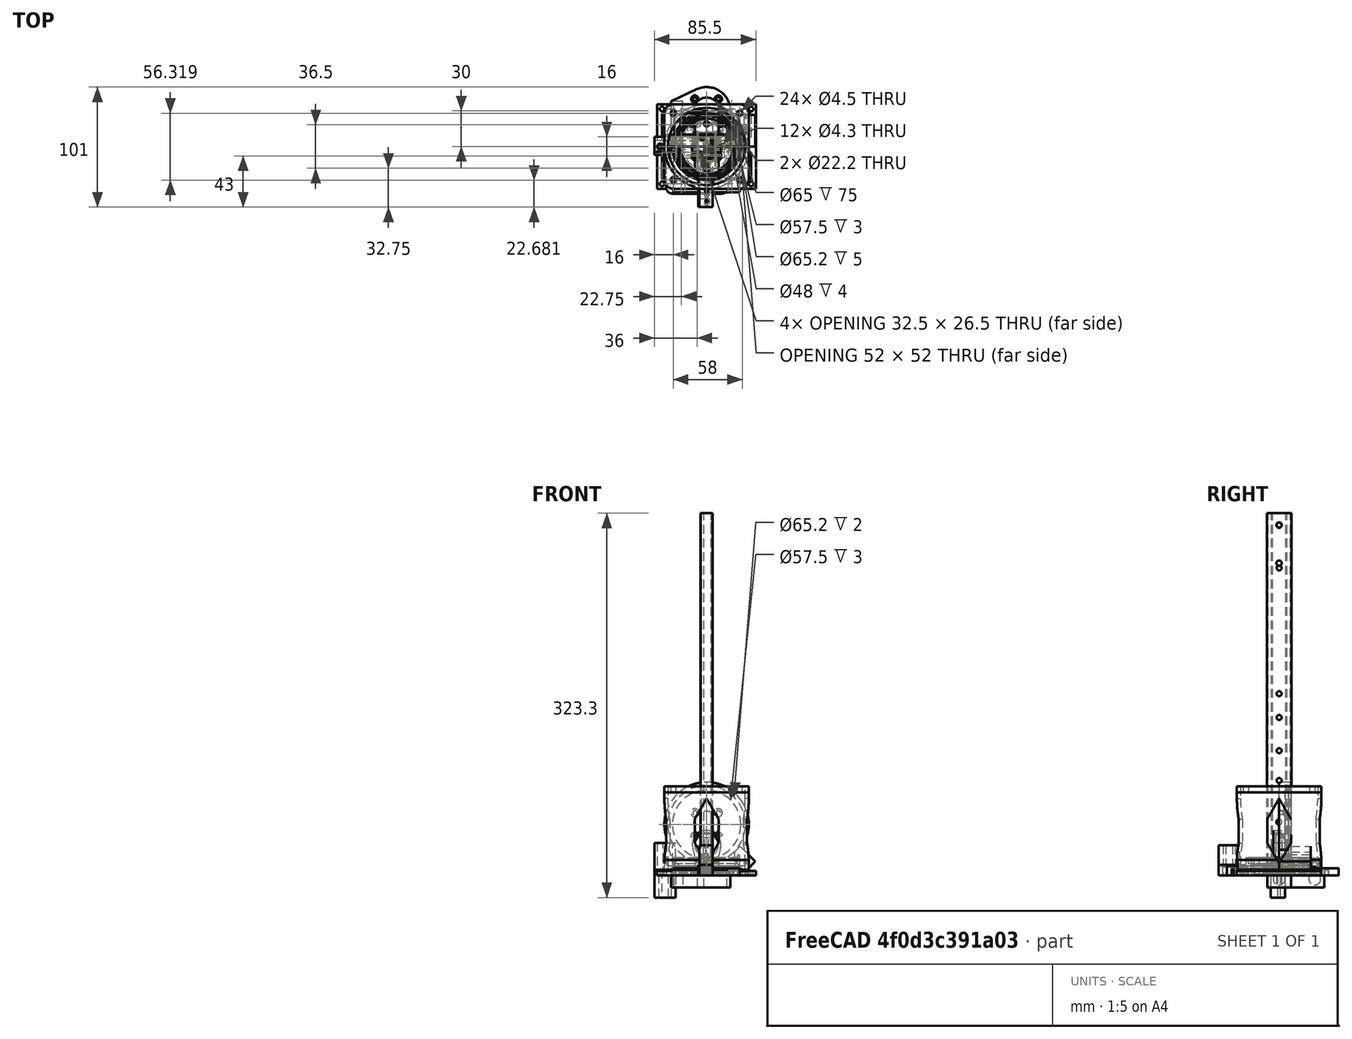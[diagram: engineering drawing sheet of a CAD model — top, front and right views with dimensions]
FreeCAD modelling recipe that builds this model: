
FCSTD DOCUMENT  (FreeCAD 0.19R24276 (Git))
Label: A4
License: All rights reserved
LicenseURL: http://en.wikipedia.org/wiki/All_rights_reserved
objects: Sketcher::SketchObject×66, PartDesign::CoordinateSystem×49, PartDesign::Pad×43, App::Link×43, TechDraw::DrawViewDimension×20, PartDesign::Body×19, App::Part×19, PartDesign::Pocket×11, PartDesign::Hole×10, TechDraw::DrawSVGTemplate×3, TechDraw::DrawProjGroupItem×3, TechDraw::DrawProjGroup×3, TechDraw::DrawPage×3, App::DocumentObjectGroup×2, App::FeaturePython×1, PartDesign::PolarPattern×1, PartDesign::Groove×1, PartDesign::Revolution×1
note: 267 computed .brp shape members not serialized (recipe doc carries the construction recipe); baked Part::Feature solids carry a one-line shape summary decoded from their .brp
EXTERNAL_REF file=HUB-545616.FCStd obj=face2
EXTERNAL_REF file=HUB-545616.FCStd obj=_45616_assembly
EXTERNAL_REF file=BALL-6810.FCStd obj=LCS_0
EXTERNAL_REF file=PULLEY-615432.FCStd obj=LCS_1
EXTERNAL_REF file=PULLEY-615432.FCStd obj=_15432_assembly
EXTERNAL_REF file=BALL-6-19-6.FCStd obj=LCS_0
EXTERNAL_REF file=BALL-6-19-6.FCStd obj=Part
EXTERNAL_REF file=WASHER-M6.FCStd obj=LCS_1
EXTERNAL_REF file=WASHER-M6.FCStd obj=WASHER_M6
EXTERNAL_REF file=HUB-545616.FCStd obj=flatFace
EXTERNAL_REF file=BALL-6808.FCStd obj=LCS_0
EXTERNAL_REF file=SCREW-M4X40.FCStd obj=LCS_0
EXTERNAL_REF file=SCREW-M4X40.FCStd obj=SCREW_M4X40
EXTERNAL_REF file=MOTOR-11HS12-0674S-PG27-E22-300.FCStd obj=mount
EXTERNAL_REF file=MOTOR-11HS12-0674S-PG27-E22-300.FCStd obj=Body
EXTERNAL_REF file=BELT-XL-180-375.FCStd obj=LCS_1
EXTERNAL_REF file=BELT-XL-180-375.FCStd obj=Body
EXTERNAL_REF file=MOTOR-17HS13-0404S-PG27.FCStd obj=LCS_0
EXTERNAL_REF file=MOTOR-17HS13-0404S-PG27.FCStd obj=Part
EXTERNAL_REF file=BALL-6810.FCStd obj=Part
EXTERNAL_REF file=BALL-6808.FCStd obj=Part
EXTERNAL_REF file=HUB_1309_0016_0006.FCStd obj=flat
EXTERNAL_REF file=A4-GRIPPER.FCStd obj=A4001
EXTERNAL_REF file=A4-GRIPPER.FCStd obj=Model
EXTERNAL_REF file=SCREW_8X375.FCStd obj=LCS_0
EXTERNAL_REF file=SCREW_8X375.FCStd obj=Part
EXTERNAL_REF file=SCREW_8X250.FCStd obj=LCS_1
EXTERNAL_REF file=SCREW_8X250.FCStd obj=Part
EXTERNAL_REF file=HUB_1309_0016_0006.FCStd obj=_309_0016_0006_assembly
EXTERNAL_REF file=Paint Roller Copy/A4_PAINT_ROLLER_1V0.FCStd obj=robot001
EXTERNAL_REF file=Paint Roller Copy/A4_PAINT_ROLLER_1V0.FCStd obj=Model

FEATURE [PartDesign::CoordinateSystem] LCS_Origin
  AttacherType = Attacher::AttachEngine3D
  MapMode = 2
  Support = -> [X_Axis]
FEATURE [App::DocumentObjectGroup] Constraints
FEATURE [App::FeaturePython] Variables  label="var"  # WARN: FeaturePython — macro-defined, semantics opaque (R4)
  J2BaseEncoderH = 27.5
  J3BaseEncoderH = 23.5
  LimitSwitchThroughHoleLoc1 = 3.5
  LimitSwitchThroughHoleLoc2 = 4.5
  angleG = 0
  angleJ0 = -90
  angleJ1 = -90
  angleJ2 = 180
  angleJ3 = -45
  baseJ0ID = 92
  baseJ0LimitOffset = 8
  baseJ1EncoderH = 26.5
  baseJ1FlatFace = 30.5941
  baseJ1HoleP1 = 20
  baseJ1HoleP2 = 24
  baseJ1HoleP3 = 50
  baseJ1HoleP4 = 14
  baseJ1MotorH = 43
  baseJ1OD = 66
  baseJ2OD = 52
  encoderJ0H = 25.5
  gripperMobileOD = 27
  hubHoleD = 3.81
  hubHolePD = 19.558
  hubScrewCBOR = 2.35
  humerusW = 20.6375
  limitSwitchHoleD = 3.1
  limitSwitchHoleLoc = 3
  limitSwitchHoleP = 7
  limitSwitchL = 13
  limitSwitchThroughHoleL = 3
  limitSwitchThroughHoleW = 2
  limitSwitchW = 14
  m4HeatSetD = 6.2
  motorJ0HoleD = 3.3
  motorJ0HolePD = 28
  motorJ0LocD = 22.2
  plateJ1HumerusHoleP = 40
  riserHoleD = 4.5
  riserHoleP = 81
  riserID = 65
  riserOD = 71
  screw6BHD = 6.6548
  tensionJ2 = 12
  tensionerJ2ScrewH = 9
  thrustBearingJ0T = 5
  expr: hubHolePD = 0.77 * 25.4
  expr: baseJ1FlatFace = cos(asin(33 / 45)) * 45
  expr: humerusW = 13 / 16 * 25.4
  expr: screw6BHD = 25.4 * 0.262
FEATURE [PartDesign::CoordinateSystem] LCS_0
  AttacherType = Attacher::AttachEngine3D
  MapMode = 2
  Support = -> [X_Axis001]
FEATURE [Sketcher::SketchObject] Sketch002
  AttachmentOffset = pos=(0,0,70) rot=(0,0,1;0rad)
  FullyConstrained = true
  MapMode = 5
  Placement = pos=(0,0,70) rot=(0,0,1;0rad)
  Support = -> [XY_Plane002]
  expr: Constraints[22] = <<var>>.riserHoleD
  expr: Constraints[27] = <<var>>.riserOD - 1
  expr: Constraints[12] = <<var>>.riserOD - 15
  expr: Constraints[13] = <<var>>.riserOD
  sketch-geometry (13):
    g0: LineSegment StartX=-28 StartY=35.5 StartZ=0 EndX=28 EndY=35.5 EndZ=0
    g1: LineSegment StartX=35.5 StartY=28 StartZ=0 EndX=35.5 EndY=-28 EndZ=0
    g2: LineSegment StartX=28 StartY=-35.5 StartZ=0 EndX=-28 EndY=-35.5 EndZ=0
    g3: LineSegment StartX=-35.5 StartY=-28 StartZ=0 EndX=-35.5 EndY=28 EndZ=0
    g4: ArcOfCircle CenterX=-28 CenterY=28 CenterZ=0 NormalX=0 NormalY=0 NormalZ=1 AngleXU=0 Radius=7.5 StartAngle=1.5708 EndAngle=3.14159
    g5: ArcOfCircle CenterX=28 CenterY=28 CenterZ=0 NormalX=0 NormalY=0 NormalZ=1 AngleXU=0 Radius=7.5 StartAngle=0 EndAngle=1.5708
    g6: ArcOfCircle CenterX=28 CenterY=-28 CenterZ=0 NormalX=0 NormalY=0 NormalZ=1 AngleXU=0 Radius=7.5 StartAngle=4.71239 EndAngle=6.28319
    g7: ArcOfCircle CenterX=-28 CenterY=-28 CenterZ=0 NormalX=0 NormalY=0 NormalZ=1 AngleXU=0 Radius=7.5 StartAngle=3.14159 EndAngle=4.71239
    g8: Circle CenterX=-28 CenterY=28 CenterZ=0 NormalX=0 NormalY=0 NormalZ=1 AngleXU=0 Radius=2.25
    g9: Circle CenterX=28 CenterY=28 CenterZ=0 NormalX=0 NormalY=0 NormalZ=1 AngleXU=0 Radius=2.25
    g10: Circle CenterX=28 CenterY=-28 CenterZ=0 NormalX=0 NormalY=0 NormalZ=1 AngleXU=0 Radius=2.25
    g11: Circle CenterX=-28 CenterY=-28 CenterZ=0 NormalX=0 NormalY=0 NormalZ=1 AngleXU=0 Radius=2.25
    g12: Circle CenterX=0 CenterY=0 CenterZ=0 NormalX=0 NormalY=0 NormalZ=1 AngleXU=0 Radius=35
  constraints (28):
    c: Horizontal(g0)
    c: Horizontal(g2)
    c: Vertical(g1)
    c: Vertical(g3)
    c: Tangent(g0,g4) = 1.5708
    c: Tangent(g3,g4) = 1.5708
    c: Tangent(g0,g5) = 1.5708
    c: Tangent(g1,g5) = 1.5708
    c: Tangent(g1,g6) = 1.5708
    c: Tangent(g2,g6) = 1.5708
    c: Tangent(g3,g7) = 1.5708
    c: Tangent(g2,g7) = 1.5708
    c: DistanceX(g4,g5) = 56
    c: DistanceX(g3,g1) = 71
    c: Equal(g7,g6)
    c: Symmetric(g4,g5,g-2)
    c: Symmetric(g4,g7,g-1)
    c: Equal(g3,g0)
    c: Coincident(g8,g4)
    c: Coincident(g9,g5)
    c: Coincident(g10,g6)
    c: Coincident(g11,g7)
    c: Diameter(g11) = 4.5
    c: Equal(g11,g8)
    c: Equal(g11,g9)
    c: Equal(g11,g10)
    c: Coincident(g12,g-1)
    c: Diameter(g12) = 70
FEATURE [Sketcher::SketchObject] Sketch003
  FullyConstrained = true
  MapMode = 5
  Placement = pos=(0,0,0) rot=(1,0,0;1.5708rad)
  Support = -> [XZ_Plane002]
  sketch-geometry (8):
    g0: LineSegment StartX=0 StartY=64.8205 StartZ=0 EndX=-10 EndY=47.5 EndZ=0
    g1: LineSegment StartX=-10 StartY=47.5 StartZ=0 EndX=-10 EndY=27.5 EndZ=0
    g2: LineSegment StartX=-10 StartY=27.5 StartZ=0 EndX=0 EndY=10.1795 EndZ=0
    g3: LineSegment StartX=0 StartY=10.1795 StartZ=0 EndX=10 EndY=27.5 EndZ=0
    g4: LineSegment StartX=10 StartY=27.5 StartZ=0 EndX=10 EndY=47.5 EndZ=0
    g5: LineSegment StartX=10 StartY=47.5 StartZ=0 EndX=0 EndY=64.8205 EndZ=0
    g6: GeomPoint X=0 Y=37.5 Z=0
    g7: LineSegment StartX=-10 StartY=47.5 StartZ=0 EndX=10 EndY=27.5 EndZ=0
  constraints (21):
    c: PointOnObject(g0,g-2)
    c: Coincident(g0,g1)
    c: Vertical(g1)
    c: Coincident(g1,g2)
    c: PointOnObject(g2,g-2)
    c: Coincident(g2,g3)
    c: Coincident(g3,g4)
    c: Vertical(g4)
    c: Coincident(g4,g5)
    c: Coincident(g5,g0)
    c: Symmetric(g0,g4,g-2)
    c: Equal(g1,g4)
    c: Angle(g0,g5) = 1.0472
    c: DistanceX(g0,g4) = 20
    c: PointOnObject(g6,g-2)
    c: Coincident(g7,g0)
    c: Coincident(g7,g3)
    c: PointOnObject(g6,g7)
    c: DistanceY(g-1,g6) = 37.5
    c: Equal(g2,g0)
    c: DistanceY(g1,g1) = 20
FEATURE [Sketcher::SketchObject] Sketch001
  FullyConstrained = true
  MapMode = 5
  Support = -> [XY_Plane002]
  expr: Constraints[22] = <<var>>.riserHoleD
  expr: Constraints[27] = Variables.riserOD - 1
  expr: Constraints[12] = Variables.riserOD - 15
  expr: Constraints[13] = Variables.riserOD
  sketch-geometry (13):
    g0: LineSegment StartX=-28 StartY=35.5 StartZ=0 EndX=28 EndY=35.5 EndZ=0
    g1: LineSegment StartX=35.5 StartY=28 StartZ=0 EndX=35.5 EndY=-28 EndZ=0
    g2: LineSegment StartX=28 StartY=-35.5 StartZ=0 EndX=-28 EndY=-35.5 EndZ=0
    g3: LineSegment StartX=-35.5 StartY=-28 StartZ=0 EndX=-35.5 EndY=28 EndZ=0
    g4: ArcOfCircle CenterX=-28 CenterY=28 CenterZ=0 NormalX=0 NormalY=0 NormalZ=1 AngleXU=0 Radius=7.5 StartAngle=1.5708 EndAngle=3.14159
    g5: ArcOfCircle CenterX=28 CenterY=28 CenterZ=0 NormalX=0 NormalY=0 NormalZ=1 AngleXU=0 Radius=7.5 StartAngle=1e-16 EndAngle=1.5708
    g6: ArcOfCircle CenterX=28 CenterY=-28 CenterZ=0 NormalX=0 NormalY=0 NormalZ=1 AngleXU=0 Radius=7.5 StartAngle=4.71239 EndAngle=6.28319
    g7: ArcOfCircle CenterX=-28 CenterY=-28 CenterZ=0 NormalX=0 NormalY=0 NormalZ=1 AngleXU=0 Radius=7.5 StartAngle=3.14159 EndAngle=4.71239
    g8: Circle CenterX=-28 CenterY=28 CenterZ=0 NormalX=0 NormalY=0 NormalZ=1 AngleXU=0 Radius=2.25
    g9: Circle CenterX=28 CenterY=28 CenterZ=0 NormalX=0 NormalY=0 NormalZ=1 AngleXU=0 Radius=2.25
    g10: Circle CenterX=28 CenterY=-28 CenterZ=0 NormalX=0 NormalY=0 NormalZ=1 AngleXU=0 Radius=2.25
    g11: Circle CenterX=-28 CenterY=-28 CenterZ=0 NormalX=0 NormalY=0 NormalZ=1 AngleXU=0 Radius=2.25
    g12: Circle CenterX=0 CenterY=0 CenterZ=0 NormalX=0 NormalY=0 NormalZ=1 AngleXU=0 Radius=35
  constraints (28):
    c: Horizontal(g0)
    c: Horizontal(g2)
    c: Vertical(g1)
    c: Vertical(g3)
    c: Tangent(g0,g4) = 1.5708
    c: Tangent(g3,g4) = 1.5708
    c: Tangent(g0,g5) = 1.5708
    c: Tangent(g1,g5) = 1.5708
    c: Tangent(g1,g6) = 1.5708
    c: Tangent(g2,g6) = 1.5708
    c: Tangent(g3,g7) = 1.5708
    c: Tangent(g2,g7) = 1.5708
    c: DistanceX(g4,g5) = 56
    c: DistanceX(g3,g1) = 71
    c: Equal(g7,g6)
    c: Symmetric(g4,g5,g-2)
    c: Symmetric(g4,g7,g-1)
    c: Equal(g3,g0)
    c: Coincident(g8,g4)
    c: Coincident(g9,g5)
    c: Coincident(g10,g6)
    c: Coincident(g11,g7)
    c: Diameter(g11) = 4.5
    c: Equal(g11,g8)
    c: Equal(g11,g9)
    c: Equal(g11,g10)
    c: Coincident(g12,g-1)
    c: Diameter(g12) = 70
FEATURE [Sketcher::SketchObject] Sketch
  FullyConstrained = true
  MapMode = 5
  Support = -> [XY_Plane002]
  sketch-geometry (7):
    g0: Circle CenterX=0 CenterY=0 CenterZ=0 NormalX=0 NormalY=0 NormalZ=1 AngleXU=0 Radius=32.5
    g1: Circle CenterX=0 CenterY=0 CenterZ=0 NormalX=0 NormalY=0 NormalZ=1 AngleXU=0 Radius=35.5
    g2: LineSegment StartX=-21.15 StartY=21.15 StartZ=0 EndX=21.15 EndY=21.15 EndZ=0
    g3: LineSegment StartX=21.15 StartY=21.15 StartZ=0 EndX=21.15 EndY=-21.15 EndZ=0
    g4: LineSegment StartX=21.15 StartY=-21.15 StartZ=0 EndX=-21.15 EndY=-21.15 EndZ=0
    g5: LineSegment StartX=-21.15 StartY=-21.15 StartZ=0 EndX=-21.15 EndY=21.15 EndZ=0
    g6: Circle CenterX=0 CenterY=0 CenterZ=0 NormalX=0 NormalY=0 NormalZ=1 AngleXU=0 Radius=29.9106
  constraints (17):
    c: Coincident(g0,g-1)
    c: Coincident(g1,g0)
    c: Diameter(g1) = 71
    c: Diameter(g0) = 65
    c: Coincident(g2,g3)
    c: Coincident(g3,g4)
    c: Coincident(g4,g5)
    c: Coincident(g5,g2)
    c: Horizontal(g4)
    c: Vertical(g3)
    c: Symmetric(g2,g2,g-2)
    c: Equal(g2,g5)
    c: Symmetric(g2,g4,g-1)
    c: DistanceX(g2,g2) = 42.3
    c: Coincident(g6,g0)
    c: Diameter(g6) = 59.8212
    c: PointOnObject(g3,g6)
FEATURE [PartDesign::Pad] Pad
  Direction = (1,1,1)
  Length = 75
  Length2 = 100
  Profile = -> Sketch
  Refine = true
  Type = 0
FEATURE [PartDesign::Pad] Pad001
  BaseFeature = -> Pad
  Direction = (1,1,1)
  Length = 5
  Length2 = 100
  Profile = -> Sketch001
  Refine = true
  Type = 0
FEATURE [PartDesign::Pad] Pad002
  BaseFeature = -> Pad001
  Direction = (1,1,1)
  Length = 5
  Length2 = 100
  Profile = -> Sketch002
  Refine = true
  Type = 0
FEATURE [PartDesign::Pocket] Pocket
  BaseFeature = -> Pad002
  Length = 5
  Length2 = 100
  Midplane = true
  Profile = -> Sketch003
  Refine = true
  Type = 1
FEATURE [PartDesign::PolarPattern] PolarPattern
  Angle = 90
  Axis = -> Sketch003 [V_Axis]
  BaseFeature = -> Pocket
  Occurrences = 2
  Originals = -> [Pocket]
  Refine = true
FEATURE [PartDesign::Body] Body
  Group = -> [Sketch,Pad,Sketch001,Sketch002,Pad001,Pad002,Sketch003,Pocket,PolarPattern]
  Origin = -> Origin002
  Tip = -> PolarPattern
FEATURE [PartDesign::CoordinateSystem] baseJ0
  AttacherType = Attacher::AttachEngine3D
  MapMode = 11
  Placement = pos=(0,0,75) rot=(0,0,1;1.5708rad)
  Support = -> [PolarPattern]
FEATURE [PartDesign::CoordinateSystem] LCS_0001
  AttacherType = Attacher::AttachEngine3D
  MapMode = 2
  Support = -> [X_Axis003]
FEATURE [Sketcher::SketchObject] Sketch004
  FullyConstrained = true
  MapMode = 5
  Support = -> [XY_Plane004]
  expr: Constraints[46] = <<var>>.motorJ0HoleD
  expr: Constraints[41] = <<var>>.motorJ0LocD
  expr: Constraints[40] = <<var>>.motorJ0HolePD
  expr: Constraints[24] = <<var>>.riserOD
  expr: Constraints[20] = <<var>>.riserOD - 15
  expr: Constraints[16] = <<var>>.riserHoleD
  sketch-geometry (22):
    g0: LineSegment StartX=-28 StartY=35.5 StartZ=0 EndX=28 EndY=35.5 EndZ=0
    g1: LineSegment StartX=35.5 StartY=28 StartZ=0 EndX=35.5 EndY=-28 EndZ=0
    g2: LineSegment StartX=28 StartY=-35.5 StartZ=0 EndX=-28 EndY=-35.5 EndZ=0
    g3: LineSegment StartX=-35.5 StartY=-28 StartZ=0 EndX=-35.5 EndY=28 EndZ=0
    g4: ArcOfCircle CenterX=-28 CenterY=28 CenterZ=0 NormalX=0 NormalY=0 NormalZ=1 AngleXU=0 Radius=7.5 StartAngle=1.5708 EndAngle=3.14159
    g5: ArcOfCircle CenterX=-28 CenterY=-28 CenterZ=0 NormalX=0 NormalY=0 NormalZ=1 AngleXU=0 Radius=7.5 StartAngle=3.14159 EndAngle=4.71239
    g6: ArcOfCircle CenterX=28 CenterY=-28 CenterZ=0 NormalX=0 NormalY=0 NormalZ=1 AngleXU=0 Radius=7.5 StartAngle=4.71239 EndAngle=6.28319
    g7: ArcOfCircle CenterX=28 CenterY=28 CenterZ=0 NormalX=0 NormalY=0 NormalZ=1 AngleXU=0 Radius=7.5 StartAngle=-9e-16 EndAngle=1.5708
    g8: Circle CenterX=-28 CenterY=28 CenterZ=0 NormalX=0 NormalY=0 NormalZ=1 AngleXU=0 Radius=2.25
    g9: Circle CenterX=28 CenterY=28 CenterZ=0 NormalX=0 NormalY=0 NormalZ=1 AngleXU=0 Radius=2.25
    g10: Circle CenterX=28 CenterY=-28 CenterZ=0 NormalX=0 NormalY=0 NormalZ=1 AngleXU=0 Radius=2.25
    g11: Circle CenterX=-28 CenterY=-28 CenterZ=0 NormalX=0 NormalY=0 NormalZ=1 AngleXU=0 Radius=2.25
    g12: Circle CenterX=0 CenterY=0 CenterZ=0 NormalX=0 NormalY=0 NormalZ=1 AngleXU=0 Radius=11.1
    g13: LineSegment StartX=-9.89949 StartY=9.89949 StartZ=0 EndX=9.89949 EndY=9.89949 EndZ=0
    g14: LineSegment StartX=9.89949 StartY=9.89949 StartZ=0 EndX=9.89949 EndY=-9.89949 EndZ=0
    g15: LineSegment StartX=9.89949 StartY=-9.89949 StartZ=0 EndX=-9.89949 EndY=-9.89949 EndZ=0
    g16: LineSegment StartX=-9.89949 StartY=-9.89949 StartZ=0 EndX=-9.89949 EndY=9.89949 EndZ=0
    g17: Circle CenterX=0 CenterY=0 CenterZ=0 NormalX=0 NormalY=0 NormalZ=1 AngleXU=0 Radius=14
    g18: Circle CenterX=-9.89949 CenterY=9.89949 CenterZ=0 NormalX=0 NormalY=0 NormalZ=1 AngleXU=0 Radius=1.65
    g19: Circle CenterX=9.89949 CenterY=9.89949 CenterZ=0 NormalX=0 NormalY=0 NormalZ=1 AngleXU=0 Radius=1.65
    g20: Circle CenterX=9.89949 CenterY=-9.89949 CenterZ=0 NormalX=0 NormalY=0 NormalZ=1 AngleXU=0 Radius=1.65
    g21: Circle CenterX=-9.89949 CenterY=-9.89949 CenterZ=0 NormalX=0 NormalY=0 NormalZ=1 AngleXU=0 Radius=1.65
  constraints (50):
    c: Horizontal(g0)
    c: Horizontal(g2)
    c: Vertical(g1)
    c: Vertical(g3)
    c: Tangent(g0,g4) = 1.5708
    c: Tangent(g3,g4) = 1.5708
    c: Tangent(g3,g5) = 1.5708
    c: Tangent(g2,g5) = 1.5708
    c: Tangent(g2,g6) = 1.5708
    c: Tangent(g1,g6) = 1.5708
    c: Tangent(g1,g7) = 1.5708
    c: Tangent(g0,g7) = 1.5708
    c: Coincident(g8,g4)
    c: Coincident(g9,g7)
    c: Coincident(g10,g6)
    c: Coincident(g11,g5)
    c: Diameter(g11) = 4.5
    c: Equal(g11,g8)
    c: Equal(g11,g9)
    c: Equal(g11,g10)
    c: DistanceX(g4,g7) = 56
    c: Symmetric(g4,g5,g-1)
    c: Symmetric(g4,g7,g-2)
    c: Equal(g0,g3)
    c: DistanceX(g3,g1) = 71
    c: Equal(g6,g7)
    c: Coincident(g12,g-1)
    c: Coincident(g13,g14)
    c: Coincident(g14,g15)
    c: Coincident(g15,g16)
    c: Coincident(g16,g13)
    c: Horizontal(g13)
    c: Horizontal(g15)
    c: Vertical(g14)
    c: Vertical(g16)
    c: Coincident(g17,g12)
    c: PointOnObject(g13,g17)
    c: PointOnObject(g13,g17)
    c: Equal(g14,g15)
    c: PointOnObject(g14,g17)
    c: Diameter(g17) = 28
    c: Diameter(g12) = 22.2
    c: Coincident(g18,g13)
    c: Coincident(g19,g13)
    c: Coincident(g20,g14)
    c: Coincident(g21,g15)
    c: Diameter(g21) = 3.3
    c: Equal(g21,g20)
    c: Equal(g21,g19)
    c: Equal(g21,g18)
FEATURE [PartDesign::Pad] Pad005
  Direction = (1,1,1)
  Length = 5
  Length2 = 100
  Profile = -> Sketch004
  Refine = true
  Type = 0
FEATURE [Sketcher::SketchObject] Sketch005
  AttachmentOffset = pos=(0,0,5) rot=(0,0,1;0rad)
  FullyConstrained = true
  MapMode = 5
  Placement = pos=(0,0,5) rot=(0,0,1;0rad)
  Support = -> [XY_Plane004]
  expr: .AttachmentOffset.Base.z = 5
  sketch-geometry (2):
    g0: Circle CenterX=0 CenterY=0 CenterZ=0 NormalX=0 NormalY=0 NormalZ=1 AngleXU=0 Radius=35.5
    g1: Circle CenterX=0 CenterY=0 CenterZ=0 NormalX=0 NormalY=0 NormalZ=1 AngleXU=0 Radius=32.6
  constraints (4):
    c: Coincident(g0,g-1)
    c: Coincident(g1,g0)
    c: Diameter(g1) = 65.2
    c: Diameter(g0) = 71
FEATURE [PartDesign::Pad] Pad006
  BaseFeature = -> Pad005
  Direction = (1,1,1)
  Length = 8
  Length2 = 100
  Profile = -> Sketch005
  Refine = true
  Type = 0
FEATURE [App::Link] RISER_1_0001  label="RISER"
  AssemblyType = Asm4EE
  AttachedBy = #LCS_0
  AttachedTo = Parent Assembly#LCS_Origin
  LinkedObject = -> RISER_1_0
  expr: Placement = LCS_Origin.Placement * AttachmentOffset * LCS_0.Placement ^ -1
FEATURE [App::Link] BASE_J0_1_0001
  AssemblyType = Asm4EE
  AttachedBy = #LCS_0001
  AttachedTo = RISER_1_0001#baseJ0
  LinkPlacement = pos=(0,0,75) rot=(0,0,1;1.5708rad)
  LinkedObject = -> BASE_J0_1_0
  Placement = pos=(0,0,75) rot=(0,0,1;1.5708rad)
  expr: Placement = RISER_1_0001.Placement * baseJ0.Placement * AttachmentOffset * LCS_0001.Placement ^ -1
FEATURE [App::Link] HUB_545616_1
  AssemblyType = Asm4EE
  AttachedBy = #face2
  AttachedTo = BASE_J0_1_0001#LCS_0001
  AttachmentOffset = pos=(0,0,7) rot=(0,0,-1;-1.5708rad)
  LinkPlacement = pos=(17.0898,-21.6153,88.521) rot=(0.57735,-0.57735,-0.57735;2.0944rad)
  LinkedObject = -> <external HUB-545616.FCStd>#_45616_assembly
  Placement = pos=(17.0898,-21.6153,88.521) rot=(0.57735,-0.57735,-0.57735;2.0944rad)
  expr: Placement = BASE_J0_1_0001.Placement * LCS_0001.Placement * AttachmentOffset * HUB_545616#face2.Placement ^ -1
  expr: .AttachmentOffset.Rotation.Angle = <<var>>.angleJ0
FEATURE [PartDesign::CoordinateSystem] LCS_0002
  AttacherType = Attacher::AttachEngine3D
  MapMode = 2
  Support = -> [X_Axis005]
FEATURE [Sketcher::SketchObject] Sketch008
  FullyConstrained = true
  MapMode = 5
  Support = -> [XY_Plane006]
  sketch-geometry (2):
    g0: Circle CenterX=0 CenterY=0 CenterZ=0 NormalX=0 NormalY=0 NormalZ=1 AngleXU=0 Radius=3.1
    g1: Circle CenterX=0 CenterY=0 CenterZ=0 NormalX=0 NormalY=0 NormalZ=1 AngleXU=0 Radius=27
  constraints (4):
    c: Diameter(g0) = 6.2
    c: Coincident(g0,g-1)
    c: Coincident(g1,g0)
    c: Diameter(g1) = 54
FEATURE [PartDesign::Pad] Pad007
  AllowMultiFace = false
  Direction = (1,1,1)
  Length = 8
  Length2 = 100
  Profile = -> Sketch008
  Type = 0
FEATURE [Sketcher::SketchObject] Sketch012
  AttachmentOffset = pos=(0,0,8) rot=(0,0,1;0rad)
  FullyConstrained = true
  MapMode = 5
  Placement = pos=(0,0,8) rot=(0,0,1;0rad)
  Support = -> [XY_Plane006]
  expr: Constraints[16] = <<var>>.hubHoleD
  expr: Constraints[15] = <<var>>.hubHolePD
  sketch-geometry (9):
    g0: LineSegment StartX=-6.9148 StartY=6.9148 StartZ=0 EndX=6.9148 EndY=6.9148 EndZ=0
    g1: LineSegment StartX=6.9148 StartY=6.9148 StartZ=0 EndX=6.9148 EndY=-6.9148 EndZ=0
    g2: LineSegment StartX=6.9148 StartY=-6.9148 StartZ=0 EndX=-6.9148 EndY=-6.9148 EndZ=0
    g3: LineSegment StartX=-6.9148 StartY=-6.9148 StartZ=0 EndX=-6.9148 EndY=6.9148 EndZ=0
    g4: Circle CenterX=-6.9148 CenterY=6.9148 CenterZ=0 NormalX=0 NormalY=0 NormalZ=1 AngleXU=0 Radius=1.905
    g5: Circle CenterX=6.9148 CenterY=6.9148 CenterZ=0 NormalX=0 NormalY=0 NormalZ=1 AngleXU=0 Radius=1.905
    g6: Circle CenterX=6.9148 CenterY=-6.9148 CenterZ=0 NormalX=0 NormalY=0 NormalZ=1 AngleXU=0 Radius=1.905
    g7: Circle CenterX=-6.9148 CenterY=-6.9148 CenterZ=0 NormalX=0 NormalY=0 NormalZ=1 AngleXU=0 Radius=1.905
    g8: LineSegment StartX=-6.9148 StartY=6.9148 StartZ=0 EndX=6.9148 EndY=-6.9148 EndZ=0
  constraints (20):
    c: Coincident(g0,g1)
    c: Coincident(g1,g2)
    c: Coincident(g2,g3)
    c: Coincident(g3,g0)
    c: Horizontal(g2)
    c: Vertical(g1)
    c: Symmetric(g0,g0,g-2)
    c: Symmetric(g0,g2,g-1)
    c: Equal(g3,g0)
    c: Coincident(g4,g0)
    c: Coincident(g5,g0)
    c: Coincident(g6,g1)
    c: Coincident(g7,g2)
    c: Coincident(g8,g4)
    c: Coincident(g8,g6)
    c: Distance(g8) = 19.558
    c: Diameter(g4) = 3.81
    c: Equal(g4,g7)
    c: Equal(g4,g6)
    c: Equal(g4,g5)
FEATURE [App::Link] PLATE_J0_1_0001  label="J0_PLATE"
  AssemblyType = Asm4EE
  AttachedBy = #LCS_0002
  AttachedTo = BALL_6810_0#LCS_0
  AttachmentOffset = pos=(0,0,7) rot=(0,0,1;-1.5708rad)
  LinkPlacement = pos=(0,0,90) rot=(0,0,1;0rad)
  LinkedObject = -> PLATE_J0_1_0
  Placement = pos=(0,0,90) rot=(0,0,1;0rad)
  expr: .AttachmentOffset.Rotation.Angle = <<var>>.angleJ0
  expr: Placement = BALL_6810_0.Placement * BALL_6810#LCS_0.Placement * AttachmentOffset * LCS_0002.Placement ^ -1
FEATURE [PartDesign::CoordinateSystem] LCS_0003
  AttacherType = Attacher::AttachEngine3D
  MapMode = 2
  Support = -> [X_Axis007]
FEATURE [Sketcher::SketchObject] Sketch016
  FullyConstrained = true
  MapMode = 5
  Support = -> [XY_Plane008]
  sketch-geometry (7):
    g0: LineSegment StartX=-20 StartY=15 StartZ=0 EndX=20 EndY=15 EndZ=0
    g1: Circle CenterX=-20 CenterY=15 CenterZ=0 NormalX=0 NormalY=0 NormalZ=1 AngleXU=0 Radius=2.35
    g2: Circle CenterX=20 CenterY=15 CenterZ=0 NormalX=0 NormalY=0 NormalZ=1 AngleXU=0 Radius=2.35
    g3: LineSegment StartX=-27 StartY=0 StartZ=0 EndX=27 EndY=0 EndZ=0
    g4: LineSegment StartX=27 StartY=0 StartZ=0 EndX=27 EndY=20 EndZ=0
    g5: LineSegment StartX=27 StartY=20 StartZ=0 EndX=-27 EndY=20 EndZ=0
    g6: LineSegment StartX=-27 StartY=20 StartZ=0 EndX=-27 EndY=0 EndZ=0
  constraints (18):
    c: Coincident(g1,g0)
    c: Coincident(g2,g0)
    c: DistanceX(g0,g0) = 40
    c: DistanceY(g-1,g2) = 15
    c: Symmetric(g1,g2,g-2)
    c: Coincident(g4,g5)
    c: Coincident(g5,g6)
    c: Coincident(g6,g3)
    c: Horizontal(g3)
    c: Vertical(g4)
    c: Vertical(g6)
    c: PointOnObject(g3,g-1)
    c: DistanceX(g5,g5) = 54
    c: Symmetric(g5,g4,g-2)
    c: DistanceY(g4,g4) = 20
    c: Coincident(g3,g4)
    c: Diameter(g2) = 4.7
    c: Equal(g2,g1)
FEATURE [PartDesign::Pad] Pad010
  AllowMultiFace = false
  Direction = (1,1,1)
  Length = 5
  Length2 = 100
  Profile = -> Sketch016
  Type = 0
FEATURE [Sketcher::SketchObject] Sketch017
  AttachmentOffset = pos=(0,0,-5) rot=(0,0,1;0rad)
  FullyConstrained = true
  MapMode = 5
  Placement = pos=(0,5,1.1e-15) rot=(1,0,0;1.5708rad)
  Support = -> [XZ_Plane008]
  expr: Constraints[1] = <<var>>.baseJ1MotorH
  sketch-geometry (1):
    g0: Circle CenterX=0 CenterY=43 CenterZ=0 NormalX=0 NormalY=0 NormalZ=1 AngleXU=0 Radius=32.6
  constraints (3):
    c: Diameter(g0) = 65.2
    c: DistanceY(g-1,g0) = 43
    c: PointOnObject(g0,g-2)
FEATURE [Sketcher::SketchObject] Sketch019
  FullyConstrained = true
  MapMode = 5
  Placement = pos=(0,0,0) rot=(1,0,0;1.5708rad)
  Support = -> [XZ_Plane008]
  expr: Constraints[3] = <<var>>.baseJ1MotorH
  expr: Constraints[32] = <<var>>.motorJ0HolePD
  expr: Constraints[23] = <<var>>.motorJ0LocD
  expr: Constraints[18] = <<var>>.motorJ0HoleD
  sketch-geometry (15):
    g0: LineSegment StartX=-27 StartY=5 StartZ=0 EndX=-34.4144 EndY=34.2878 EndZ=0
    g1: LineSegment StartX=34.4144 StartY=34.2878 StartZ=0 EndX=27 EndY=5 EndZ=0
    g2: LineSegment StartX=-27 StartY=5 StartZ=0 EndX=27 EndY=5 EndZ=0
    g3: ArcOfCircle CenterX=0 CenterY=43 CenterZ=0 NormalX=0 NormalY=0 NormalZ=1 AngleXU=0 Radius=35.5 StartAngle=6.03524 EndAngle=9.67272
    g4: Circle CenterX=0 CenterY=43 CenterZ=0 NormalX=0 NormalY=0 NormalZ=1 AngleXU=0 Radius=11.1
    g5: Circle CenterX=9.89949 CenterY=52.8995 CenterZ=0 NormalX=0 NormalY=0 NormalZ=1 AngleXU=0 Radius=1.65
    g6: Circle CenterX=-9.89949 CenterY=52.8995 CenterZ=0 NormalX=0 NormalY=0 NormalZ=1 AngleXU=0 Radius=1.65
    g7: Circle CenterX=9.89949 CenterY=33.1005 CenterZ=0 NormalX=0 NormalY=0 NormalZ=1 AngleXU=0 Radius=1.65
    g8: Circle CenterX=-9.89949 CenterY=33.1005 CenterZ=0 NormalX=0 NormalY=0 NormalZ=1 AngleXU=0 Radius=1.65
    g9: LineSegment StartX=-9.89949 StartY=52.8995 StartZ=0 EndX=9.89949 EndY=52.8995 EndZ=0
    g10: LineSegment StartX=9.89949 StartY=52.8995 StartZ=0 EndX=9.89949 EndY=33.1005 EndZ=0
    g11: LineSegment StartX=9.89949 StartY=33.1005 StartZ=0 EndX=-9.89949 EndY=33.1005 EndZ=0
    g12: LineSegment StartX=-9.89949 StartY=33.1005 StartZ=0 EndX=-9.89949 EndY=52.8995 EndZ=0
    g13: LineSegment StartX=-11.1 StartY=43 StartZ=0 EndX=11.1 EndY=43 EndZ=0
    g14: Circle CenterX=0 CenterY=43 CenterZ=0 NormalX=0 NormalY=0 NormalZ=1 AngleXU=0 Radius=14
  constraints (36):
    c: Coincident(g2,g0)
    c: Coincident(g2,g1)
    c: PointOnObject(g3,g-2)
    c: DistanceY(g-1,g3) = 43
    c: Tangent(g3,g0) = 1.5708
    c: Tangent(g3,g1) = 1.5708
    c: Coincident(g4,g3)
    c: Coincident(g9,g10)
    c: Coincident(g10,g11)
    c: Coincident(g11,g12)
    c: Coincident(g12,g9)
    c: Horizontal(g11)
    c: Vertical(g10)
    c: Vertical(g12)
    c: Coincident(g9,g6)
    c: Coincident(g10,g7)
    c: Coincident(g5,g9)
    c: Coincident(g11,g8)
    c: Diameter(g5) = 3.3
    c: Equal(g5,g7)
    c: Equal(g5,g6)
    c: Equal(g5,g8)
    c: Equal(g10,g9)
    c: Diameter(g4) = 22.2
    c: Symmetric(g6,g5,g-2)
    c: PointOnObject(g3,g13)
    c: Symmetric(g6,g8,g13)
    c: PointOnObject(g13,g4)
    c: PointOnObject(g13,g4)
    c: Symmetric(g0,g1,g-2)
    c: Coincident(g14,g3)
    c: PointOnObject(g5,g14)
    c: Diameter(g14) = 28
    c: Diameter(g3) = 71
    c: DistanceX(g2,g2) = 54
    c: DistanceY(g-1,g0) = 5
FEATURE [PartDesign::Pad] Pad009
  AllowMultiFace = false
  BaseFeature = -> Pad010
  Direction = (1,1,1)
  Length = 10
  Length2 = 8.5
  Profile = -> Sketch019
  Reversed = true
  Type = 0
FEATURE [PartDesign::Pocket] Pocket006
  AllowMultiFace = false
  BaseFeature = -> Pad009
  Length = 5
  Length2 = 100
  Profile = -> Sketch017
  Type = 1
FEATURE [App::Link] BASE_J1_1_0001  label="J1_BASE"
  AssemblyType = Asm4EE
  AttachedBy = #LCS_0003
  AttachedTo = PLATE_J0_1_0001#LCS_0002
  AttachmentOffset = pos=(0,10,8) rot=(0,0,1;0rad)
  LinkPlacement = pos=(4.4e-15,10,98) rot=(0,0,1;0rad)
  LinkedObject = -> BASE_J1_1_0
  Placement = pos=(4.4e-15,10,98) rot=(0,0,1;0rad)
  expr: Placement = PLATE_J0_1_0001.Placement * LCS_0002.Placement * AttachmentOffset * LCS_0003.Placement ^ -1
FEATURE [PartDesign::CoordinateSystem] LCS_0005
  AttacherType = Attacher::AttachEngine3D
  MapMode = 2
  Support = -> [X_Axis012]
FEATURE [PartDesign::CoordinateSystem] LCS_0006
  AttacherType = Attacher::AttachEngine3D
  MapMode = 2
  Support = -> [X_Axis014]
FEATURE [Sketcher::SketchObject] Sketch030
  FullyConstrained = true
  MapMode = 5
  Support = -> [XY_Plane015]
  expr: Constraints[31] = <<var>>.motorJ0HoleD
  expr: Constraints[26] = <<var>>.motorJ0LocD
  expr: Constraints[24] = <<var>>.motorJ0HolePD
  sketch-geometry (32):
    g0: LineSegment StartX=-30 StartY=-10 StartZ=0 EndX=-30 EndY=10 EndZ=0
    g1: LineSegment StartX=20 StartY=30 StartZ=0 EndX=20 EndY=-3.6e-15 EndZ=0
    g2: LineSegment StartX=10 StartY=-10 StartZ=0 EndX=-30 EndY=-10 EndZ=0
    g3: LineSegment StartX=-30 StartY=10 StartZ=0 EndX=70 EndY=10 EndZ=0
    g4: LineSegment StartX=70 StartY=10 StartZ=0 EndX=70 EndY=-10 EndZ=0
    g5: LineSegment StartX=70 StartY=-10 StartZ=0 EndX=-30 EndY=-10 EndZ=0
    g6: LineSegment StartX=-30 StartY=-10 StartZ=0 EndX=-30 EndY=10 EndZ=0
    g7: ArcOfCircle CenterX=0 CenterY=30 CenterZ=0 NormalX=0 NormalY=0 NormalZ=1 AngleXU=0 Radius=20 StartAngle=2e-16 EndAngle=2.01011
    g8: Circle CenterX=0 CenterY=30 CenterZ=0 NormalX=0 NormalY=0 NormalZ=1 AngleXU=0 Radius=14
    g9: LineSegment StartX=-9.89949 StartY=39.8995 StartZ=0 EndX=9.89949 EndY=39.8995 EndZ=0
    g10: LineSegment StartX=9.89949 StartY=39.8995 StartZ=0 EndX=9.89949 EndY=20.1005 EndZ=0
    g11: LineSegment StartX=9.89949 StartY=20.1005 StartZ=0 EndX=-9.89949 EndY=20.1005 EndZ=0
    g12: LineSegment StartX=-9.89949 StartY=20.1005 StartZ=0 EndX=-9.89949 EndY=39.8995 EndZ=0
    g13: Circle CenterX=0 CenterY=30 CenterZ=0 NormalX=0 NormalY=0 NormalZ=1 AngleXU=0 Radius=11.1
    g14: Circle CenterX=-9.89949 CenterY=39.8995 CenterZ=0 NormalX=0 NormalY=0 NormalZ=1 AngleXU=0 Radius=1.65
    g15: Circle CenterX=9.89949 CenterY=39.8995 CenterZ=0 NormalX=0 NormalY=0 NormalZ=1 AngleXU=0 Radius=1.65
    g16: Circle CenterX=9.89949 CenterY=20.1005 CenterZ=0 NormalX=0 NormalY=0 NormalZ=1 AngleXU=0 Radius=1.65
    g17: Circle CenterX=-9.89949 CenterY=20.1005 CenterZ=0 NormalX=0 NormalY=0 NormalZ=1 AngleXU=0 Radius=1.65
    g18: Circle CenterX=0 CenterY=30 CenterZ=0 NormalX=0 NormalY=0 NormalZ=1 AngleXU=0 Radius=18
    g19: GeomPoint X=0 Y=12 Z=0
    g20: ArcOfCircle CenterX=-25 CenterY=0 CenterZ=0 NormalX=0 NormalY=0 NormalZ=1 AngleXU=0 Radius=2.25 StartAngle=1.5708 EndAngle=4.71239
    g21: ArcOfCircle CenterX=-10 CenterY=0 CenterZ=0 NormalX=0 NormalY=0 NormalZ=1 AngleXU=0 Radius=2.25 StartAngle=4.71239 EndAngle=7.85398
    g22: LineSegment StartX=-25 StartY=-2.25 StartZ=0 EndX=-10 EndY=-2.25 EndZ=0
    g23: LineSegment StartX=-25 StartY=2.25 StartZ=0 EndX=-10 EndY=2.25 EndZ=0
    g24: ArcOfCircle CenterX=1.2e-15 CenterY=0 CenterZ=0 NormalX=0 NormalY=0 NormalZ=1 AngleXU=0 Radius=2.25 StartAngle=1.5708 EndAngle=4.71239
    g25: ArcOfCircle CenterX=15 CenterY=-1e-16 CenterZ=0 NormalX=0 NormalY=0 NormalZ=1 AngleXU=0 Radius=2.25 StartAngle=4.71239 EndAngle=7.85398
    g26: LineSegment StartX=8e-16 StartY=-2.25 StartZ=0 EndX=15 EndY=-2.25 EndZ=0
    g27: LineSegment StartX=9e-16 StartY=2.25 StartZ=0 EndX=15 EndY=2.25 EndZ=0
    g28: LineSegment StartX=-30 StartY=10 StartZ=0 EndX=-30 EndY=38 EndZ=0
    g29: LineSegment StartX=-30 StartY=38 StartZ=0 EndX=-8.50644 EndY=48.1008 EndZ=0
    g30: ArcOfCircle CenterX=10 CenterY=2e-16 CenterZ=0 NormalX=0 NormalY=0 NormalZ=1 AngleXU=0 Radius=10 StartAngle=4.71239 EndAngle=6.28319
    g31: GeomPoint X=20 Y=-10 Z=0
  constraints (78):
    c: Vertical(g1)
    c: Horizontal(g2)
    c: Coincident(g3,g4)
    c: Coincident(g4,g5)
    c: Coincident(g5,g6)
    c: Coincident(g6,g3)
    c: Horizontal(g3)
    c: Horizontal(g5)
    c: Vertical(g4)
    c: Symmetric(g3,g5,g-1)
    c: PointOnObject(g7,g-2)
    c: Coincident(g8,g7)
    c: Coincident(g9,g10)
    c: Coincident(g10,g11)
    c: Coincident(g11,g12)
    c: Coincident(g12,g9)
    c: Horizontal(g9)
    c: Horizontal(g11)
    c: Vertical(g10)
    c: Vertical(g12)
    c: PointOnObject(g9,g8)
    c: PointOnObject(g10,g8)
    c: Equal(g9,g10)
    c: PointOnObject(g9,g8)
    c: Diameter(g8) = 28
    c: Coincident(g13,g7)
    c: Diameter(g13) = 22.2
    c: Coincident(g14,g9)
    c: Coincident(g15,g9)
    c: Coincident(g16,g10)
    c: Coincident(g17,g11)
    c: Diameter(g17) = 3.3
    c: Equal(g17,g16)
    c: Equal(g17,g15)
    c: Equal(g17,g14)
    c: Coincident(g18,g7)
    c: Diameter(g18) = 36
    c: PointOnObject(g19,g18)
    c: PointOnObject(g19,g-2)
    c: Diameter(g7) = 40
    c: Tangent(g20,g23)
    c: Tangent(g20,g22)
    c: Tangent(g22,g21)
    c: Tangent(g23,g21)
    c: Horizontal(g22)
    c: Equal(g20,g21)
    c: PointOnObject(g20,g-1)
    c: Tangent(g24,g27)
    c: Tangent(g24,g26)
    c: Tangent(g26,g25)
    c: Tangent(g27,g25)
    c: Horizontal(g26)
    c: Equal(g24,g25)
    c: DistanceX(g23,g23) = 15
    c: Diameter(g21) = 4.5
    c: Equal(g24,g21)
    c: Equal(g27,g23)
    c: DistanceX(g21,g24) = 10
    c: DistanceX(g0,g20) = 5
    c: DistanceY(g4,g4) = 20
    c: DistanceX(g5,g5) = 100
    c: Coincident(g3,g0)
    c: Tangent(g7,g1) = 1.5708
    c: DistanceX(g25,g31) = 5
    c: PointOnObject(g24,g-1)
    c: Coincident(g2,g5)
    c: Coincident(g0,g2)
    c: Coincident(g28,g0)
    c: Vertical(g28)
    c: Coincident(g29,g28)
    c: Tangent(g7,g29) = 1.5708
    c: DistanceY(g-1,g28) = 38
    c: DistanceY(g-1,g7) = 30
    c: PointOnObject(g31,g2)
    c: PointOnObject(g31,g1)
    c: Tangent(g2,g30) = 1.5708
    c: Tangent(g1,g30) = 1.5708
    c: Diameter(g30) = 20
FEATURE [Sketcher::SketchObject] Sketch031
  AttachmentOffset = pos=(0,0,6) rot=(0,0,1;0rad)
  FullyConstrained = true
  MapMode = 5
  Placement = pos=(0,0,6) rot=(0,0,1;0rad)
  Support = -> [XY_Plane015]
  expr: Constraints[28] = <<var>>.humerusW
  expr: Constraints[34] = <<var>>.motorJ0HolePD
  sketch-geometry (15):
    g0: Circle CenterX=9.89949 CenterY=39.8995 CenterZ=0 NormalX=0 NormalY=0 NormalZ=1 AngleXU=0 Radius=3.5
    g1: Circle CenterX=-9.89949 CenterY=39.8995 CenterZ=0 NormalX=0 NormalY=0 NormalZ=1 AngleXU=0 Radius=3.5
    g2: Circle CenterX=0 CenterY=30 CenterZ=0 NormalX=0 NormalY=0 NormalZ=1 AngleXU=0 Radius=14
    g3: LineSegment StartX=-9.89949 StartY=20.1005 StartZ=0 EndX=9.89949 EndY=20.1005 EndZ=0
    g4: LineSegment StartX=9.89949 StartY=20.1005 StartZ=0 EndX=9.89949 EndY=39.8995 EndZ=0
    g5: LineSegment StartX=9.89949 StartY=39.8995 StartZ=0 EndX=-9.89949 EndY=39.8995 EndZ=0
    g6: LineSegment StartX=-9.89949 StartY=39.8995 StartZ=0 EndX=-9.89949 EndY=20.1005 EndZ=0
    g7: Circle CenterX=-9.89949 CenterY=20.1005 CenterZ=0 NormalX=0 NormalY=0 NormalZ=1 AngleXU=0 Radius=3.5
    g8: Circle CenterX=9.89949 CenterY=20.1005 CenterZ=0 NormalX=0 NormalY=0 NormalZ=1 AngleXU=0 Radius=3.5
    g9: LineSegment StartX=-50 StartY=10.3187 StartZ=0 EndX=50 EndY=10.3187 EndZ=0
    g10: LineSegment StartX=50 StartY=10.3187 StartZ=0 EndX=50 EndY=-10.3187 EndZ=0
    g11: LineSegment StartX=50 StartY=-10.3187 StartZ=0 EndX=-50 EndY=-10.3187 EndZ=0
    g12: LineSegment StartX=-50 StartY=-10.3187 StartZ=0 EndX=-50 EndY=10.3187 EndZ=0
    g13: Circle CenterX=0 CenterY=30 CenterZ=0 NormalX=0 NormalY=0 NormalZ=1 AngleXU=0 Radius=18
    g14: GeomPoint X=0 Y=12 Z=0
  constraints (37):
    c: PointOnObject(g2,g-2)
    c: PointOnObject(g0,g2)
    c: Coincident(g3,g4)
    c: Coincident(g4,g5)
    c: Coincident(g5,g6)
    c: Coincident(g6,g3)
    c: Horizontal(g3)
    c: Horizontal(g5)
    c: Vertical(g4)
    c: Vertical(g6)
    c: PointOnObject(g3,g2)
    c: Coincident(g4,g0)
    c: Equal(g5,g6)
    c: Coincident(g5,g1)
    c: PointOnObject(g1,g2)
    c: Coincident(g7,g3)
    c: Coincident(g8,g3)
    c: Diameter(g8) = 7
    c: Equal(g8,g7)
    c: Equal(g8,g0)
    c: Equal(g8,g1)
    c: Coincident(g9,g10)
    c: Coincident(g10,g11)
    c: Coincident(g11,g12)
    c: Coincident(g12,g9)
    c: Horizontal(g11)
    c: Vertical(g12)
    c: Symmetric(g9,g10,g-1)
    c: DistanceY(g10,g10) = 20.6375
    c: DistanceX(g11,g11) = 100
    c: Coincident(g13,g2)
    c: Diameter(g13) = 36
    c: PointOnObject(g14,g13)
    c: PointOnObject(g14,g-2)
    c: Diameter(g2) = 28
    c: Symmetric(g9,g9,g-2)
    c: DistanceY(g-1,g2) = 30
FEATURE [Sketcher::SketchObject] Sketch032
  AttachmentOffset = pos=(0,0,-30) rot=(0,0,1;0rad)
  FullyConstrained = true
  MapMode = 5
  Placement = pos=(-30,6.7e-15,-6.7e-15) rot=(0.57735,0.57735,0.57735;2.0944rad)
  Support = -> [YZ_Plane015]
  expr: Constraints[2] = 6 - <<var>>.tensionerJ2ScrewH
  sketch-geometry (3):
    g0: Circle CenterX=0 CenterY=-3 CenterZ=0 NormalX=0 NormalY=0 NormalZ=1 AngleXU=0 Radius=5
    g1: Circle CenterX=0 CenterY=-3 CenterZ=0 NormalX=0 NormalY=0 NormalZ=1 AngleXU=0 Radius=3.5
    g2: Circle CenterX=30 CenterY=-3 CenterZ=0 NormalX=0 NormalY=0 NormalZ=1 AngleXU=0 Radius=5
  constraints (8):
    c: PointOnObject(g0,g-2)
    c: Diameter(g0) = 10
    c: DistanceY(g-1,g0) = -3
    c: Coincident(g1,g0)
    c: Diameter(g1) = 7
    c: Equal(g2,g0)
    c: Horizontal(g2,g0)
    c: DistanceX(g-1,g2) = 30
FEATURE [PartDesign::Pad] Pad018
  Direction = (1,1,1)
  Length = 6
  Length2 = 100
  Profile = -> Sketch030
  Refine = true
  Type = 0
FEATURE [PartDesign::CoordinateSystem] LCS_0007
  AttacherType = Attacher::AttachEngine3D
  MapMode = 2
  Support = -> [X_Axis016]
FEATURE [PartDesign::CoordinateSystem] LCS_0008
  AttacherType = Attacher::AttachEngine3D
  MapMode = 2
  Support = -> [X_Axis017]
FEATURE [Sketcher::SketchObject] Sketch033
  FullyConstrained = true
  MapMode = 5
  Support = -> [XY_Plane017]
  sketch-geometry (7):
    g0: LineSegment StartX=35 StartY=10 StartZ=0 EndX=35 EndY=-10 EndZ=0
    g1: LineSegment StartX=35 StartY=-10 StartZ=0 EndX=0 EndY=-10 EndZ=0
    g2: LineSegment StartX=0 StartY=-10 StartZ=0 EndX=0 EndY=35 EndZ=0
    g3: LineSegment StartX=0 StartY=35 StartZ=0 EndX=10 EndY=35 EndZ=0
    g4: LineSegment StartX=10 StartY=35 StartZ=0 EndX=35 EndY=10 EndZ=0
    g5: Circle CenterX=15 CenterY=0 CenterZ=0 NormalX=0 NormalY=0 NormalZ=1 AngleXU=0 Radius=2.25
    g6: Circle CenterX=30 CenterY=0 CenterZ=0 NormalX=0 NormalY=0 NormalZ=1 AngleXU=0 Radius=2.25
  constraints (21):
    c: Coincident(g0,g1)
    c: Horizontal(g1)
    c: Coincident(g1,g2)
    c: PointOnObject(g2,g-2)
    c: Vertical(g2)
    c: Coincident(g2,g3)
    c: Horizontal(g3)
    c: Coincident(g3,g4)
    c: Coincident(g4,g0)
    c: DistanceX(g3,g3) = 10
    c: PointOnObject(g5,g-1)
    c: PointOnObject(g6,g-1)
    c: Diameter(g5) = 4.5
    c: Equal(g5,g6)
    c: DistanceX(g-1,g5) = 15
    c: DistanceY(g-1,g2) = 35
    c: DistanceX(g5,g6) = 15
    c: DistanceX(g6,g0) = 5
    c: Symmetric(g0,g0,g-1)
    c: DistanceY(g0,g0) = 20
    c: Angle(g3,g4) = 2.35619
FEATURE [PartDesign::Pad] Pad019
  Direction = (1,1,1)
  Length = 5
  Length2 = 100
  Profile = -> Sketch033
  Type = 0
FEATURE [Sketcher::SketchObject] Sketch035
  FullyConstrained = true
  MapMode = 5
  Placement = pos=(0,0,0) rot=(0.57735,0.57735,0.57735;2.0944rad)
  Support = -> [YZ_Plane016]
  expr: Constraints[12] = <<var>>.tensionerJ2ScrewH
  sketch-geometry (7):
    g0: LineSegment StartX=-10 StartY=0 StartZ=0 EndX=35 EndY=0 EndZ=0
    g1: LineSegment StartX=35 StartY=0 StartZ=0 EndX=35 EndY=14.5 EndZ=0
    g2: LineSegment StartX=35 StartY=14.5 StartZ=0 EndX=-10 EndY=14.5 EndZ=0
    g3: LineSegment StartX=-10 StartY=14.5 StartZ=0 EndX=-10 EndY=0 EndZ=0
    g4: Circle CenterX=0 CenterY=9 CenterZ=0 NormalX=0 NormalY=0 NormalZ=1 AngleXU=0 Radius=2.15
    g5: Circle CenterX=0 CenterY=9 CenterZ=0 NormalX=0 NormalY=0 NormalZ=1 AngleXU=0 Radius=3.5
    g6: Circle CenterX=30 CenterY=9 CenterZ=0 NormalX=0 NormalY=0 NormalZ=1 AngleXU=0 Radius=2.15
  constraints (20):
    c: Coincident(g0,g1)
    c: Coincident(g1,g2)
    c: Coincident(g2,g3)
    c: Coincident(g3,g0)
    c: Horizontal(g0)
    c: Vertical(g1)
    c: Vertical(g3)
    c: PointOnObject(g0,g-1)
    c: PointOnObject(g4,g-2)
    c: Diameter(g4) = 4.3
    c: Coincident(g5,g4)
    c: Diameter(g5) = 7
    c: DistanceY(g-1,g4) = 9
    c: DistanceY(g4,g2) = 5.5
    c: DistanceX(g2,g-1) = 10
    c: DistanceX(g-1,g1) = 35
    c: Equal(g6,g4)
    c: Horizontal(g4,g6)
    c: DistanceX(g-1,g6) = 30
    c: Horizontal(g2)
FEATURE [PartDesign::Pad] Pad020
  BaseFeature = -> Pad019
  Direction = (1,1,1)
  Length = 10
  Length2 = 100
  Profile = -> Sketch035
  Type = 0
FEATURE [Sketcher::SketchObject] Sketch036
  FullyConstrained = true
  MapMode = 5
  Support = -> [XY_Plane015]
  sketch-geometry (17):
    g0: LineSegment StartX=20 StartY=10 StartZ=0 EndX=20 EndY=-3.42695e-11 EndZ=0
    g1: LineSegment StartX=-30 StartY=-10 StartZ=0 EndX=-30 EndY=10 EndZ=0
    g2: ArcOfCircle CenterX=-25 CenterY=0 CenterZ=0 NormalX=0 NormalY=0 NormalZ=1 AngleXU=0 Radius=2.25 StartAngle=1.5708 EndAngle=4.71239
    g3: ArcOfCircle CenterX=-10 CenterY=2e-16 CenterZ=0 NormalX=0 NormalY=0 NormalZ=1 AngleXU=0 Radius=2.25 StartAngle=4.71239 EndAngle=7.85398
    g4: LineSegment StartX=-25 StartY=-2.25 StartZ=0 EndX=-10 EndY=-2.25 EndZ=0
    g5: LineSegment StartX=-25 StartY=2.25 StartZ=0 EndX=-10 EndY=2.25 EndZ=0
    g6: ArcOfCircle CenterX=2.6e-15 CenterY=0 CenterZ=0 NormalX=0 NormalY=0 NormalZ=1 AngleXU=0 Radius=2.25 StartAngle=1.5708 EndAngle=4.71239
    g7: ArcOfCircle CenterX=15 CenterY=2e-16 CenterZ=0 NormalX=0 NormalY=0 NormalZ=1 AngleXU=0 Radius=2.25 StartAngle=4.71239 EndAngle=7.85398
    g8: LineSegment StartX=2.6e-15 StartY=-2.25 StartZ=0 EndX=15 EndY=-2.25 EndZ=0
    g9: LineSegment StartX=2.4e-15 StartY=2.25 StartZ=0 EndX=15 EndY=2.25 EndZ=0
    g10: LineSegment StartX=-20 StartY=10 StartZ=0 EndX=20 EndY=10 EndZ=0
    g11: LineSegment StartX=10 StartY=-10 StartZ=0 EndX=-30 EndY=-10 EndZ=0
    g12: LineSegment StartX=-20 StartY=10 StartZ=0 EndX=-20 EndY=38 EndZ=0
    g13: LineSegment StartX=-20 StartY=38 StartZ=0 EndX=-30 EndY=38 EndZ=0
    g14: LineSegment StartX=-30 StartY=38 StartZ=0 EndX=-30 EndY=10 EndZ=0
    g15: ArcOfCircle CenterX=10 CenterY=3.28e-13 CenterZ=0 NormalX=0 NormalY=0 NormalZ=1 AngleXU=0 Radius=10 StartAngle=4.71239 EndAngle=6.28319
    g16: GeomPoint X=20 Y=-10 Z=0
  constraints (44):
    c: Vertical(g0)
    c: DistanceX(g1,g16) = 50
    c: DistanceX(g-1,g16) = 20
    c: Tangent(g2,g5)
    c: Tangent(g2,g4)
    c: Tangent(g4,g3)
    c: Tangent(g5,g3)
    c: Horizontal(g4)
    c: Equal(g2,g3)
    c: PointOnObject(g2,g-1)
    c: Tangent(g6,g9)
    c: Tangent(g6,g8)
    c: Tangent(g8,g7)
    c: Tangent(g9,g7)
    c: Horizontal(g8)
    c: Equal(g6,g7)
    c: PointOnObject(g6,g-1)
    c: Equal(g6,g3)
    c: Equal(g5,g9)
    c: DistanceX(g9,g9) = 15
    c: DistanceX(g3,g6) = 10
    c: DistanceX(g7,g0) = 5
    c: Diameter(g2) = 4.5
    c: Coincident(g10,g0)
    c: Coincident(g11,g1)
    c: DistanceY(g16,g0) = 20
    c: Horizontal(g11)
    c: Horizontal(g10)
    c: Symmetric(g1,g1,g-1)
    c: Coincident(g12,g13)
    c: Coincident(g13,g14)
    c: Vertical(g14)
    c: Coincident(g14,g1)
    c: Vertical(g12)
    c: DistanceX(g13,g12) = 10
    c: Horizontal(g13)
    c: DistanceY(g-1,g13) = 38
    c: Coincident(g10,g12)
    c: Horizontal(g10,g1)
    c: PointOnObject(g16,g11)
    c: PointOnObject(g16,g0)
    c: Tangent(g11,g15) = 1.5708
    c: Tangent(g0,g15) = 1.5708
    c: Diameter(g15) = 20
FEATURE [PartDesign::Pad] Pad021
  BaseFeature = -> Pad018
  Direction = (1,1,1)
  Length = 10
  Length2 = 100
  Profile = -> Sketch036
  Reversed = true
  Type = 0
FEATURE [PartDesign::Pocket] Pocket013
  BaseFeature = -> Pad021
  Length = 2
  Length2 = 100
  Profile = -> Sketch032
  Reversed = true
  Type = 0
FEATURE [App::Link] BRACKET_MOTOR_J2_1_0001  label="J2_MTR_BRACKET"
  AssemblyType = Asm4EE
  AttachedBy = #LCS_0006
  AttachedTo = HUMERUS#plateJ1
  AttachmentOffset = pos=(-70,0,-6) rot=(0,0,1;0rad)
  LinkPlacement = pos=(53,28,159) rot=(0,0.707107,0.707107;3.14159rad)
  LinkedObject = -> BRACKET_MOTOR_J2_1_0
  Placement = pos=(53,28,159) rot=(0,0.707107,0.707107;3.14159rad)
  expr: Placement = HUMERUS.Placement * plateJ1.Placement * AttachmentOffset * LCS_0006.Placement ^ -1
FEATURE [App::Link] TENSIONER_J2001  label="J2-TENSIONER"
  AssemblyType = Asm4EE
  AttachedBy = #humerus002
  AttachedTo = HUMERUS#plateJ1
  AttachmentOffset = pos=(-143,0,0) rot=(0.707107,0.707107,0;3.14159rad)
  LinkPlacement = pos=(111,34,159) rot=(-1,0,0;4.71239rad)
  LinkedObject = -> TENSIONER_J2
  Placement = pos=(111,34,159) rot=(-1,0,0;4.71239rad)
  expr: Placement = HUMERUS.Placement * plateJ1.Placement * AttachmentOffset * humerus002.Placement ^ -1
FEATURE [PartDesign::CoordinateSystem] humerus002
  AttacherType = Attacher::AttachEngine3D
  MapMode = 11
  Placement = pos=(15,0,0) rot=(0,0,1;1.5708rad)
  Support = -> [Pad020]
FEATURE [App::Link] PULLEY_615432
  AssemblyType = Asm4EE
  AttachedBy = #LCS_1
  AttachedTo = BRACKET_MOTOR_J2_1_0001#motor001
  AttachmentOffset = pos=(0,0,7) rot=(0.707107,-0.707107,0;3.14159rad)
  LinkPlacement = pos=(39.5411,38.7738,194.959) rot=(-1,0,0;4.71239rad)
  LinkedObject = -> <external PULLEY-615432.FCStd>#_15432_assembly
  Placement = pos=(39.5411,38.7738,194.959) rot=(-1,0,0;4.71239rad)
  expr: Placement = BRACKET_MOTOR_J2_1_0001.Placement * motor001.Placement * AttachmentOffset * PULLEY_615432#LCS_1.Placement ^ -1
FEATURE [Sketcher::SketchObject] Sketch038
  FullyConstrained = true
  MapMode = 5
  Support = -> [XY_Plane018]
  sketch-geometry (2):
    g0: Circle CenterX=0 CenterY=0 CenterZ=0 NormalX=0 NormalY=0 NormalZ=1 AngleXU=0 Radius=26
    g1: Circle CenterX=0 CenterY=0 CenterZ=0 NormalX=0 NormalY=0 NormalZ=1 AngleXU=0 Radius=28
  constraints (4):
    c: Coincident(g0,g-1)
    c: Coincident(g1,g0)
    c: Diameter(g0) = 52
    c: Diameter(g1) = 56
FEATURE [Sketcher::SketchObject] Sketch039
  FullyConstrained = true
  MapMode = 5
  Support = -> [XY_Plane018]
  expr: Constraints[17] = <<var>>.humerusW
  expr: Constraints[16] = <<var>>.humerusW / 2
  sketch-geometry (9):
    g0: ArcOfCircle CenterX=0 CenterY=0 CenterZ=0 NormalX=0 NormalY=0 NormalZ=1 AngleXU=0 Radius=28 StartAngle=3.14159 EndAngle=6.28319
    g1: LineSegment StartX=-28 StartY=3.4e-15 StartZ=0 EndX=-28 EndY=-38.6375 EndZ=0
    g2: LineSegment StartX=-28 StartY=-38.6375 StartZ=0 EndX=28 EndY=-38.6375 EndZ=0
    g3: LineSegment StartX=28 StartY=-38.6375 StartZ=0 EndX=28 EndY=-7.1e-15 EndZ=0
    g4: Circle CenterX=-18 CenterY=-28.3187 CenterZ=0 NormalX=0 NormalY=0 NormalZ=1 AngleXU=0 Radius=2.25
    g5: Circle CenterX=18 CenterY=-28.3187 CenterZ=0 NormalX=0 NormalY=0 NormalZ=1 AngleXU=0 Radius=2.25
    g6: LineSegment StartX=-28 StartY=-18 StartZ=0 EndX=28 EndY=-18 EndZ=0
    g7: Circle CenterX=-18 CenterY=-28.3187 CenterZ=0 NormalX=0 NormalY=0 NormalZ=1 AngleXU=0 Radius=3.5
    g8: Circle CenterX=18 CenterY=-28.3187 CenterZ=0 NormalX=0 NormalY=0 NormalZ=1 AngleXU=0 Radius=3.5
  constraints (25):
    c: Coincident(g0,g-1)
    c: PointOnObject(g0,g-1)
    c: PointOnObject(g0,g-1)
    c: Coincident(g0,g1)
    c: Coincident(g1,g2)
    c: Horizontal(g2)
    c: Coincident(g2,g3)
    c: Coincident(g3,g0)
    c: Vertical(g3)
    c: Diameter(g0) = 56
    c: Vertical(g1)
    c: PointOnObject(g6,g1)
    c: PointOnObject(g6,g3)
    c: Horizontal(g6)
    c: Symmetric(g4,g5,g-2)
    c: DistanceX(g4,g5) = 36
    c: DistanceY(g4,g6) = 10.3187
    c: DistanceY(g1,g6) = 20.6375
    c: Diameter(g4) = 4.5
    c: Equal(g4,g5)
    c: DistanceY(g6,g0) = 18
    c: Coincident(g7,g4)
    c: Coincident(g8,g5)
    c: Diameter(g8) = 7
    c: Equal(g8,g7)
FEATURE [Sketcher::SketchObject] Sketch040
  FullyConstrained = true
  MapMode = 5
  Support = -> [XY_Plane018]
  sketch-geometry (2):
    g0: Circle CenterX=0 CenterY=0 CenterZ=0 NormalX=0 NormalY=0 NormalZ=1 AngleXU=0 Radius=9.55
    g1: Circle CenterX=0 CenterY=0 CenterZ=0 NormalX=0 NormalY=0 NormalZ=1 AngleXU=0 Radius=28
  constraints (4):
    c: Coincident(g0,g-1)
    c: Diameter(g0) = 19.1
    c: Coincident(g1,g0)
    c: Diameter(g1) = 56
FEATURE [PartDesign::Pad] Pad025
  AllowMultiFace = false
  Direction = (1,1,1)
  Length = 6
  Length2 = 100
  Profile = -> Sketch040
  Type = 0
FEATURE [PartDesign::Pad] Pad023
  AllowMultiFace = false
  BaseFeature = -> Pad025
  Direction = (1,1,1)
  Length = 15
  Length2 = 5
  Profile = -> Sketch038
  Type = 0
FEATURE [PartDesign::Pad] Pad024
  AllowMultiFace = false
  BaseFeature = -> Pad023
  Direction = (1,1,1)
  Length = 6
  Length2 = 5
  Profile = -> Sketch039
  Type = 0
FEATURE [Sketcher::SketchObject] Sketch041
  FullyConstrained = true
  MapMode = 5
  Placement = pos=(0,0,0) rot=(0.57735,0.57735,0.57735;2.0944rad)
  Support = -> [YZ_Plane018]
  sketch-geometry (3):
    g0: LineSegment StartX=9.55 StartY=0.866025 StartZ=0 EndX=10.05 EndY=0 EndZ=0
    g1: LineSegment StartX=9.55 StartY=0 StartZ=0 EndX=9.55 EndY=0.866025 EndZ=0
    g2: LineSegment StartX=9.55 StartY=0 StartZ=0 EndX=10.05 EndY=0 EndZ=0
  constraints (9):
    c: PointOnObject(g0,g-1)
    c: PointOnObject(g1,g-1)
    c: Vertical(g1)
    c: Coincident(g0,g1)
    c: Angle(g1,g0) = 0.523599
    c: Coincident(g2,g1)
    c: Coincident(g2,g0)
    c: DistanceX(g2,g2) = 0.5
    c: DistanceX(g-1,g1) = 9.55
FEATURE [PartDesign::Groove] Groove
  Angle = 360
  Axis = (-2e-16,3e-16,1)
  Base = (0,0,0)
  BaseFeature = -> Pad024
  Profile = -> Sketch041
  ReferenceAxis = -> Sketch041 [V_Axis]
FEATURE [PartDesign::CoordinateSystem] LCS_0009
  AttacherType = Attacher::AttachEngine3D
  MapMode = 2
  Support = -> [X_Axis019]
FEATURE [App::Link] BASE_J2_1_0001  label="J2-BASE"
  AssemblyType = Asm4EE
  AttachedBy = #humerus003
  AttachedTo = HUMERUS#baseJ2
  AttachmentOffset = pos=(0,0,0) rot=(0.707107,0.707107,0;3.14159rad)
  LinkPlacement = pos=(249.8,34,187.319) rot=(-1,0,0;4.71239rad)
  LinkedObject = -> BASE_J2_1_0
  Placement = pos=(249.8,34,187.319) rot=(-1,0,0;4.71239rad)
  expr: Placement = HUMERUS.Placement * baseJ2.Placement * AttachmentOffset * humerus003.Placement ^ -1
FEATURE [App::Link] BALL_6_19_6
  AssemblyType = Asm4EE
  AttachedBy = #LCS_0
  AttachedTo = BASE_J2_1_0001#LCS_0009
  LinkPlacement = pos=(249.8,34,187.319) rot=(-1,0,0;4.71239rad)
  LinkedObject = -> <external BALL-6-19-6.FCStd>#Part
  Placement = pos=(249.8,34,187.319) rot=(-1,0,0;4.71239rad)
  expr: Placement = BASE_J2_1_0001.Placement * LCS_0009.Placement * AttachmentOffset * BALL_6_19_6#LCS_0.Placement ^ -1
FEATURE [App::Link] WASHER_M6
  AssemblyType = Asm4EE
  AttachedBy = #LCS_1
  AttachedTo = BASE_J2_1_0001#LCS_0009
  LinkPlacement = pos=(249.8,35.6,187.319) rot=(-0.57735,-0.57735,0.57735;4.18879rad)
  LinkedObject = -> <external WASHER-M6.FCStd>#WASHER_M6
  Placement = pos=(249.8,35.6,187.319) rot=(-0.57735,-0.57735,0.57735;4.18879rad)
  expr: Placement = BASE_J2_1_0001.Placement * LCS_0009.Placement * AttachmentOffset * WASHER_M6#LCS_1.Placement ^ -1
FEATURE [App::Link] PULLEY_615433_1  label="PULLEY_615432_1"
  AssemblyType = Asm4EE
  AttachedBy = #LCS_1
  AttachedTo = BASE_J2_1_0001#LCS_0009
  AttachmentOffset = pos=(0,0,-1) rot=(0,0,1;0rad)
  LinkPlacement = pos=(263.259,38.7738,181.36) rot=(0,-0.707107,0.707107;3.14159rad)
  LinkedObject = -> <external PULLEY-615432.FCStd>#_15432_assembly
  Placement = pos=(263.259,38.7738,181.36) rot=(0,-0.707107,0.707107;3.14159rad)
  expr: Placement = BASE_J2_1_0001.Placement * LCS_0009.Placement * AttachmentOffset * PULLEY_615432#LCS_1.Placement ^ -1
FEATURE [Sketcher::SketchObject] Sketch042
  FullyConstrained = false
  MapMode = 5
  Support = -> [XY_Plane020]
  sketch-geometry (3):
    g0: Circle CenterX=0 CenterY=0 CenterZ=0 NormalX=0 NormalY=0 NormalZ=1 AngleXU=0 Radius=3
    g1: LineSegment StartX=-1.65831 StartY=2.5 StartZ=0 EndX=1.65831 EndY=2.5 EndZ=0
    g2: ArcOfCircle CenterX=0 CenterY=0 CenterZ=0 NormalX=0 NormalY=0 NormalZ=1 AngleXU=0 Radius=3 StartAngle=2.15648 EndAngle=7.2683
  constraints (8):
    c: Coincident(g0,g-1)
    c: Diameter(g0) = 6
    c: PointOnObject(g1,g0)
    c: Horizontal(g1)
    c: Coincident(g2,g-1)
    c: Coincident(g2,g1)
    c: Coincident(g2,g1)
    c: DistanceY(g-1,g1) = 2.5
FEATURE [PartDesign::Pad] Pad026
  Direction = (1,1,1)
  Length = 35
  Length2 = 100
  Profile = -> Sketch042
  Refine = true
  Type = 0
FEATURE [PartDesign::CoordinateSystem] LCS_1
  AttacherType = Attacher::AttachEngine3D
  MapMode = 5
  Placement = pos=(0,0,0) rot=(1,0,0;3.14159rad)
  Support = -> [Pad026]
FEATURE [PartDesign::CoordinateSystem] LCS_2
  AttacherType = Attacher::AttachEngine3D
  MapMode = 5
  Placement = pos=(0,0,35) rot=(0,0,1;0rad)
  Support = -> [Pad026]
FEATURE [PartDesign::Body] Body008  label="SHAFT_J2_1V0"
  Group = -> [Sketch042,Pad026,LCS_1,LCS_2]
  Origin = -> Origin020
  Tip = -> Pad026
FEATURE [App::Link] SHAFT_J2_1_0  label="J2-SHAFT"
  AssemblyType = Asm4EE
  AttachedBy = #LCS_2
  AttachedTo = HUB_545616_3#flatFace
  LinkPlacement = pos=(249.8,53,187.319) rot=(0,0.707107,-0.707107;3.14159rad)
  LinkedObject = -> Body008
  Placement = pos=(249.8,53,187.319) rot=(0,0.707107,-0.707107;3.14159rad)
  expr: Placement = HUB_545616_3.Placement * HUB_545616#flatFace.Placement * AttachmentOffset * LCS_2.Placement ^ -1
FEATURE [App::Link] HUB_545616_3  label="HUB_545616-J2"
  AssemblyType = Asm4EE
  AttachedBy = #flatFace
  AttachedTo = BALL_6808#LCS_0
  AttachmentOffset = pos=(0,0,7) rot=(0,0,1;3.14159rad)
  LinkPlacement = pos=(266.89,18.464,165.703) rot=(0.707107,0,-0.707107;3.14159rad)
  LinkedObject = -> <external HUB-545616.FCStd>#_45616_assembly
  Placement = pos=(266.89,18.464,165.703) rot=(0.707107,0,-0.707107;3.14159rad)
  expr: Placement = BALL_6808.Placement * BALL_6808#LCS_0.Placement * AttachmentOffset * HUB_545616#flatFace.Placement ^ -1
  expr: .AttachmentOffset.Rotation.Angle = <<var>>.angleJ2
FEATURE [App::Link] SCREW_M4X40_SCREW_M4X40
  AssemblyType = Asm4EE
  AttachedBy = #LCS_0
  AttachedTo = BRACKET_MOTOR_J2_1_0001#screw1
  LinkPlacement = pos=(81,25,159) rot=(0.57735,0.57735,-0.57735;4.18879rad)
  LinkedObject = -> <external SCREW-M4X40.FCStd>#SCREW_M4X40
  Placement = pos=(81,25,159) rot=(0.57735,0.57735,-0.57735;4.18879rad)
  expr: Placement = BRACKET_MOTOR_J2_1_0001.Placement * screw1.Placement * AttachmentOffset * SCREW_M4X40#LCS_0.Placement ^ -1
FEATURE [Sketcher::SketchObject] Sketch050
  FullyConstrained = true
  MapMode = 5
  Support = -> [XY_Plane024]
  expr: Constraints[39] = <<var>>.humerusW
  sketch-geometry (16):
    g0: LineSegment StartX=5.15937 StartY=-10.3187 StartZ=0 EndX=5.15937 EndY=10.3187 EndZ=0
    g1: LineSegment StartX=5.15937 StartY=10.3187 StartZ=0 EndX=-5.15937 EndY=10.3187 EndZ=0
    g2: LineSegment StartX=-5.15937 StartY=10.3187 StartZ=0 EndX=-5.15937 EndY=5.55625 EndZ=0
    g3: LineSegment StartX=-5.15937 StartY=5.55625 StartZ=0 EndX=-2.15937 EndY=5.55625 EndZ=0
    g4: LineSegment StartX=-2.15937 StartY=5.55625 StartZ=0 EndX=-2.15937 EndY=6.55625 EndZ=0
    g5: LineSegment StartX=-2.15937 StartY=6.55625 StartZ=0 EndX=-4.15937 EndY=6.55625 EndZ=0
    g6: LineSegment StartX=-4.15937 StartY=6.55625 StartZ=0 EndX=-4.15937 EndY=9.31875 EndZ=0
    g7: LineSegment StartX=-4.15937 StartY=9.31875 StartZ=0 EndX=3.63537 EndY=9.31875 EndZ=0
    g8: LineSegment StartX=3.63537 StartY=9.31875 StartZ=0 EndX=3.63537 EndY=-9.31875 EndZ=0
    g9: LineSegment StartX=3.63537 StartY=-9.31875 StartZ=0 EndX=-4.15937 EndY=-9.31875 EndZ=0
    g10: LineSegment StartX=-4.15937 StartY=-9.31875 StartZ=0 EndX=-4.15937 EndY=-6.55625 EndZ=0
    g11: LineSegment StartX=-4.15937 StartY=-6.55625 StartZ=0 EndX=-2.15937 EndY=-6.55625 EndZ=0
    g12: LineSegment StartX=-2.15937 StartY=-6.55625 StartZ=0 EndX=-2.15937 EndY=-5.55625 EndZ=0
    g13: LineSegment StartX=-2.15937 StartY=-5.55625 StartZ=0 EndX=-5.15937 EndY=-5.55625 EndZ=0
    g14: LineSegment StartX=-5.15937 StartY=-5.55625 StartZ=0 EndX=-5.15937 EndY=-10.3187 EndZ=0
    g15: LineSegment StartX=-5.15937 StartY=-10.3187 StartZ=0 EndX=5.15937 EndY=-10.3187 EndZ=0
  constraints (45):
    c: Coincident(g0,g1)
    c: Coincident(g1,g2)
    c: Vertical(g2)
    c: Coincident(g2,g3)
    c: Coincident(g3,g4)
    c: Coincident(g4,g5)
    c: Horizontal(g5)
    c: Coincident(g5,g6)
    c: Coincident(g6,g7)
    c: Horizontal(g7)
    c: Coincident(g7,g8)
    c: Vertical(g8)
    c: Coincident(g8,g9)
    c: Horizontal(g9)
    c: Coincident(g9,g10)
    c: Vertical(g10)
    c: Coincident(g10,g11)
    c: Horizontal(g11)
    c: Coincident(g11,g12)
    c: Vertical(g12)
    c: Coincident(g12,g13)
    c: Horizontal(g13)
    c: Coincident(g13,g14)
    c: Vertical(g14)
    c: Coincident(g14,g15)
    c: Coincident(g15,g0)
    c: DistanceX(g7,g0) = 1.524
    c: DistanceY(g6,g1) = 1
    c: Vertical(g6)
    c: Horizontal(g3)
    c: Vertical(g4)
    c: DistanceY(g4,g4) = 1
    c: DistanceX(g2,g5) = 1
    c: Symmetric(g2,g13,g-1)
    c: Equal(g3,g13)
    c: Equal(g12,g4)
    c: Equal(g2,g14)
    c: Equal(g10,g6)
    c: Equal(g11,g5)
    c: DistanceY(g0,g0) = 20.6375
    c: DistanceX(g15,g15) = 10.3187
    c: DistanceY(g13,g2) = 11.1125
    c: Symmetric(g1,g0,g-2)
    c: Symmetric(g0,g0,g-1)
    c: DistanceX(g3,g3) = 3
FEATURE [PartDesign::Pad] Pad031
  AllowMultiFace = false
  Direction = (1,1,1)
  Length = 304.8
  Length2 = 100
  Profile = -> Sketch050
  Type = 0
FEATURE [Sketcher::SketchObject] Sketch049
  ExternalGeometry = -> [Pad031]
  FullyConstrained = true
  MapMode = 5
  Placement = pos=(5.15937,0,0) rot=(0.57735,0.57735,0.57735;2.0944rad)
  Support = -> [Pad031]
  sketch-geometry (4):
    g0: Circle CenterX=0 CenterY=10 CenterZ=0 NormalX=0 NormalY=0 NormalZ=1 AngleXU=0 Radius=2.25
    g1: Circle CenterX=0 CenterY=34 CenterZ=0 NormalX=0 NormalY=0 NormalZ=1 AngleXU=0 Radius=2.25
    g2: Circle CenterX=0 CenterY=294.8 CenterZ=0 NormalX=0 NormalY=0 NormalZ=1 AngleXU=0 Radius=2.25
    g3: Circle CenterX=0 CenterY=262.8 CenterZ=0 NormalX=0 NormalY=0 NormalZ=1 AngleXU=0 Radius=2.25
  constraints (12):
    c: PointOnObject(g0,g-2)
    c: PointOnObject(g1,g-2)
    c: Equal(g1,g0)
    c: DistanceY(g0,g1) = 24
    c: DistanceY(g-1,g0) = 10
    c: PointOnObject(g3,g-2)
    c: Diameter(g2) = 4.5
    c: Equal(g2,g3)
    c: PointOnObject(g2,g-2)
    c: DistanceY(g3,g2) = 32
    c: DistanceY(g2,g-3) = 10
    c: Equal(g1,g2)
FEATURE [PartDesign::Pocket] Pocket016
  AllowMultiFace = false
  BaseFeature = -> Pad031
  Length = 5
  Length2 = 100
  Profile = -> Sketch049
  Type = 0
FEATURE [PartDesign::Body] Body011  label="RADIUS_1_0"
  Group = -> [Sketch050,Pad031,Sketch049,Pocket016]
  Origin = -> Origin024
  Tip = -> Pocket016
FEATURE [Sketcher::SketchObject] Sketch051
  FullyConstrained = true
  MapMode = 5
  Support = -> [XY_Plane025]
  expr: Constraints[17] = <<var>>.humerusW / 2
  expr: Constraints[14] = <<var>>.humerusW
  sketch-geometry (36):
    g0: ArcOfCircle CenterX=0 CenterY=0 CenterZ=0 NormalX=0 NormalY=0 NormalZ=1 AngleXU=0 Radius=9.5 StartAngle=1.75606 EndAngle=2.95632
    g1: LineSegment StartX=-29 StartY=-39.6375 StartZ=0 EndX=13 EndY=-39.6375 EndZ=0
    g2: LineSegment StartX=18 StartY=-34.6375 StartZ=0 EndX=18 EndY=-19 EndZ=0
    g3: Circle CenterX=8 CenterY=-29.3188 CenterZ=0 NormalX=0 NormalY=0 NormalZ=1 AngleXU=0 Radius=1.7
    g4: LineSegment StartX=-34 StartY=-19 StartZ=0 EndX=66 EndY=-19 EndZ=0
    g5: LineSegment StartX=66 StartY=-19 StartZ=0 EndX=66 EndY=-39.6375 EndZ=0
    g6: LineSegment StartX=66 StartY=-39.6375 StartZ=0 EndX=-34 EndY=-39.6375 EndZ=0
    g7: LineSegment StartX=-34 StartY=-39.6375 StartZ=0 EndX=-34 EndY=-19 EndZ=0
    g8: LineSegment StartX=-34 StartY=-34.6375 StartZ=0 EndX=-34 EndY=5 EndZ=0
    g9: Circle CenterX=-24 CenterY=-29.3188 CenterZ=0 NormalX=0 NormalY=0 NormalZ=1 AngleXU=0 Radius=1.7
    g10: Circle CenterX=0 CenterY=0 CenterZ=0 NormalX=0 NormalY=0 NormalZ=1 AngleXU=0 Radius=11
    g11: LineSegment StartX=-11 StartY=1.8e-15 StartZ=0 EndX=0 EndY=11 EndZ=0
    g12: LineSegment StartX=0 StartY=11 StartZ=0 EndX=11 EndY=-1.8e-15 EndZ=0
    g13: LineSegment StartX=11 StartY=-1.1e-15 StartZ=0 EndX=0 EndY=-11 EndZ=0
    g14: LineSegment StartX=0 StartY=-11 StartZ=0 EndX=-11 EndY=1.8e-15 EndZ=0
    g15: ArcOfCircle CenterX=-11 CenterY=1.8e-15 CenterZ=0 NormalX=0 NormalY=0 NormalZ=1 AngleXU=0 Radius=1.75 StartAngle=1.5708 EndAngle=4.71239
    g16: ArcOfCircle CenterX=11 CenterY=-1.1e-15 CenterZ=0 NormalX=0 NormalY=0 NormalZ=1 AngleXU=0 Radius=1.75 StartAngle=4.71239 EndAngle=7.85398
    g17: LineSegment StartX=-11 StartY=-1.75 StartZ=0 EndX=-9.33742 EndY=-1.75 EndZ=0
    g18: LineSegment StartX=-11 StartY=1.75 StartZ=0 EndX=-9.33742 EndY=1.75 EndZ=0
    g19: ArcOfCircle CenterX=0 CenterY=-11 CenterZ=0 NormalX=0 NormalY=0 NormalZ=1 AngleXU=0 Radius=1.75 StartAngle=3.14159 EndAngle=6.28319
    g20: ArcOfCircle CenterX=0 CenterY=11 CenterZ=0 NormalX=0 NormalY=0 NormalZ=1 AngleXU=0 Radius=1.75 StartAngle=-9e-16 EndAngle=3.14159
    g21: LineSegment StartX=1.75 StartY=-11 StartZ=0 EndX=1.75 EndY=-9.33742 EndZ=0
    g22: LineSegment StartX=-1.75 StartY=-11 StartZ=0 EndX=-1.75 EndY=-9.33742 EndZ=0
    g23: LineSegment StartX=9.33742 StartY=1.75 StartZ=0 EndX=11 EndY=1.75 EndZ=0
    g24: LineSegment StartX=-1.75 StartY=9.33742 StartZ=0 EndX=-1.75 EndY=11 EndZ=0
    g25: LineSegment StartX=1.75 StartY=9.33742 StartZ=0 EndX=1.75 EndY=11 EndZ=0
    g26: LineSegment StartX=9.33742 StartY=-1.75 StartZ=0 EndX=11 EndY=-1.75 EndZ=0
    g27: ArcOfCircle CenterX=0 CenterY=0 CenterZ=0 NormalX=0 NormalY=0 NormalZ=1 AngleXU=0 Radius=9.5 StartAngle=3.32686 EndAngle=4.52712
    g28: ArcOfCircle CenterX=0 CenterY=0 CenterZ=0 NormalX=0 NormalY=0 NormalZ=1 AngleXU=0 Radius=9.5 StartAngle=4.89766 EndAngle=6.09792
    g29: ArcOfCircle CenterX=0 CenterY=0 CenterZ=0 NormalX=0 NormalY=0 NormalZ=1 AngleXU=0 Radius=9.5 StartAngle=0.185269 EndAngle=1.38553
    g30: ArcOfCircle CenterX=0 CenterY=0 CenterZ=0 NormalX=0 NormalY=0 NormalZ=1 AngleXU=0 Radius=18 StartAngle=0 EndAngle=1.97606
    g31: LineSegment StartX=-7.09677 StartY=16.5419 StartZ=0 EndX=-34 EndY=5 EndZ=0
    g32: LineSegment StartX=18 StartY=0 StartZ=0 EndX=18 EndY=-19 EndZ=0
    g33: ArcOfCircle CenterX=-29 CenterY=-34.6375 CenterZ=0 NormalX=0 NormalY=0 NormalZ=1 AngleXU=0 Radius=5 StartAngle=3.14159 EndAngle=4.71239
    g34: ArcOfCircle CenterX=13 CenterY=-34.6375 CenterZ=0 NormalX=0 NormalY=0 NormalZ=1 AngleXU=0 Radius=5 StartAngle=4.71239 EndAngle=6.28319
    g35: Circle CenterX=0 CenterY=0 CenterZ=0 NormalX=0 NormalY=0 NormalZ=1 AngleXU=0 Radius=17.272
  constraints (91):
    c: Coincident(g0,g-1)
    c: Diameter(g0) = 19
    c: Horizontal(g1)
    c: Vertical(g2)
    c: Diameter(g3) = 3.4
    c: Coincident(g4,g5)
    c: Coincident(g5,g6)
    c: Coincident(g6,g7)
    c: Coincident(g7,g4)
    c: Horizontal(g4)
    c: Horizontal(g6)
    c: Vertical(g5)
    c: Vertical(g7)
    c: DistanceY(g4,g-1) = 19
    c: DistanceY(g5,g5) = 20.6375
    c: PointOnObject(g2,g4)
    c: DistanceX(g6,g6) = 100
    c: DistanceY(g3,g2) = 10.3187
    c: Equal(g9,g3)
    c: DistanceX(g9,g3) = 32
    c: DistanceX(g6,g9) = 10
    c: Horizontal(g9,g3)
    c: Coincident(g10,g0)
    c: Coincident(g11,g12)
    c: Coincident(g12,g13)
    c: Coincident(g13,g14)
    c: Coincident(g14,g11)
    c: Diameter(g10) = 22
    c: Tangent(g15,g18)
    c: Tangent(g15,g17)
    c: Equal(g15,g16)
    c: Coincident(g15,g11)
    c: Coincident(g16,g12)
    c: PointOnObject(g16,g10)
    c: PointOnObject(g15,g10)
    c: PointOnObject(g11,g10)
    c: Equal(g12,g11)
    c: Diameter(g15) = 3.5
    c: Tangent(g19,g22)
    c: Tangent(g19,g21)
    c: Equal(g19,g20)
    c: Coincident(g19,g13)
    c: Coincident(g20,g11)
    c: Equal(g20,g15)
    c: Tangent(g18,g23)
    c: Tangent(g22,g24)
    c: Tangent(g21,g25)
    c: Tangent(g17,g26)
    c: Equal(g0,g27)
    c: Coincident(g0,g27)
    c: Equal(g27,g28)
    c: Coincident(g27,g28)
    c: Equal(g28,g29)
    c: Coincident(g28,g29)
    c: Tangent(g25,g20) = -1.5708
    c: Tangent(g24,g20) = 1.5708
    c: Tangent(g23,g16) = 1.5708
    c: Tangent(g26,g16) = -1.5708
    c: Coincident(g30,g0)
    c: PointOnObject(g30,g-1)
    c: Diameter(g30) = 36
    c: Tangent(g31,g30) = -1.5708
    c: Coincident(g32,g30)
    c: Coincident(g32,g2)
    c: Vertical(g32)
    c: Coincident(g22,g27)
    c: Coincident(g28,g21)
    c: Coincident(g26,g28)
    c: Coincident(g23,g29)
    c: Coincident(g25,g29)
    c: Coincident(g24,g0)
    c: Coincident(g18,g0)
    c: Coincident(g17,g27)
    c: Tangent(g8,g33) = 1.5708
    c: Tangent(g1,g33) = -1.5708
    c: Tangent(g2,g34) = -1.5708
    c: Tangent(g1,g34) = -1.5708
    c: Equal(g34,g33)
    c: Vertical(g8)
    c: PointOnObject(g1,g6)
    c: Diameter(g33) = 10
    c: DistanceX(g3,g2) = 10
    c: Coincident(g35,g0)
    c: Diameter(g35) = 34.544
    c: DistanceX(g8,g9) = 10
    c: Coincident(g8,g31)
    c: DistanceY(g-1,g8) = 5
    c: Perpendicular(g14,g11)
    c: Perpendicular(g12,g13)
    c: Perpendicular(g12,g11)
    c: PointOnObject(g20,g-2)
FEATURE [PartDesign::Pad] Pad032
  Direction = (1,1,1)
  Length = 5
  Length2 = 100
  Profile = -> Sketch051
  Type = 0
FEATURE [App::Link] MOTOR_11HS12_0674S_PG27_E22_300
  AssemblyType = Asm4EE
  AttachedBy = #mount
  AttachedTo = J3_BASE#motor004
  AttachmentOffset = pos=(0,0,0) rot=(0,0,-1;0.785398rad)
  LinkPlacement = pos=(514.6,82,176.3) rot=(-0.57735,-0.57735,0.57735;4.18879rad)
  LinkedObject = -> <external MOTOR-11HS12-0674S-PG27-E22-300.FCStd>#Body
  Placement = pos=(514.6,82,176.3) rot=(-0.57735,-0.57735,0.57735;4.18879rad)
  expr: Placement = J3_BASE.Placement * motor004.Placement * AttachmentOffset * MOTOR_11HS12_0674S_PG27_E22_300#mount.Placement ^ -1
FEATURE [TechDraw::DrawSVGTemplate] Template
  EditableTexts = AUTHOR_NAME=CARL WINGE; DRAWING_TITLE=A4 Riser; PN=RISER-1.0
  Height = 215.9
  Orientation = 1
  Width = 279.4
FEATURE [TechDraw::DrawProjGroupItem] ProjItem  label="Bottom"
  CoarseView = false
  Direction = (0,0,1)
  Focus = 100
  HardHidden = false
  IsoCount = 0
  IsoHidden = false
  IsoVisible = false
  LockPosition = true
  Perspective = false
  Rotation = 0
  RotationVector = (1,0,0)
  ScaleType = 2
  SeamHidden = false
  SeamVisible = true
  SmoothHidden = false
  SmoothVisible = true
  Source = -> [PolarPattern]
  Type = 0
  X = 0
  XDirection = (1,0,0)
  Y = 0
FEATURE [TechDraw::DrawProjGroup] ProjGroup
  Anchor = -> ProjItem
  AutoDistribute = true
  LockPosition = false
  ProjectionType = 1
  Rotation = 0
  ScaleType = 0
  Source = -> [PolarPattern]
  Views = -> [ProjItem]
  X = 139.7
  Y = 107.95
  spacingX = 15
  spacingY = 15
FEATURE [TechDraw::DrawViewDimension] Dimension002
  Arbitrary = false
  ArbitraryTolerances = false
  EqualTolerance = false
  FormatSpec = ⌀%.1f
  FormatSpecOverTolerance = %+.1f
  FormatSpecUnderTolerance = %+.1f
  Inverted = false
  LockPosition = false
  MeasureType = 1
  OverTolerance = 0
  References2D = -> [ProjItem]
  Rotation = 0
  ScaleType = 0
  TheoreticalExact = false
  Type = 5
  UnderTolerance = 0
  X = 9.47475
  Y = 19.8267
FEATURE [TechDraw::DrawSVGTemplate] Template001
  EditableTexts = AUTHOR_NAME=CARL WINGE; DRAWING_TITLE=HUMERUS; PN=HUMERUS-1.0
  Height = 215.9
  Orientation = 1
  Width = 279.4
FEATURE [App::Link] BELT_XL_180_375_BELT_XL_130_375  label="BELT_XL_18IN_3_8"
  AssemblyType = Asm4EE
  AttachedBy = #LCS_1
  AttachedTo = PULLEY_615433_1#LCS_1
  AttachmentOffset = pos=(0,0,-2) rot=(-1,0,0;3.14159rad)
  LinkPlacement = pos=(249.8,37,187.319) rot=(0,0.707107,0.707107;3.14159rad)
  LinkedObject = -> <external BELT-XL-180-375.FCStd>#Body
  Placement = pos=(249.8,37,187.319) rot=(0,0.707107,0.707107;3.14159rad)
  expr: Placement = PULLEY_615433_1.Placement * PULLEY_615432#LCS_1.Placement * AttachmentOffset * BELT_XL_180_375#LCS_1.Placement ^ -1
FEATURE [TechDraw::DrawSVGTemplate] Template002
  EditableTexts = AUTHOR_NAME=CARL WINGE; DRAWING_TITLE=Radius; PN=RADIUS-1.0
  Height = 215.9
  Orientation = 1
  Width = 279.4
FEATURE [PartDesign::CoordinateSystem] LCS_0010
  AttacherType = Attacher::AttachEngine3D
  MapMode = 2
  Support = -> [X_Axis030]
FEATURE [TechDraw::DrawProjGroupItem] ProjItem002  label="Front001"
  CoarseView = false
  Direction = (1,0,0)
  Focus = 100
  HardHidden = false
  IsoCount = 0
  IsoHidden = false
  IsoVisible = false
  LockPosition = true
  Perspective = false
  Rotation = 0
  RotationVector = (0,1,0)
  Scale = 0.666667
  ScaleType = 2
  SeamHidden = false
  SeamVisible = true
  SmoothHidden = false
  SmoothVisible = true
  Source = -> [Pocket016]
  Type = 0
  X = 0
  XDirection = (0,1e-16,1)
  Y = 0
FEATURE [TechDraw::DrawProjGroup] ProjGroup002
  Anchor = -> ProjItem002
  AutoDistribute = true
  LockPosition = false
  ProjectionType = 1
  Rotation = 0
  Scale = 0.666667
  ScaleType = 2
  Source = -> [Pocket016]
  Views = -> [ProjItem002]
  X = 144.063
  Y = 107.95
  spacingX = 15
  spacingY = 15
FEATURE [TechDraw::DrawViewDimension] Dimension015
  Arbitrary = false
  ArbitraryTolerances = false
  EqualTolerance = false
  FormatSpec = %.1f
  FormatSpecOverTolerance = %+.1f
  FormatSpecUnderTolerance = %+.1f
  Inverted = false
  LockPosition = false
  MeasureType = 1
  OverTolerance = 0
  References2D = -> [ProjItem002]
  Rotation = 0
  ScaleType = 0
  TheoreticalExact = false
  Type = 1
  UnderTolerance = 0
  X = -85.7643
  Y = 16.3097
FEATURE [TechDraw::DrawViewDimension] Dimension016
  Arbitrary = false
  ArbitraryTolerances = false
  EqualTolerance = false
  FormatSpec = %.1f
  FormatSpecOverTolerance = %+.1f
  FormatSpecUnderTolerance = %+.1f
  Inverted = false
  LockPosition = false
  MeasureType = 1
  OverTolerance = 0
  References2D = -> [ProjItem002]
  Rotation = 0
  ScaleType = 0
  TheoreticalExact = false
  Type = 2
  UnderTolerance = 0
  X = -111.505
  Y = -14.2108
FEATURE [TechDraw::DrawViewDimension] Dimension017
  Arbitrary = false
  ArbitraryTolerances = false
  EqualTolerance = false
  FormatSpec = %.1f
  FormatSpecOverTolerance = %+.1f
  FormatSpecUnderTolerance = %+.1f
  Inverted = false
  LockPosition = false
  MeasureType = 1
  OverTolerance = 0
  References2D = -> [ProjItem002]
  Rotation = 0
  ScaleType = 0
  TheoreticalExact = false
  Type = 2
  UnderTolerance = 0
  X = -122.56
  Y = 0
FEATURE [TechDraw::DrawViewDimension] Dimension018
  Arbitrary = false
  ArbitraryTolerances = false
  EqualTolerance = false
  FormatSpec = %.1f
  FormatSpecOverTolerance = %+.1f
  FormatSpecUnderTolerance = %+.1f
  Inverted = false
  LockPosition = false
  MeasureType = 1
  OverTolerance = 0
  References2D = -> [ProjItem002]
  Rotation = 0
  ScaleType = 0
  TheoreticalExact = false
  Type = 1
  UnderTolerance = 0
  X = -86.4969
  Y = 26.238
FEATURE [TechDraw::DrawViewDimension] Dimension019
  Arbitrary = false
  ArbitraryTolerances = false
  EqualTolerance = false
  FormatSpec = %.1f
  FormatSpecOverTolerance = %+.1f
  FormatSpecUnderTolerance = %+.1f
  Inverted = false
  LockPosition = false
  MeasureType = 1
  OverTolerance = 0
  References2D = -> [ProjItem002]
  Rotation = 0
  ScaleType = 0
  TheoreticalExact = false
  Type = 1
  UnderTolerance = 0
  X = 1.10315
  Y = 39.2383
FEATURE [TechDraw::DrawViewDimension] Dimension020
  Arbitrary = false
  ArbitraryTolerances = false
  EqualTolerance = false
  FormatSpec = %.1f
  FormatSpecOverTolerance = %+.1f
  FormatSpecUnderTolerance = %+.1f
  Inverted = false
  LockPosition = false
  MeasureType = 1
  OverTolerance = 0
  References2D = -> [ProjItem002]
  Rotation = 0
  ScaleType = 0
  TheoreticalExact = false
  Type = 1
  UnderTolerance = 0
  X = 84.2935
  Y = 16.3097
FEATURE [TechDraw::DrawViewDimension] Dimension021
  Arbitrary = false
  ArbitraryTolerances = false
  EqualTolerance = false
  FormatSpec = %.1f
  FormatSpecOverTolerance = %+.1f
  FormatSpecUnderTolerance = %+.1f
  Inverted = false
  LockPosition = false
  MeasureType = 1
  OverTolerance = 0
  References2D = -> [ProjItem002]
  Rotation = 0
  ScaleType = 0
  TheoreticalExact = false
  Type = 1
  UnderTolerance = 0
  X = 87.6
  Y = 26.6058
FEATURE [TechDraw::DrawViewDimension] Dimension022
  Arbitrary = false
  ArbitraryTolerances = false
  EqualTolerance = false
  FormatSpec = ⌀%.1f
  FormatSpecOverTolerance = %+.1f
  FormatSpecUnderTolerance = %+.1f
  Inverted = false
  LockPosition = false
  MeasureType = 1
  OverTolerance = 0
  References2D = -> [ProjItem002]
  Rotation = 0
  ScaleType = 0
  TheoreticalExact = false
  Type = 5
  UnderTolerance = 0
  X = -73.7281
  Y = -13.0878
FEATURE [TechDraw::DrawPage] Page002
  KeepUpdated = true
  NextBalloonIndex = 1
  ProjectionType = 1
  Template = -> Template002
  Views = -> [ProjGroup002,Dimension015,Dimension016,Dimension017,Dimension018,Dimension019,Dimension020,Dimension021,Dimension022]
FEATURE [Sketcher::SketchObject] Sketch065
  FullyConstrained = true
  MapMode = 5
  Placement = pos=(0,0,0) rot=(1,0,0;1.5708rad)
  Support = -> [XZ_Plane019]
  sketch-geometry (4):
    g0: LineSegment StartX=9.55 StartY=6 StartZ=0 EndX=7.55 EndY=8 EndZ=0
    g1: LineSegment StartX=7.55 StartY=8 StartZ=0 EndX=12.55 EndY=8 EndZ=0
    g2: LineSegment StartX=12.55 StartY=8 StartZ=0 EndX=12.55 EndY=6 EndZ=0
    g3: LineSegment StartX=12.55 StartY=6 StartZ=0 EndX=9.55 EndY=6 EndZ=0
  constraints (12):
    c: Coincident(g0,g1)
    c: Horizontal(g1)
    c: Coincident(g1,g2)
    c: Vertical(g2)
    c: Coincident(g2,g3)
    c: Coincident(g3,g0)
    c: Horizontal(g3)
    c: DistanceX(g-1,g0) = 9.55
    c: DistanceY(g2,g2) = 2
    c: DistanceY(g-1,g2) = 6
    c: Angle(g0,g1) = 0.785398
    c: DistanceX(g3,g3) = 3
FEATURE [PartDesign::Revolution] Revolution
  Angle = 360
  Axis = (0,-2e-16,1)
  Base = (0,0,0)
  BaseFeature = -> Groove
  Profile = -> Sketch065
  ReferenceAxis = -> Sketch065 [V_Axis]
  Reversed = true
FEATURE [PartDesign::CoordinateSystem] LCS_0011
  AttacherType = Attacher::AttachEngine3D
  MapMode = 2
  Support = -> [X_Axis031]
FEATURE [PartDesign::CoordinateSystem] LCS_0012
  AttacherType = Attacher::AttachEngine3D
  MapMode = 2
  Support = -> [X_Axis032]
FEATURE [Sketcher::SketchObject] Sketch067
  FullyConstrained = true
  MapMode = 5
  Support = -> [XY_Plane032]
  sketch-geometry (6):
    g0: Circle CenterX=0 CenterY=19 CenterZ=0 NormalX=0 NormalY=0 NormalZ=1 AngleXU=0 Radius=2.25
    g1: Circle CenterX=0 CenterY=-19 CenterZ=0 NormalX=0 NormalY=0 NormalZ=1 AngleXU=0 Radius=2.25
    g2: ArcOfCircle CenterX=0 CenterY=0 CenterZ=0 NormalX=0 NormalY=0 NormalZ=1 AngleXU=0 Radius=23.5 StartAngle=1.13125 EndAngle=2.01035
    g3: ArcOfCircle CenterX=0 CenterY=0 CenterZ=0 NormalX=0 NormalY=0 NormalZ=1 AngleXU=0 Radius=23.5 StartAngle=4.27284 EndAngle=5.15194
    g4: LineSegment StartX=-10 StartY=21.2662 StartZ=0 EndX=-10 EndY=-21.2662 EndZ=0
    g5: LineSegment StartX=10 StartY=-21.2662 StartZ=0 EndX=10 EndY=21.2662 EndZ=0
  constraints (16):
    c: PointOnObject(g0,g-2)
    c: Diameter(g1) = 4.5
    c: Equal(g1,g0)
    c: DistanceY(g1,g0) = 38
    c: Symmetric(g0,g1,g-1)
    c: Coincident(g2,g-1)
    c: Coincident(g3,g2)
    c: Coincident(g4,g3)
    c: Coincident(g5,g3)
    c: Coincident(g5,g2)
    c: Coincident(g2,g4)
    c: Vertical(g4)
    c: Symmetric(g2,g3,g-1)
    c: Horizontal(g2,g2)
    c: DistanceX(g2,g2) = 20
    c: Diameter(g2) = 47
FEATURE [PartDesign::Pad] Pad043
  Direction = (1,1,1)
  Length = 15
  Length2 = 100
  Profile = -> Sketch067
  Type = 0
FEATURE [Sketcher::SketchObject] Sketch068
  FullyConstrained = true
  MapMode = 5
  Placement = pos=(0,0,0) rot=(1,0,0;1.5708rad)
  Support = -> [XZ_Plane032]
  sketch-geometry (5):
    g0: Circle CenterX=0 CenterY=26 CenterZ=0 NormalX=0 NormalY=0 NormalZ=1 AngleXU=0 Radius=10
    g1: ArcOfCircle CenterX=0 CenterY=26 CenterZ=0 NormalX=0 NormalY=0 NormalZ=1 AngleXU=0 Radius=12 StartAngle=6.08159 EndAngle=9.62637
    g2: LineSegment StartX=-11.757 StartY=23.5973 StartZ=0 EndX=-10 EndY=15 EndZ=0
    g3: LineSegment StartX=11.757 StartY=23.5973 StartZ=0 EndX=10 EndY=15 EndZ=0
    g4: LineSegment StartX=10 StartY=15 StartZ=0 EndX=-10 EndY=15 EndZ=0
  constraints (12):
    c: PointOnObject(g0,g-2)
    c: Diameter(g0) = 20
    c: Coincident(g1,g0)
    c: Coincident(g4,g3)
    c: Coincident(g4,g2)
    c: Symmetric(g2,g3,g-2)
    c: DistanceX(g4,g4) = 20
    c: DistanceY(g-1,g3) = 15
    c: Diameter(g1) = 24
    c: DistanceY(g-1,g0) = 26
    c: Tangent(g2,g1) = -1.5708
    c: Tangent(g3,g1) = 1.5708
FEATURE [PartDesign::Pad] Pad044
  BaseFeature = -> Pad043
  Direction = (1,1,1)
  Length = 10
  Length2 = 100
  Midplane = true
  Profile = -> Sketch068
  Type = 0
FEATURE [Sketcher::SketchObject] Sketch069
  FullyConstrained = true
  MapMode = 5
  Placement = pos=(0,0,0) rot=(0.57735,0.57735,0.57735;2.0944rad)
  Support = -> [YZ_Plane032]
  expr: Constraints[9] = <<var>>.humerusW + 2
  sketch-geometry (4):
    g0: LineSegment StartX=-11.3187 StartY=0 StartZ=0 EndX=11.3187 EndY=0 EndZ=0
    g1: LineSegment StartX=11.3187 StartY=0 StartZ=0 EndX=11.3187 EndY=11 EndZ=0
    g2: LineSegment StartX=11.3187 StartY=11 StartZ=0 EndX=-11.3187 EndY=11 EndZ=0
    g3: LineSegment StartX=-11.3187 StartY=11 StartZ=0 EndX=-11.3187 EndY=0 EndZ=0
  constraints (11):
    c: Coincident(g0,g1)
    c: Coincident(g1,g2)
    c: Coincident(g2,g3)
    c: Coincident(g3,g0)
    c: Horizontal(g0)
    c: Vertical(g1)
    c: Vertical(g3)
    c: PointOnObject(g0,g-1)
    c: Symmetric(g2,g1,g-2)
    c: DistanceX(g2,g2) = 22.6375
    c: DistanceY(g1,g1) = 11
FEATURE [PartDesign::Pocket] Pocket022
  BaseFeature = -> Pad044
  Length = 5
  Length2 = 100
  Midplane = true
  Profile = -> Sketch069
  Type = 1
FEATURE [PartDesign::Body] J2_CABLE_GUIDE_1_0  label="Body008"
  Group = -> [LCS_0012,Sketch067,Pad043,Sketch068,Pad044,Sketch069,Pocket022]
  Origin = -> Origin032
  Tip = -> Pocket022
FEATURE [App::Part] A4_J2_CABLE_GUIDE  label="J2_CABLE_GUIDE_1V0"
  Group = -> [LCS_0011,J2_CABLE_GUIDE_1_0]
  Origin = -> Origin031
FEATURE [App::Link] MOTOR_17HS13_0404S_PG27_0
  AssemblyType = Asm4EE
  AttachedBy = #LCS_0
  AttachedTo = BASE_J0_1_0001#LCS_0001
  LinkPlacement = pos=(0,0,75) rot=(0,0,1;1.5708rad)
  LinkedObject = -> <external MOTOR-17HS13-0404S-PG27.FCStd>#Part
  Placement = pos=(0,0,75) rot=(0,0,1;1.5708rad)
  expr: Placement = BASE_J0_1_0001.Placement * LCS_0001.Placement * AttachmentOffset * MOTOR_17HS13_0404S_PG27#LCS_0.Placement ^ -1
FEATURE [App::Link] BALL_6810_0
  AssemblyType = Asm4EE
  AttachedBy = #LCS_0
  AttachedTo = BASE_J0_1_0001#LCS_0001
  AttachmentOffset = pos=(0,0,8) rot=(0,0,1;0rad)
  LinkPlacement = pos=(0,0,83) rot=(0,0,1;1.5708rad)
  LinkedObject = -> <external BALL-6810.FCStd>#Part
  Placement = pos=(0,0,83) rot=(0,0,1;1.5708rad)
  expr: Placement = BASE_J0_1_0001.Placement * LCS_0001.Placement * AttachmentOffset * BALL_6810#LCS_0.Placement ^ -1
FEATURE [Sketcher::SketchObject] Sketch070
  AttachmentOffset = pos=(0,0,5) rot=(0,0,1;0rad)
  FullyConstrained = true
  MapMode = 5
  Placement = pos=(0,0,5) rot=(0,0,1;0rad)
  Support = -> [XY_Plane004]
  expr: .AttachmentOffset.Base.z = 5
  sketch-geometry (2):
    g0: Circle CenterX=0 CenterY=0 CenterZ=0 NormalX=0 NormalY=0 NormalZ=1 AngleXU=0 Radius=28.75
    g1: Circle CenterX=0 CenterY=0 CenterZ=0 NormalX=0 NormalY=0 NormalZ=1 AngleXU=0 Radius=32.6
  constraints (4):
    c: Coincident(g0,g-1)
    c: Coincident(g1,g0)
    c: Diameter(g1) = 65.2
    c: Diameter(g0) = 57.5
FEATURE [PartDesign::Pad] Pad045
  BaseFeature = -> Pad006
  Direction = (1,1,1)
  Length = 3
  Length2 = 100
  Profile = -> Sketch070
  Refine = true
  Type = 0
FEATURE [PartDesign::Hole] Hole
  BaseFeature = -> Pad007
  Depth = 25
  DepthType = 1
  Diameter = 4.3
  DrillForDepth = false
  DrillPoint = 1
  DrillPointAngle = 118
  HoleCutCountersinkAngle = 82
  HoleCutCustomValues = false
  HoleCutDepth = 0
  HoleCutDiameter = 8.298
  HoleCutType = 2
  ModelActualThread = false
  Profile = -> Sketch012
  Refine = true
  Tapered = false
  TaperedAngle = 90
  ThreadAngle = 0
  ThreadClass = 0
  ThreadCutOffInner = 0
  ThreadCutOffOuter = 0
  ThreadDirection = 0
  ThreadFit = 0
  ThreadPitch = 0
  ThreadSize = 5
  ThreadType = 3
  Threaded = false
FEATURE [Sketcher::SketchObject] Sketch071
  FullyConstrained = true
  MapMode = 5
  Support = -> [XY_Plane004]
  sketch-geometry (7):
    g0: LineSegment StartX=-6 StartY=-33 StartZ=0 EndX=5 EndY=-33 EndZ=0
    g1: LineSegment StartX=5 StartY=-33 StartZ=0 EndX=5 EndY=-51 EndZ=0
    g2: LineSegment StartX=5 StartY=-51 StartZ=0 EndX=-6 EndY=-51 EndZ=0
    g3: LineSegment StartX=-6 StartY=-51 StartZ=0 EndX=-6 EndY=-33 EndZ=0
    g4: Circle CenterX=0 CenterY=0 CenterZ=0 NormalX=0 NormalY=0 NormalZ=1 AngleXU=0 Radius=33
    g5: Circle CenterX=0 CenterY=-38 CenterZ=0 NormalX=0 NormalY=0 NormalZ=1 AngleXU=0 Radius=1.0922
    g6: Circle CenterX=0 CenterY=-46 CenterZ=0 NormalX=0 NormalY=0 NormalZ=1 AngleXU=0 Radius=1.0922
  constraints (21):
    c: Coincident(g0,g1)
    c: Coincident(g1,g2)
    c: Coincident(g2,g3)
    c: Coincident(g3,g0)
    c: Horizontal(g0)
    c: Vertical(g1)
    c: Vertical(g3)
    c: DistanceY(g1,g1) = 18
    c: Coincident(g4,g-1)
    c: Diameter(g4) = 66
    c: Tangent(g0,g4)
    c: PointOnObject(g5,g-2)
    c: PointOnObject(g6,g-2)
    c: Diameter(g6) = 2.1844
    c: Equal(g6,g5)
    c: DistanceY(g6,g5) = 8
    c: DistanceY(g5,g0) = 5
    c: DistanceY(g1,g6) = 5
    c: DistanceX(g-1,g1) = 5
    c: DistanceX(g2,g-1) = 6
    c: Horizontal(g2)
FEATURE [PartDesign::Pad] Pad046
  BaseFeature = -> Pad045
  Direction = (1,1,1)
  Length = 25.5
  Length2 = 100
  Profile = -> Sketch071
  Type = 0
  expr: Length = Variables.encoderJ0H
FEATURE [Sketcher::SketchObject] Sketch072
  FullyConstrained = true
  MapMode = 5
  Support = -> [XY_Plane034]
  sketch-geometry (14):
    g0: LineSegment StartX=-7 StartY=-51 StartZ=0 EndX=5 EndY=-51 EndZ=0
    g1: LineSegment StartX=5 StartY=-51 StartZ=0 EndX=5 EndY=-21 EndZ=0
    g2: LineSegment StartX=5 StartY=-5 StartZ=0 EndX=-7 EndY=-5 EndZ=0
    g3: LineSegment StartX=-7 StartY=-5 StartZ=0 EndX=-7 EndY=-51 EndZ=0
    g4: LineSegment StartX=-3 StartY=4 StartZ=0 EndX=3 EndY=4 EndZ=0
    g5: LineSegment StartX=3 StartY=4 StartZ=0 EndX=3 EndY=-21 EndZ=0
    g6: LineSegment StartX=3 StartY=-21 StartZ=0 EndX=-3 EndY=-21 EndZ=0
    g7: LineSegment StartX=-3 StartY=-21 StartZ=0 EndX=-3 EndY=4 EndZ=0
    g8: Circle CenterX=0 CenterY=-10 CenterZ=0 NormalX=0 NormalY=0 NormalZ=1 AngleXU=0 Radius=1.32
    g9: LineSegment StartX=-3 StartY=-13.5 StartZ=0 EndX=5 EndY=-13.5 EndZ=0
    g10: LineSegment StartX=5 StartY=-21 StartZ=0 EndX=-3 EndY=-21 EndZ=0
    g11: LineSegment StartX=-3 StartY=-21 StartZ=0 EndX=-3 EndY=-13.5 EndZ=0
    g12: Circle CenterX=0 CenterY=0 CenterZ=0 NormalX=0 NormalY=0 NormalZ=1 AngleXU=0 Radius=33
    g13: LineSegment StartX=5 StartY=-13.5 StartZ=0 EndX=5 EndY=-5 EndZ=0
  constraints (39):
    c: Coincident(g0,g1)
    c: Coincident(g13,g2)
    c: Coincident(g2,g3)
    c: Coincident(g3,g0)
    c: Horizontal(g0)
    c: Vertical(g1)
    c: Vertical(g3)
    c: DistanceY(g0,g-1) = 51
    c: Coincident(g4,g5)
    c: Coincident(g5,g6)
    c: Coincident(g6,g7)
    c: Coincident(g7,g4)
    c: Horizontal(g6)
    c: Vertical(g5)
    c: Vertical(g7)
    c: DistanceY(g5,g5) = 25
    c: Symmetric(g4,g4,g-2)
    c: DistanceX(g4,g4) = 6
    c: PointOnObject(g8,g-2)
    c: Diameter(g8) = 2.64
    c: DistanceY(g8,g4) = 14
    c: Coincident(g10,g11)
    c: Coincident(g11,g9)
    c: Horizontal(g10)
    c: Vertical(g11)
    c: DistanceY(g10,g9) = 7.5
    c: Coincident(g12,g-1)
    c: Diameter(g12) = 66
    c: Horizontal(g2)
    c: DistanceX(g-1,g13) = 5
    c: DistanceY(g8,g13) = 5
    c: DistanceY(g-1,g4) = 4
    c: DistanceX(g2,g9) = 4
    c: DistanceX(g10,g-1) = 3
    c: Coincident(g1,g10)
    c: Coincident(g13,g9)
    c: Tangent(g1,g13)
    c: Horizontal(g9)
    c: Horizontal(g1,g5)
FEATURE [Sketcher::SketchObject] Sketch073
  FullyConstrained = true
  MapMode = 5
  Support = -> [XY_Plane034]
  sketch-geometry (6):
    g0: LineSegment StartX=-6 StartY=4 StartZ=0 EndX=6 EndY=4 EndZ=0
    g1: LineSegment StartX=6 StartY=4 StartZ=0 EndX=6 EndY=-21 EndZ=0
    g2: LineSegment StartX=6 StartY=-21 StartZ=0 EndX=-3 EndY=-21 EndZ=0
    g3: LineSegment StartX=-3 StartY=-21 StartZ=0 EndX=-3 EndY=-8 EndZ=0
    g4: ArcOfCircle CenterX=-6 CenterY=-8 CenterZ=0 NormalX=0 NormalY=0 NormalZ=1 AngleXU=0 Radius=3 StartAngle=0 EndAngle=1.5708
    g5: LineSegment StartX=-6 StartY=-5 StartZ=0 EndX=-6 EndY=4 EndZ=0
  constraints (19):
    c: Coincident(g0,g1)
    c: Coincident(g1,g2)
    c: Coincident(g2,g3)
    c: Horizontal(g0)
    c: Horizontal(g2)
    c: Vertical(g1)
    c: Vertical(g3)
    c: DistanceY(g-1,g0) = 4
    c: DistanceX(g-1,g0) = 6
    c: DistanceY(g3,g0) = 25
    c: Coincident(g3,g4)
    c: Vertical(g4,g4)
    c: Horizontal(g4,g3)
    c: Diameter(g4) = 6
    c: DistanceX(g3,g-1) = 3
    c: Coincident(g5,g4)
    c: Coincident(g5,g0)
    c: Vertical(g5)
    c: DistanceY(g5,g5) = 9
FEATURE [PartDesign::CoordinateSystem] LCS_0013
  AttacherType = Attacher::AttachEngine3D
  MapMode = 2
  Support = -> [X_Axis033]
FEATURE [PartDesign::CoordinateSystem] LCS_0014
  AttacherType = Attacher::AttachEngine3D
  MapMode = 2
  Support = -> [X_Axis034]
FEATURE [PartDesign::Pad] Pad047
  Direction = (1,1,1)
  Length = 9
  Length2 = 100
  Profile = -> Sketch072
  Type = 0
FEATURE [PartDesign::Pocket] Pocket023
  BaseFeature = -> Pad047
  Length = 1.6
  Length2 = 100
  Profile = -> Sketch073
  Reversed = true
  Type = 0
FEATURE [Sketcher::SketchObject] Sketch074
  AttachmentOffset = pos=(0,0,9) rot=(0,0,1;0rad)
  FullyConstrained = true
  MapMode = 5
  Placement = pos=(0,0,9) rot=(0,0,1;0rad)
  Support = -> [XY_Plane034]
  sketch-geometry (2):
    g0: Circle CenterX=0 CenterY=-38 CenterZ=0 NormalX=0 NormalY=0 NormalZ=1 AngleXU=0 Radius=1.5
    g1: Circle CenterX=0 CenterY=-46 CenterZ=0 NormalX=0 NormalY=0 NormalZ=1 AngleXU=0 Radius=1.5
  constraints (6):
    c: PointOnObject(g0,g-2)
    c: PointOnObject(g1,g-2)
    c: Diameter(g1) = 3
    c: Equal(g1,g0)
    c: DistanceY(g1,g0) = 8
    c: DistanceY(g0,g-1) = 38
FEATURE [PartDesign::Hole] Hole001
  BaseFeature = -> Pocket023
  Depth = 25
  DepthType = 1
  Diameter = 3.3
  DrillForDepth = false
  DrillPoint = 1
  DrillPointAngle = 118
  HoleCutCountersinkAngle = 82
  HoleCutCustomValues = false
  HoleCutDepth = 0
  HoleCutDiameter = 6
  HoleCutType = 2
  ModelActualThread = false
  Profile = -> Sketch074
  Tapered = false
  TaperedAngle = 90
  ThreadAngle = 0
  ThreadClass = 0
  ThreadCutOffInner = 0
  ThreadCutOffOuter = 0
  ThreadDirection = 0
  ThreadFit = 0
  ThreadPitch = 0
  ThreadSize = 3
  ThreadType = 3
  Threaded = false
FEATURE [PartDesign::Body] Body_3
  Group = -> [LCS_0014,Sketch072,Sketch073,Pad047,Pocket023,Sketch074,Hole001]
  Origin = -> Origin034
  Tip = -> Hole001
FEATURE [App::Part] ENCODER_BRACKET_1_0  label="ENCODER_BRACKET_1V0"
  Group = -> [LCS_0013,Body_3]
  Origin = -> Origin033
FEATURE [App::Link] ENCODER_BRACKET_0
  AssemblyType = Asm4EE
  AttachedBy = #LCS_0013
  AttachedTo = BASE_J0_1_0001#LCS_0001
  AttachmentOffset = pos=(0,0,25.5) rot=(0,0,1;0rad)
  LinkPlacement = pos=(0,0,100.5) rot=(0,0,1;1.5708rad)
  LinkedObject = -> ENCODER_BRACKET_1_0
  Placement = pos=(0,0,100.5) rot=(0,0,1;1.5708rad)
  expr: .AttachmentOffset.Base.z = Variables.encoderJ0H
  expr: Placement = BASE_J0_1_0001.Placement * LCS_0001.Placement * AttachmentOffset * LCS_0013.Placement ^ -1
FEATURE [Sketcher::SketchObject] Sketch075
  AttachmentOffset = pos=(0,0,4.5) rot=(0,0,1;0rad)
  FullyConstrained = true
  MapMode = 5
  Placement = pos=(0,0,4.5) rot=(0,0,1;0rad)
  Support = -> [XY_Plane006]
  sketch-geometry (1):
    g0: Circle CenterX=0 CenterY=0 CenterZ=0 NormalX=0 NormalY=0 NormalZ=1 AngleXU=0 Radius=4
  constraints (2):
    c: Coincident(g0,g-1)
    c: Diameter(g0) = 8
FEATURE [PartDesign::Pad] Pad048
  BaseFeature = -> Hole
  Direction = (1,1,1)
  Length = 1
  Length2 = 100
  Profile = -> Sketch075
  Type = 0
FEATURE [Sketcher::SketchObject] Sketch076
  AttachmentOffset = pos=(0,0,-4) rot=(0,0,1;0rad)
  FullyConstrained = true
  MapMode = 5
  Placement = pos=(0,4,9e-16) rot=(1,0,0;1.5708rad)
  Support = -> [XZ_Plane008]
  expr: Constraints[3] = Variables.baseJ1MotorH
  sketch-geometry (2):
    g0: Circle CenterX=0 CenterY=43 CenterZ=0 NormalX=0 NormalY=0 NormalZ=1 AngleXU=0 Radius=28.75
    g1: Circle CenterX=0 CenterY=43 CenterZ=0 NormalX=0 NormalY=0 NormalZ=1 AngleXU=0 Radius=32.6
  constraints (5):
    c: PointOnObject(g0,g-2)
    c: Coincident(g1,g0)
    c: Diameter(g1) = 65.2
    c: DistanceY(g-1,g0) = 43
    c: Diameter(g0) = 57.5
FEATURE [PartDesign::Pad] Pad049
  BaseFeature = -> Pocket006
  Direction = (1,1,1)
  Length = 4
  Length2 = 100
  Profile = -> Sketch076
  Reversed = true
  Type = 0
FEATURE [PartDesign::CoordinateSystem] motor
  AttacherType = Attacher::AttachEngine3D
  MapMode = 11
  Placement = pos=(0,-9.5e-15,43) rot=(0.57735,-0.57735,0.57735;2.0944rad)
  Support = -> [Pad049]
FEATURE [App::Link] MOTOR_17HS13_0404S_PG27_1
  AssemblyType = Asm4EE
  AttachedBy = #LCS_0
  AttachedTo = BASE_J1_1_0001#motor
  AttachmentOffset = pos=(0,0,0) rot=(1,0,0;3.14159rad)
  LinkPlacement = pos=(4.4e-15,10,141) rot=(-0.57735,-0.57735,-0.57735;2.0944rad)
  LinkedObject = -> <external MOTOR-17HS13-0404S-PG27.FCStd>#Part
  Placement = pos=(4.4e-15,10,141) rot=(-0.57735,-0.57735,-0.57735;2.0944rad)
  expr: Placement = BASE_J1_1_0001.Placement * motor.Placement * AttachmentOffset * MOTOR_17HS13_0404S_PG27#LCS_0.Placement ^ -1
FEATURE [App::Link] BALL_6810_1
  AssemblyType = Asm4EE
  AttachedBy = #LCS_0
  AttachedTo = BASE_J1_1_0001#motor
  AttachmentOffset = pos=(0,0,-16) rot=(0,0,1;-1.5708rad)
  LinkPlacement = pos=(1.33e-14,26,141) rot=(1,0,0;1.5708rad)
  LinkedObject = -> <external BALL-6810.FCStd>#Part
  Placement = pos=(1.33e-14,26,141) rot=(1,0,0;1.5708rad)
  expr: .AttachmentOffset.Rotation.Angle = <<var>>.angleJ1
  expr: Placement = BASE_J1_1_0001.Placement * motor.Placement * AttachmentOffset * BALL_6810#LCS_0.Placement ^ -1
FEATURE [Sketcher::SketchObject] Sketch079
  AttachmentOffset = pos=(0,0,5) rot=(0,0,1;0rad)
  FullyConstrained = true
  MapMode = 5
  Placement = pos=(0,0,5) rot=(0,0,1;0rad)
  Support = -> [XY_Plane004]
  sketch-geometry (9):
    g0: Circle CenterX=0 CenterY=0 CenterZ=0 NormalX=0 NormalY=0 NormalZ=1 AngleXU=0 Radius=14
    g1: LineSegment StartX=-9.89949 StartY=9.89949 StartZ=0 EndX=9.89949 EndY=9.89949 EndZ=0
    g2: LineSegment StartX=9.89949 StartY=9.89949 StartZ=0 EndX=9.89949 EndY=-9.89949 EndZ=0
    g3: LineSegment StartX=9.89949 StartY=-9.89949 StartZ=0 EndX=-9.89949 EndY=-9.89949 EndZ=0
    g4: LineSegment StartX=-9.89949 StartY=-9.89949 StartZ=0 EndX=-9.89949 EndY=9.89949 EndZ=0
    g5: Circle CenterX=-9.89949 CenterY=9.89949 CenterZ=0 NormalX=0 NormalY=0 NormalZ=1 AngleXU=0 Radius=1.5
    g6: Circle CenterX=9.89949 CenterY=9.89949 CenterZ=0 NormalX=0 NormalY=0 NormalZ=1 AngleXU=0 Radius=1.5
    g7: Circle CenterX=9.89949 CenterY=-9.89949 CenterZ=0 NormalX=0 NormalY=0 NormalZ=1 AngleXU=0 Radius=1.5
    g8: Circle CenterX=-9.89949 CenterY=-9.89949 CenterZ=0 NormalX=0 NormalY=0 NormalZ=1 AngleXU=0 Radius=1.5
  constraints (22):
    c: Coincident(g0,g-1)
    c: Coincident(g1,g2)
    c: Coincident(g2,g3)
    c: Coincident(g3,g4)
    c: Coincident(g4,g1)
    c: Horizontal(g1)
    c: Horizontal(g3)
    c: Vertical(g2)
    c: Vertical(g4)
    c: PointOnObject(g1,g0)
    c: PointOnObject(g2,g0)
    c: PointOnObject(g1,g0)
    c: Equal(g1,g4)
    c: Diameter(g0) = 28
    c: Coincident(g5,g1)
    c: Coincident(g6,g1)
    c: Coincident(g7,g2)
    c: Coincident(g8,g3)
    c: Diameter(g8) = 3
    c: Equal(g8,g7)
    c: Equal(g8,g6)
    c: Equal(g8,g5)
FEATURE [PartDesign::Hole] Hole002
  BaseFeature = -> Pad046
  Depth = 25
  DepthType = 1
  Diameter = 3.4
  DrillForDepth = false
  DrillPoint = 1
  DrillPointAngle = 118
  HoleCutCountersinkAngle = 90
  HoleCutCustomValues = false
  HoleCutDepth = 0
  HoleCutDiameter = 6.7
  HoleCutType = 7
  ModelActualThread = false
  Profile = -> Sketch079
  Tapered = false
  TaperedAngle = 90
  ThreadAngle = 0
  ThreadClass = 0
  ThreadCutOffInner = 0
  ThreadCutOffOuter = 0
  ThreadDirection = 0
  ThreadFit = 0
  ThreadPitch = 0
  ThreadSize = 9
  ThreadType = 1
  Threaded = false
FEATURE [PartDesign::Body] Body001
  Group = -> [Sketch004,Pad005,Sketch005,Pad006,Sketch070,Pad045,Sketch071,Pad046,Sketch079,Hole002]
  Origin = -> Origin004
  Tip = -> Hole002
FEATURE [App::Part] BASE_J0_1_0  label="J0_BASE_2V0"
  Group = -> [LCS_0001,Body001]
  Origin = -> Origin003
FEATURE [Sketcher::SketchObject] Sketch080
  AttachmentOffset = pos=(0,0,4.5) rot=(0,0,1;0rad)
  FullyConstrained = true
  MapMode = 5
  Placement = pos=(0,0,4.5) rot=(0,0,1;0rad)
  Support = -> [XY_Plane036]
  sketch-geometry (1):
    g0: Circle CenterX=0 CenterY=0 CenterZ=0 NormalX=0 NormalY=0 NormalZ=1 AngleXU=0 Radius=4
  constraints (2):
    c: Coincident(g0,g-1)
    c: Diameter(g0) = 8
FEATURE [Sketcher::SketchObject] Sketch081
  FullyConstrained = true
  MapMode = 5
  Support = -> [XY_Plane036]
  sketch-geometry (6):
    g0: Circle CenterX=-18 CenterY=18 CenterZ=0 NormalX=0 NormalY=0 NormalZ=1 AngleXU=0 Radius=1.7272
    g1: Circle CenterX=17 CenterY=18 CenterZ=0 NormalX=0 NormalY=0 NormalZ=1 AngleXU=0 Radius=1.7272
    g2: LineSegment StartX=-27 StartY=8 StartZ=0 EndX=27 EndY=8 EndZ=0
    g3: LineSegment StartX=-27 StartY=0 StartZ=0 EndX=-27 EndY=28 EndZ=0
    g4: LineSegment StartX=-27 StartY=28 StartZ=0 EndX=27 EndY=28 EndZ=0
    g5: LineSegment StartX=27 StartY=28 StartZ=0 EndX=27 EndY=0 EndZ=0
  constraints (19):
    c: DistanceX(g0,g1) = 35
    c: Horizontal(g2)
    c: DistanceY(g-1,g2) = 8
    c: Equal(g0,g1)
    c: Diameter(g0) = 3.4544
    c: PointOnObject(g3,g-1)
    c: Vertical(g3)
    c: Coincident(g3,g4)
    c: Coincident(g4,g5)
    c: PointOnObject(g5,g-1)
    c: Vertical(g5)
    c: Symmetric(g3,g4,g-2)
    c: PointOnObject(g2,g5)
    c: PointOnObject(g2,g3)
    c: DistanceX(g4,g4) = 54
    c: DistanceY(g5,g5) = 28
    c: DistanceY(g2,g1) = 10
    c: DistanceX(g1,g4) = 10
    c: Horizontal(g0,g1)
FEATURE [Sketcher::SketchObject] Sketch083
  FullyConstrained = true
  MapMode = 5
  Support = -> [XY_Plane036]
  sketch-geometry (2):
    g0: Circle CenterX=0 CenterY=0 CenterZ=0 NormalX=0 NormalY=0 NormalZ=1 AngleXU=0 Radius=3.1
    g1: Circle CenterX=0 CenterY=0 CenterZ=0 NormalX=0 NormalY=0 NormalZ=1 AngleXU=0 Radius=27
  constraints (4):
    c: Diameter(g0) = 6.2
    c: Coincident(g0,g-1)
    c: Coincident(g1,g0)
    c: Diameter(g1) = 54
FEATURE [PartDesign::Pad] Pad050
  AllowMultiFace = false
  Direction = (1,1,1)
  Length = 8
  Length2 = 100
  Profile = -> Sketch083
  Type = 0
FEATURE [Sketcher::SketchObject] Sketch084
  AttachmentOffset = pos=(0,0,8) rot=(0,0,1;0rad)
  FullyConstrained = true
  MapMode = 5
  Placement = pos=(0,0,8) rot=(0,0,1;0rad)
  Support = -> [XY_Plane036]
  sketch-geometry (8):
    g0: LineSegment StartX=-8 StartY=8 StartZ=0 EndX=8 EndY=8 EndZ=0
    g1: LineSegment StartX=8 StartY=8 StartZ=0 EndX=8 EndY=-8 EndZ=0
    g2: LineSegment StartX=8 StartY=-8 StartZ=0 EndX=-8 EndY=-8 EndZ=0
    g3: LineSegment StartX=-8 StartY=-8 StartZ=0 EndX=-8 EndY=8 EndZ=0
    g4: Circle CenterX=-8 CenterY=8 CenterZ=0 NormalX=0 NormalY=0 NormalZ=1 AngleXU=0 Radius=2.25
    g5: Circle CenterX=8 CenterY=8 CenterZ=0 NormalX=0 NormalY=0 NormalZ=1 AngleXU=0 Radius=2.25
    g6: Circle CenterX=8 CenterY=-8 CenterZ=0 NormalX=0 NormalY=0 NormalZ=1 AngleXU=0 Radius=2.25
    g7: Circle CenterX=-8 CenterY=-8 CenterZ=0 NormalX=0 NormalY=0 NormalZ=1 AngleXU=0 Radius=2.25
  constraints (18):
    c: Coincident(g0,g1)
    c: Coincident(g1,g2)
    c: Coincident(g2,g3)
    c: Coincident(g3,g0)
    c: Horizontal(g2)
    c: Vertical(g1)
    c: Symmetric(g0,g0,g-2)
    c: Symmetric(g0,g2,g-1)
    c: Equal(g3,g0)
    c: Coincident(g4,g0)
    c: Coincident(g5,g0)
    c: Coincident(g6,g1)
    c: Coincident(g7,g2)
    c: Diameter(g4) = 4.5
    c: Equal(g4,g7)
    c: Equal(g4,g6)
    c: Equal(g4,g5)
    c: DistanceY(g1,g1) = 16
FEATURE [PartDesign::Hole] Hole003
  BaseFeature = -> Pad050
  Depth = 25
  DepthType = 1
  Diameter = 4.5
  DrillForDepth = false
  DrillPoint = 1
  DrillPointAngle = 118
  HoleCutCountersinkAngle = 90
  HoleCutCustomValues = false
  HoleCutDepth = 0
  HoleCutDiameter = 9
  HoleCutType = 7
  ModelActualThread = false
  Profile = -> Sketch084
  Refine = true
  Tapered = false
  TaperedAngle = 90
  ThreadAngle = 0
  ThreadClass = 0
  ThreadCutOffInner = 0
  ThreadCutOffOuter = 0
  ThreadDirection = 0
  ThreadFit = 0
  ThreadPitch = 0
  ThreadSize = 11
  ThreadType = 1
  Threaded = false
FEATURE [PartDesign::Pad] Pad051
  BaseFeature = -> Hole003
  Direction = (1,1,1)
  Length = 1
  Length2 = 100
  Profile = -> Sketch080
  Type = 0
FEATURE [PartDesign::CoordinateSystem] LCS_0015
  AttacherType = Attacher::AttachEngine3D
  MapMode = 2
  Support = -> [X_Axis035]
FEATURE [Sketcher::SketchObject] Sketch085
  AttachmentOffset = pos=(0,0,1) rot=(0,0,1;0rad)
  FullyConstrained = true
  MapMode = 5
  Placement = pos=(0,0,1) rot=(0,0,1;0rad)
  Support = -> [XY_Plane036]
  sketch-geometry (7):
    g0: LineSegment StartX=-27 StartY=0 StartZ=0 EndX=-27 EndY=28 EndZ=0
    g1: LineSegment StartX=-27 StartY=28 StartZ=0 EndX=27 EndY=28 EndZ=0
    g2: LineSegment StartX=27 StartY=28 StartZ=0 EndX=27 EndY=0 EndZ=0
    g3: LineSegment StartX=27 StartY=0 StartZ=0 EndX=25 EndY=0 EndZ=0
    g4: LineSegment StartX=-25 StartY=3.1e-15 StartZ=0 EndX=-27 EndY=0 EndZ=0
    g5: ArcOfCircle CenterX=0 CenterY=0 CenterZ=0 NormalX=0 NormalY=0 NormalZ=1 AngleXU=0 Radius=25 StartAngle=0 EndAngle=3.14159
    g6: LineSegment StartX=-27 StartY=8 StartZ=0 EndX=27 EndY=8 EndZ=0
  constraints (21):
    c: PointOnObject(g0,g-1)
    c: Vertical(g0)
    c: Coincident(g1,g0)
    c: Coincident(g2,g1)
    c: PointOnObject(g2,g-1)
    c: Coincident(g3,g2)
    c: PointOnObject(g3,g-1)
    c: PointOnObject(g4,g-1)
    c: Coincident(g4,g0)
    c: Coincident(g5,g-1)
    c: Coincident(g5,g4)
    c: Coincident(g5,g3)
    c: Vertical(g2)
    c: DistanceX(g1,g1) = 54
    c: Symmetric(g0,g1,g-2)
    c: Diameter(g5) = 50
    c: PointOnObject(g6,g0)
    c: PointOnObject(g6,g2)
    c: Horizontal(g6)
    c: DistanceY(g6,g1) = 20
    c: DistanceY(g-1,g6) = 8
FEATURE [PartDesign::Pad] Pad052
  BaseFeature = -> Pad051
  Direction = (1,1,1)
  Length = 7
  Length2 = 100
  Profile = -> Sketch085
  Refine = true
  Type = 0
FEATURE [PartDesign::Pocket] Pocket026
  BaseFeature = -> Pad052
  Length = 5
  Length2 = 100
  Profile = -> Sketch081
  Refine = true
  Reversed = true
  Type = 1
FEATURE [PartDesign::CoordinateSystem] baseJ004  label="humerus"
  AttacherType = Attacher::AttachEngine3D
  MapMode = 11
  Placement = pos=(17,18,8) rot=(0.707107,-0.707107,0;3.14159rad)
  Support = -> [Pocket026]
FEATURE [PartDesign::Body] Body017
  Group = -> [Sketch083,Pad050,Sketch084,Hole003,Sketch080,Pad051,Sketch081,Sketch085,Pad052,Pocket026]
  Origin = -> Origin035
  Tip = -> Pocket026
FEATURE [App::Part] PLATE_J0_1_0002  label="J1_PLATE_2V0"
  Group = -> [LCS_0015,Body017,baseJ004]
  Origin = -> Origin036
FEATURE [App::Link] J1_PLATE
  AssemblyType = Asm4EE
  AttachedBy = #LCS_0015
  AttachedTo = BALL_6810_1#LCS_0
  AttachmentOffset = pos=(0,0,0) rot=(0,-1,0;3.14159rad)
  LinkPlacement = pos=(1.33e-14,26,141) rot=(0,-0.707107,-0.707107;3.14159rad)
  LinkedObject = -> PLATE_J0_1_0002
  Placement = pos=(1.33e-14,26,141) rot=(0,-0.707107,-0.707107;3.14159rad)
  expr: Placement = BALL_6810_1.Placement * BALL_6810#LCS_0.Placement * AttachmentOffset * LCS_0015.Placement ^ -1
FEATURE [Sketcher::SketchObject] Sketch086
  FullyConstrained = true
  MapMode = 5
  Support = -> [XY_Plane013]
  expr: Constraints[39] = <<var>>.humerusW
  sketch-geometry (16):
    g0: LineSegment StartX=5.15937 StartY=-10.3187 StartZ=0 EndX=5.15937 EndY=10.3187 EndZ=0
    g1: LineSegment StartX=5.15937 StartY=10.3187 StartZ=0 EndX=-5.15937 EndY=10.3187 EndZ=0
    g2: LineSegment StartX=-5.15937 StartY=10.3187 StartZ=0 EndX=-5.15937 EndY=5.55625 EndZ=0
    g3: LineSegment StartX=-5.15937 StartY=5.55625 StartZ=0 EndX=-2.15937 EndY=5.55625 EndZ=0
    g4: LineSegment StartX=-2.15937 StartY=5.55625 StartZ=0 EndX=-2.15937 EndY=6.55625 EndZ=0
    g5: LineSegment StartX=-2.15937 StartY=6.55625 StartZ=0 EndX=-4.15937 EndY=6.55625 EndZ=0
    g6: LineSegment StartX=-4.15937 StartY=6.55625 StartZ=0 EndX=-4.15937 EndY=9.31875 EndZ=0
    g7: LineSegment StartX=-4.15937 StartY=9.31875 StartZ=0 EndX=3.63537 EndY=9.31875 EndZ=0
    g8: LineSegment StartX=3.63537 StartY=9.31875 StartZ=0 EndX=3.63537 EndY=-9.31875 EndZ=0
    g9: LineSegment StartX=3.63537 StartY=-9.31875 StartZ=0 EndX=-4.15937 EndY=-9.31875 EndZ=0
    g10: LineSegment StartX=-4.15937 StartY=-9.31875 StartZ=0 EndX=-4.15937 EndY=-6.55625 EndZ=0
    g11: LineSegment StartX=-4.15937 StartY=-6.55625 StartZ=0 EndX=-2.15937 EndY=-6.55625 EndZ=0
    g12: LineSegment StartX=-2.15937 StartY=-6.55625 StartZ=0 EndX=-2.15937 EndY=-5.55625 EndZ=0
    g13: LineSegment StartX=-2.15937 StartY=-5.55625 StartZ=0 EndX=-5.15937 EndY=-5.55625 EndZ=0
    g14: LineSegment StartX=-5.15937 StartY=-5.55625 StartZ=0 EndX=-5.15937 EndY=-10.3187 EndZ=0
    g15: LineSegment StartX=-5.15937 StartY=-10.3187 StartZ=0 EndX=5.15937 EndY=-10.3187 EndZ=0
  constraints (45):
    c: Coincident(g0,g1)
    c: Coincident(g1,g2)
    c: Vertical(g2)
    c: Coincident(g2,g3)
    c: Coincident(g3,g4)
    c: Coincident(g4,g5)
    c: Horizontal(g5)
    c: Coincident(g5,g6)
    c: Coincident(g6,g7)
    c: Horizontal(g7)
    c: Coincident(g7,g8)
    c: Vertical(g8)
    c: Coincident(g8,g9)
    c: Horizontal(g9)
    c: Coincident(g9,g10)
    c: Vertical(g10)
    c: Coincident(g10,g11)
    c: Horizontal(g11)
    c: Coincident(g11,g12)
    c: Vertical(g12)
    c: Coincident(g12,g13)
    c: Horizontal(g13)
    c: Coincident(g13,g14)
    c: Vertical(g14)
    c: Coincident(g14,g15)
    c: Coincident(g15,g0)
    c: DistanceX(g7,g0) = 1.524
    c: DistanceY(g6,g1) = 1
    c: Vertical(g6)
    c: Horizontal(g3)
    c: Vertical(g4)
    c: DistanceY(g4,g4) = 1
    c: DistanceX(g2,g5) = 1
    c: Symmetric(g2,g13,g-1)
    c: Equal(g3,g13)
    c: Equal(g12,g4)
    c: Equal(g2,g14)
    c: Equal(g10,g6)
    c: Equal(g11,g5)
    c: DistanceY(g0,g0) = 20.6375
    c: DistanceX(g15,g15) = 10.3187
    c: DistanceY(g13,g2) = 11.1125
    c: Symmetric(g1,g0,g-2)
    c: Symmetric(g0,g0,g-1)
    c: DistanceX(g3,g3) = 3
FEATURE [PartDesign::Pad] Pad053
  Direction = (1,1,1)
  Length = 304.8
  Length2 = 100
  Profile = -> Sketch086
  Refine = true
  Type = 0
FEATURE [Sketcher::SketchObject] Sketch087
  FullyConstrained = true
  MapMode = 5
  Placement = pos=(0,0,0) rot=(0.57735,0.57735,0.57735;2.0944rad)
  Support = -> [YZ_Plane013]
  sketch-geometry (8):
    g0: Circle CenterX=0 CenterY=10 CenterZ=0 NormalX=0 NormalY=0 NormalZ=1 AngleXU=0 Radius=2.35
    g1: Circle CenterX=0 CenterY=45 CenterZ=0 NormalX=0 NormalY=0 NormalZ=1 AngleXU=0 Radius=2.35
    g2: Circle CenterX=0 CenterY=80 CenterZ=0 NormalX=0 NormalY=0 NormalZ=1 AngleXU=0 Radius=2.1
    g3: Circle CenterX=0 CenterY=105 CenterZ=0 NormalX=0 NormalY=0 NormalZ=1 AngleXU=0 Radius=2.1
    g4: Circle CenterX=0 CenterY=133 CenterZ=0 NormalX=0 NormalY=0 NormalZ=1 AngleXU=0 Radius=2.1
    g5: Circle CenterX=0 CenterY=153 CenterZ=0 NormalX=0 NormalY=0 NormalZ=1 AngleXU=0 Radius=2.1
    g6: Circle CenterX=0 CenterY=294.8 CenterZ=0 NormalX=0 NormalY=0 NormalZ=1 AngleXU=0 Radius=2.1
    g7: Circle CenterX=0 CenterY=258.8 CenterZ=0 NormalX=0 NormalY=0 NormalZ=1 AngleXU=0 Radius=2.1
  constraints (24):
    c: PointOnObject(g0,g-2)
    c: PointOnObject(g1,g-2)
    c: Diameter(g1) = 4.7
    c: Equal(g1,g0)
    c: DistanceY(g0,g1) = 35
    c: DistanceY(g-1,g0) = 10
    c: PointOnObject(g2,g-2)
    c: PointOnObject(g3,g-2)
    c: Equal(g2,g3)
    c: DistanceY(g1,g2) = 35
    c: DistanceY(g2,g3) = 25
    c: PointOnObject(g4,g-2)
    c: PointOnObject(g5,g-2)
    c: Equal(g4,g5)
    c: Equal(g5,g3)
    c: DistanceY(g4,g5) = 20
    c: DistanceY(g3,g4) = 28
    c: PointOnObject(g6,g-2)
    c: PointOnObject(g7,g-2)
    c: DistanceY(g7,g6) = 36
    c: Equal(g6,g7)
    c: Equal(g7,g5)
    c: DistanceY(g-1,g6) = 294.8
    c: Diameter(g2) = 4.2
FEATURE [PartDesign::Pocket] Pocket027
  BaseFeature = -> Pad053
  Length = 5
  Length2 = 100
  Profile = -> Sketch087
  Refine = true
  Reversed = true
  Type = 1
FEATURE [PartDesign::Body] Body005
  Group = -> [Sketch086,Pad053,Sketch087,Pocket027]
  Origin = -> Origin013
  Tip = -> Pocket027
FEATURE [PartDesign::CoordinateSystem] plateJ1
  AttacherType = Attacher::AttachEngine3D
  MapMode = 11
  Placement = pos=(5.15938,9e-16,10) rot=(0.707107,0,-0.707107;3.14159rad)
  Support = -> [Pocket027]
FEATURE [PartDesign::CoordinateSystem] baseJ2
  AttacherType = Attacher::AttachEngine3D
  MapMode = 11
  Placement = pos=(5.15937,5.64e-14,258.8) rot=(0.707107,0,-0.707107;3.14159rad)
  Support = -> [Pocket027]
FEATURE [App::Link] HUMERUS
  AssemblyType = Asm4EE
  AttachedBy = #plateJ1
  AttachedTo = J1_PLATE#baseJ004
  AttachmentOffset = pos=(0,0,0) rot=(0.707107,-0.707107,0;3.14159rad)
  LinkPlacement = pos=(-27,39.1594,159) rot=(0.57735,-0.57735,0.57735;4.18879rad)
  LinkedObject = -> HUMERUS_1_0
  Placement = pos=(-27,39.1594,159) rot=(0.57735,-0.57735,0.57735;4.18879rad)
  expr: Placement = J1_PLATE.Placement * baseJ004.Placement * AttachmentOffset * plateJ1.Placement ^ -1
FEATURE [Sketcher::SketchObject] Sketch088
  AttachmentOffset = pos=(0,0,1) rot=(0,0,1;0rad)
  FullyConstrained = true
  MapMode = 5
  Placement = pos=(0,0,1) rot=(0,0,1;0rad)
  Support = -> [XY_Plane006]
  sketch-geometry (6):
    g0: LineSegment StartX=-27 StartY=0 StartZ=0 EndX=-27 EndY=30 EndZ=0
    g1: LineSegment StartX=-27 StartY=30 StartZ=0 EndX=27 EndY=30 EndZ=0
    g2: LineSegment StartX=27 StartY=30 StartZ=0 EndX=27 EndY=0 EndZ=0
    g3: LineSegment StartX=27 StartY=0 StartZ=0 EndX=26.5 EndY=2.63e-14 EndZ=0
    g4: LineSegment StartX=-26.5 StartY=-1.0088e-12 StartZ=0 EndX=-27 EndY=0 EndZ=0
    g5: ArcOfCircle CenterX=0 CenterY=0 CenterZ=0 NormalX=0 NormalY=0 NormalZ=1 AngleXU=0 Radius=26.5 StartAngle=1e-15 EndAngle=3.14159
  constraints (17):
    c: PointOnObject(g0,g-1)
    c: Vertical(g0)
    c: Coincident(g0,g1)
    c: Coincident(g1,g2)
    c: PointOnObject(g2,g-1)
    c: Coincident(g2,g3)
    c: PointOnObject(g3,g-1)
    c: PointOnObject(g4,g-1)
    c: Coincident(g4,g0)
    c: Coincident(g5,g-1)
    c: Coincident(g5,g4)
    c: Coincident(g5,g3)
    c: Diameter(g5) = 53
    c: DistanceX(g1,g1) = 54
    c: Symmetric(g0,g1,g-2)
    c: Vertical(g2)
    c: DistanceY(g-1,g1) = 30
FEATURE [PartDesign::Pad] Pad054
  BaseFeature = -> Pad048
  Direction = (1,1,1)
  Length = 7
  Length2 = 100
  Profile = -> Sketch088
  Refine = true
  Type = 0
FEATURE [Sketcher::SketchObject] Sketch089
  FullyConstrained = true
  MapMode = 5
  Support = -> [XY_Plane006]
  sketch-geometry (2):
    g0: Circle CenterX=-20 CenterY=25 CenterZ=0 NormalX=0 NormalY=0 NormalZ=1 AngleXU=0 Radius=1.7272
    g1: Circle CenterX=20 CenterY=25 CenterZ=0 NormalX=0 NormalY=0 NormalZ=1 AngleXU=0 Radius=1.7272
  constraints (5):
    c: Diameter(g1) = 3.4544
    c: Equal(g1,g0)
    c: Symmetric(g1,g0,g-2)
    c: DistanceX(g0,g1) = 40
    c: DistanceY(g-1,g1) = 25
FEATURE [PartDesign::Pocket] Pocket028
  BaseFeature = -> Pad054
  Length = 5
  Length2 = 100
  Profile = -> Sketch089
  Refine = true
  Reversed = true
  Type = 1
FEATURE [PartDesign::Body] Body002
  Group = -> [Sketch008,Pad007,Sketch012,Hole,Sketch075,Pad048,Sketch088,Pad054,Sketch089,Pocket028]
  Origin = -> Origin006
  Tip = -> Pocket028
FEATURE [App::Part] PLATE_J0_1_0  label="J0_PLATE_2V0"
  Group = -> [LCS_0002,Body002]
  Origin = -> Origin005
FEATURE [Sketcher::SketchObject] Sketch090
  FullyConstrained = true
  MapMode = 5
  Placement = pos=(0,0,0) rot=(1,0,0;1.5708rad)
  Support = -> [XZ_Plane008]
  sketch-geometry (10):
    g0: Circle CenterX=0 CenterY=43 CenterZ=0 NormalX=0 NormalY=0 NormalZ=1 AngleXU=0 Radius=33
    g1: LineSegment StartX=28.2843 StartY=24.6152 StartZ=0 EndX=23.3345 EndY=19.6655 EndZ=0
    g2: LineSegment StartX=23.3345 StartY=12.5944 StartZ=0 EndX=32.5269 EndY=3.40202 EndZ=0
    g3: LineSegment StartX=32.5269 StartY=3.40202 StartZ=0 EndX=41.0122 EndY=11.8873 EndZ=0
    g4: LineSegment StartX=41.0122 StartY=11.8873 StartZ=0 EndX=28.2843 EndY=24.6152 EndZ=0
    g5: Circle CenterX=32.5269 CenterY=10.4731 CenterZ=0 NormalX=0 NormalY=0 NormalZ=1 AngleXU=0 Radius=1.092
    g6: Circle CenterX=26.8701 CenterY=16.1299 CenterZ=0 NormalX=0 NormalY=0 NormalZ=1 AngleXU=0 Radius=1.092
    g7: LineSegment StartX=23.3345 StartY=19.6655 StartZ=0 EndX=36.0624 EndY=6.93755 EndZ=0
    g8: LineSegment StartX=0 StartY=43 StartZ=0 EndX=36.0624 EndY=6.93755 EndZ=0
    g9: LineSegment StartX=23.3345 StartY=12.5944 StartZ=0 EndX=23.3345 EndY=19.6655 EndZ=0
  constraints (29):
    c: PointOnObject(g0,g-2)
    c: Diameter(g0) = 66
    c: DistanceY(g-1,g0) = 43
    c: Coincident(g2,g3)
    c: Coincident(g3,g4)
    c: Coincident(g4,g1)
    c: Parallel(g4,g2)
    c: Parallel(g1,g3)
    c: Perpendicular(g3,g4)
    c: Distance(g4) = 18
    c: PointOnObject(g7,g1)
    c: PointOnObject(g7,g3)
    c: Parallel(g7,g4)
    c: PointOnObject(g6,g7)
    c: PointOnObject(g5,g7)
    c: Distance(g5,g7) = 5
    c: Distance(g6,g5) = 8
    c: Diameter(g5) = 2.184
    c: Equal(g5,g6)
    c: Distance(g7,g3) = 7
    c: Angle(g2,g-1) = 0.785398
    c: Coincident(g8,g0)
    c: Coincident(g8,g7)
    c: PointOnObject(g7,g8)
    c: Distance(g7,g2) = 5
    c: Vertical(g9)
    c: Coincident(g9,g7)
    c: Coincident(g2,g9)
    c: Tangent(g1,g0) = 1.5708
FEATURE [PartDesign::Pad] Pad055
  BaseFeature = -> Pad049
  Direction = (1,1,1)
  Length = 26.5
  Length2 = 100
  Profile = -> Sketch090
  Refine = true
  Reversed = true
  Type = 0
  expr: Length = <<var>>.baseJ1EncoderH
FEATURE [App::Link] ENCODER_BRACKET_1
  AssemblyType = Asm4EE
  AttachedBy = #LCS_0013
  AttachedTo = J1_PLATE#LCS_0015
  AttachmentOffset = pos=(0,0,10.5) rot=(0,0,1;0.785398rad)
  LinkPlacement = pos=(1.7e-14,36.5,141) rot=(-0.281085,-0.678598,-0.678598;2.59356rad)
  LinkedObject = -> ENCODER_BRACKET_1_0
  Placement = pos=(1.7e-14,36.5,141) rot=(-0.281085,-0.678598,-0.678598;2.59356rad)
  expr: Placement = J1_PLATE.Placement * LCS_0015.Placement * AttachmentOffset * LCS_0013.Placement ^ -1
FEATURE [PartDesign::Hole] Hole004
  BaseFeature = -> Pocket013
  Depth = 25
  DepthType = 1
  Diameter = 3.4
  DrillForDepth = false
  DrillPoint = 1
  DrillPointAngle = 118
  HoleCutCountersinkAngle = 90
  HoleCutCustomValues = false
  HoleCutDepth = 0
  HoleCutDiameter = 6.1
  HoleCutType = 2
  ModelActualThread = false
  Profile = -> Sketch031
  Tapered = false
  TaperedAngle = 90
  ThreadAngle = 0
  ThreadClass = 0
  ThreadCutOffInner = 0
  ThreadCutOffOuter = 0
  ThreadDirection = 0
  ThreadFit = 0
  ThreadPitch = 0
  ThreadSize = 9
  ThreadType = 1
  Threaded = false
FEATURE [PartDesign::Body] Body006
  Group = -> [Sketch030,Pad018,Sketch031,Sketch032,Sketch036,Pad021,Pocket013,Hole004]
  Origin = -> Origin015
  Tip = -> Hole004
FEATURE [PartDesign::CoordinateSystem] humerus001
  AttacherType = Attacher::AttachEngine3D
  MapMode = 11
  Placement = pos=(-10,0,6) rot=(0,0,1;0rad)
  Support = -> [Hole004]
FEATURE [PartDesign::CoordinateSystem] motor001
  AttacherType = Attacher::AttachEngine3D
  MapMode = 11
  Placement = pos=(0,30,0) rot=(0,0,1;1.5708rad)
  Support = -> [Hole004]
FEATURE [App::Link] MOTOR_17HS13_0404S_PG27_2
  AssemblyType = Asm4EE
  AttachedBy = #LCS_0
  AttachedTo = BRACKET_MOTOR_J2_1_0001#motor001
  LinkPlacement = pos=(53,28,189) rot=(0.57735,0.57735,0.57735;4.18879rad)
  LinkedObject = -> <external MOTOR-17HS13-0404S-PG27.FCStd>#Part
  Placement = pos=(53,28,189) rot=(0.57735,0.57735,0.57735;4.18879rad)
  expr: Placement = BRACKET_MOTOR_J2_1_0001.Placement * motor001.Placement * AttachmentOffset * MOTOR_17HS13_0404S_PG27#LCS_0.Placement ^ -1
FEATURE [Sketcher::SketchObject] Sketch091
  FullyConstrained = true
  MapMode = 5
  Support = -> [XY_Plane018]
  sketch-geometry (2):
    g0: Circle CenterX=0 CenterY=0 CenterZ=0 NormalX=0 NormalY=0 NormalZ=1 AngleXU=0 Radius=28
    g1: Circle CenterX=0 CenterY=0 CenterZ=0 NormalX=0 NormalY=0 NormalZ=1 AngleXU=0 Radius=24
  constraints (4):
    c: Coincident(g0,g-1)
    c: Coincident(g1,g0)
    c: Diameter(g0) = 56
    c: Diameter(g1) = 48
FEATURE [PartDesign::Pad] Pad056
  BaseFeature = -> Revolution
  Direction = (1,1,1)
  Length = 10
  Length2 = 100
  Profile = -> Sketch091
  Type = 0
FEATURE [PartDesign::CoordinateSystem] humerus003
  AttacherType = Attacher::AttachEngine3D
  MapMode = 11
  Placement = pos=(-18,-28.3187,0) rot=(0,0,1;1.5708rad)
  Support = -> [Pad056]
FEATURE [App::Link] BALL_6808
  AssemblyType = Asm4EE
  AttachedBy = #LCS_0
  AttachedTo = BASE_J2_1_0001#LCS_0009
  AttachmentOffset = pos=(0,0,9) rot=(0,0,1;0rad)
  LinkPlacement = pos=(249.8,25,187.319) rot=(-1,0,0;4.71239rad)
  LinkedObject = -> <external BALL-6808.FCStd>#Part
  Placement = pos=(249.8,25,187.319) rot=(-1,0,0;4.71239rad)
  expr: Placement = BASE_J2_1_0001.Placement * LCS_0009.Placement * AttachmentOffset * BALL_6808#LCS_0.Placement ^ -1
FEATURE [PartDesign::CoordinateSystem] LCS_0016
  AttacherType = Attacher::AttachEngine3D
  MapMode = 2
  Support = -> [X_Axis037]
FEATURE [Sketcher::SketchObject] Sketch092
  AttachmentOffset = pos=(0,0,8) rot=(0,0,1;0rad)
  FullyConstrained = true
  MapMode = 5
  Placement = pos=(0,0,8) rot=(0,0,1;0rad)
  Support = -> [XY_Plane038]
  expr: Constraints[16] = <<var>>.hubHoleD
  expr: Constraints[15] = <<var>>.hubHolePD
  sketch-geometry (9):
    g0: LineSegment StartX=-6.9148 StartY=6.9148 StartZ=0 EndX=6.9148 EndY=6.9148 EndZ=0
    g1: LineSegment StartX=6.9148 StartY=6.9148 StartZ=0 EndX=6.9148 EndY=-6.9148 EndZ=0
    g2: LineSegment StartX=6.9148 StartY=-6.9148 StartZ=0 EndX=-6.9148 EndY=-6.9148 EndZ=0
    g3: LineSegment StartX=-6.9148 StartY=-6.9148 StartZ=0 EndX=-6.9148 EndY=6.9148 EndZ=0
    g4: Circle CenterX=-6.9148 CenterY=6.9148 CenterZ=0 NormalX=0 NormalY=0 NormalZ=1 AngleXU=0 Radius=1.905
    g5: Circle CenterX=6.9148 CenterY=6.9148 CenterZ=0 NormalX=0 NormalY=0 NormalZ=1 AngleXU=0 Radius=1.905
    g6: Circle CenterX=6.9148 CenterY=-6.9148 CenterZ=0 NormalX=0 NormalY=0 NormalZ=1 AngleXU=0 Radius=1.905
    g7: Circle CenterX=-6.9148 CenterY=-6.9148 CenterZ=0 NormalX=0 NormalY=0 NormalZ=1 AngleXU=0 Radius=1.905
    g8: LineSegment StartX=-6.9148 StartY=6.9148 StartZ=0 EndX=6.9148 EndY=-6.9148 EndZ=0
  constraints (20):
    c: Coincident(g0,g1)
    c: Coincident(g1,g2)
    c: Coincident(g2,g3)
    c: Coincident(g3,g0)
    c: Horizontal(g2)
    c: Vertical(g1)
    c: Symmetric(g0,g0,g-2)
    c: Symmetric(g0,g2,g-1)
    c: Equal(g3,g0)
    c: Coincident(g4,g0)
    c: Coincident(g5,g0)
    c: Coincident(g6,g1)
    c: Coincident(g7,g2)
    c: Coincident(g8,g4)
    c: Coincident(g8,g6)
    c: Distance(g8) = 19.558
    c: Diameter(g4) = 3.81
    c: Equal(g4,g7)
    c: Equal(g4,g6)
    c: Equal(g4,g5)
FEATURE [Sketcher::SketchObject] Sketch093
  AttachmentOffset = pos=(0,0,4.5) rot=(0,0,1;0rad)
  FullyConstrained = true
  MapMode = 5
  Placement = pos=(0,0,4.5) rot=(0,0,1;0rad)
  Support = -> [XY_Plane038]
  sketch-geometry (1):
    g0: Circle CenterX=0 CenterY=0 CenterZ=0 NormalX=0 NormalY=0 NormalZ=1 AngleXU=0 Radius=4
  constraints (2):
    c: Coincident(g0,g-1)
    c: Diameter(g0) = 8
FEATURE [Sketcher::SketchObject] Sketch094
  AttachmentOffset = pos=(0,0,2) rot=(0,0,1;0rad)
  FullyConstrained = true
  MapMode = 5
  Placement = pos=(0,0,2) rot=(0,0,1;0rad)
  Support = -> [XY_Plane038]
  sketch-geometry (6):
    g0: Circle CenterX=-12 CenterY=18.3 CenterZ=0 NormalX=0 NormalY=0 NormalZ=1 AngleXU=0 Radius=1.75
    g1: Circle CenterX=12 CenterY=18.3 CenterZ=0 NormalX=0 NormalY=0 NormalZ=1 AngleXU=0 Radius=1.75
    g2: LineSegment StartX=-22 StartY=8 StartZ=0 EndX=22 EndY=8 EndZ=0
    g3: LineSegment StartX=-22 StartY=0 StartZ=0 EndX=-22 EndY=28.6 EndZ=0
    g4: LineSegment StartX=-22 StartY=28.6 StartZ=0 EndX=22 EndY=28.6 EndZ=0
    g5: LineSegment StartX=22 StartY=28.6 StartZ=0 EndX=22 EndY=0 EndZ=0
  constraints (20):
    c: Horizontal(g2)
    c: DistanceY(g-1,g2) = 8
    c: Equal(g0,g1)
    c: Diameter(g0) = 3.5
    c: PointOnObject(g3,g-1)
    c: Vertical(g3)
    c: Coincident(g3,g4)
    c: Coincident(g4,g5)
    c: PointOnObject(g5,g-1)
    c: Vertical(g5)
    c: Symmetric(g3,g4,g-2)
    c: PointOnObject(g2,g5)
    c: PointOnObject(g2,g3)
    c: DistanceX(g4,g4) = 44
    c: DistanceY(g5,g5) = 28.6
    c: DistanceY(g2,g1) = 10.3
    c: DistanceX(g1,g4) = 10
    c: Horizontal(g0,g1)
    c: DistanceX(g3,g0) = 10
    c: DistanceX(g0,g1) = 24
FEATURE [Sketcher::SketchObject] Sketch095
  AttachmentOffset = pos=(0,0,1) rot=(0,0,1;0rad)
  FullyConstrained = true
  MapMode = 5
  Placement = pos=(0,0,1) rot=(0,0,1;0rad)
  Support = -> [XY_Plane038]
  sketch-geometry (7):
    g0: LineSegment StartX=-22 StartY=0 StartZ=0 EndX=-22 EndY=28.6 EndZ=0
    g1: LineSegment StartX=-22 StartY=28.6 StartZ=0 EndX=22 EndY=28.6 EndZ=0
    g2: LineSegment StartX=22 StartY=28.6 StartZ=0 EndX=22 EndY=0 EndZ=0
    g3: LineSegment StartX=22 StartY=0 StartZ=0 EndX=21 EndY=-7.46e-14 EndZ=0
    g4: LineSegment StartX=-21 StartY=3.8635e-12 StartZ=0 EndX=-22 EndY=0 EndZ=0
    g5: ArcOfCircle CenterX=0 CenterY=0 CenterZ=0 NormalX=0 NormalY=0 NormalZ=1 AngleXU=0 Radius=21 StartAngle=-3.6e-15 EndAngle=3.14159
    g6: LineSegment StartX=-22 StartY=8 StartZ=0 EndX=22 EndY=8 EndZ=0
  constraints (21):
    c: PointOnObject(g0,g-1)
    c: Vertical(g0)
    c: Coincident(g1,g0)
    c: Coincident(g2,g1)
    c: PointOnObject(g2,g-1)
    c: Coincident(g3,g2)
    c: PointOnObject(g3,g-1)
    c: PointOnObject(g4,g-1)
    c: Coincident(g4,g0)
    c: Coincident(g5,g-1)
    c: Coincident(g5,g4)
    c: Coincident(g5,g3)
    c: Vertical(g2)
    c: DistanceX(g1,g1) = 44
    c: Symmetric(g0,g1,g-2)
    c: Diameter(g5) = 42
    c: PointOnObject(g6,g0)
    c: PointOnObject(g6,g2)
    c: Horizontal(g6)
    c: DistanceY(g6,g1) = 20.6
    c: DistanceY(g-1,g6) = 8
FEATURE [Sketcher::SketchObject] Sketch096
  FullyConstrained = true
  MapMode = 5
  Support = -> [XY_Plane038]
  sketch-geometry (2):
    g0: Circle CenterX=0 CenterY=0 CenterZ=0 NormalX=0 NormalY=0 NormalZ=1 AngleXU=0 Radius=3.1
    g1: Circle CenterX=0 CenterY=0 CenterZ=0 NormalX=0 NormalY=0 NormalZ=1 AngleXU=0 Radius=22
  constraints (4):
    c: Diameter(g0) = 6.2
    c: Coincident(g0,g-1)
    c: Coincident(g1,g0)
    c: Diameter(g1) = 44
FEATURE [PartDesign::Pad] Pad057
  AllowMultiFace = false
  Direction = (1,1,1)
  Length = 8
  Length2 = 100
  Profile = -> Sketch096
  Type = 0
FEATURE [PartDesign::Hole] Hole005
  BaseFeature = -> Pad057
  Depth = 25
  DepthType = 1
  Diameter = 4.3
  DrillForDepth = false
  DrillPoint = 1
  DrillPointAngle = 118
  HoleCutCountersinkAngle = 82
  HoleCutCustomValues = false
  HoleCutDepth = 0
  HoleCutDiameter = 8.298
  HoleCutType = 2
  ModelActualThread = false
  Profile = -> Sketch092
  Refine = true
  Tapered = false
  TaperedAngle = 90
  ThreadAngle = 0
  ThreadClass = 0
  ThreadCutOffInner = 0
  ThreadCutOffOuter = 0
  ThreadDirection = 0
  ThreadFit = 0
  ThreadPitch = 0
  ThreadSize = 5
  ThreadType = 3
  Threaded = false
FEATURE [PartDesign::Pad] Pad058
  BaseFeature = -> Hole005
  Direction = (1,1,1)
  Length = 1
  Length2 = 100
  Profile = -> Sketch093
  Type = 0
FEATURE [PartDesign::Pad] Pad059
  BaseFeature = -> Pad058
  Direction = (1,1,1)
  Length = 7
  Length2 = 100
  Profile = -> Sketch095
  Refine = true
  Type = 0
FEATURE [PartDesign::Pocket] Pocket029
  BaseFeature = -> Pad059
  Length = 5
  Length2 = 100
  Profile = -> Sketch094
  Refine = true
  Reversed = true
  Type = 1
FEATURE [PartDesign::Body] Body018
  Group = -> [Sketch096,Pad057,Sketch092,Hole005,Sketch093,Pad058,Sketch094,Sketch095,Pad059,Pocket029]
  Origin = -> Origin038
  Tip = -> Pocket029
FEATURE [App::Link] J2_PLATE  label="J2-PLATE"
  AssemblyType = Asm4EE
  AttachedBy = #LCS_0016
  AttachedTo = BALL_6808#LCS_0
  AttachmentOffset = pos=(0,0,7) rot=(0,0,1;0rad)
  LinkPlacement = pos=(249.8,18,187.319) rot=(-1,0,0;4.71239rad)
  LinkedObject = -> PLATE_J0_1_0003
  Placement = pos=(249.8,18,187.319) rot=(-1,0,0;4.71239rad)
  expr: Placement = BALL_6808.Placement * BALL_6808#LCS_0.Placement * AttachmentOffset * LCS_0016.Placement ^ -1
FEATURE [PartDesign::CoordinateSystem] radius
  AttacherType = Attacher::AttachEngine3D
  MapMode = 11
  Placement = pos=(-12,18.3,8) rot=(0.707107,-0.707107,0;3.14159rad)
  Support = -> [Pocket029]
FEATURE [App::Part] PLATE_J0_1_0003  label="J2_PLATE_2V0"
  Group = -> [LCS_0016,Body018,radius]
  Origin = -> Origin037
FEATURE [Sketcher::SketchObject] Sketch098
  FullyConstrained = true
  MapMode = 5
  Support = -> [XY_Plane018]
  sketch-geometry (7):
    g0: LineSegment StartX=-26 StartY=8 StartZ=0 EndX=-44 EndY=8 EndZ=0
    g1: LineSegment StartX=-44 StartY=8 StartZ=0 EndX=-44 EndY=-4.5 EndZ=0
    g2: LineSegment StartX=-44 StartY=-4.5 StartZ=0 EndX=-26 EndY=-4.5 EndZ=0
    g3: LineSegment StartX=-26 StartY=-4.5 StartZ=0 EndX=-26 EndY=8 EndZ=0
    g4: Circle CenterX=-39 CenterY=0 CenterZ=0 NormalX=0 NormalY=0 NormalZ=1 AngleXU=0 Radius=2.55
    g5: Circle CenterX=-31 CenterY=0 CenterZ=0 NormalX=0 NormalY=0 NormalZ=1 AngleXU=0 Radius=2.55
    g6: Circle CenterX=0 CenterY=0 CenterZ=0 NormalX=0 NormalY=0 NormalZ=1 AngleXU=0 Radius=26
  constraints (20):
    c: Horizontal(g0)
    c: Coincident(g0,g1)
    c: Coincident(g1,g2)
    c: Horizontal(g2)
    c: Coincident(g2,g3)
    c: Coincident(g3,g0)
    c: Vertical(g3)
    c: PointOnObject(g4,g-1)
    c: PointOnObject(g5,g-1)
    c: DistanceX(g4,g5) = 8
    c: Diameter(g4) = 5.1
    c: Equal(g4,g5)
    c: DistanceX(g0,g4) = 5
    c: Coincident(g6,g-1)
    c: Diameter(g6) = 52
    c: Tangent(g3,g6)
    c: DistanceX(g5,g-1) = 31
    c: DistanceY(g1,g-1) = 4.5
    c: DistanceY(g-1,g0) = 8
    c: Vertical(g1)
FEATURE [PartDesign::Pad] Pad060
  BaseFeature = -> Pad056
  Direction = (1,1,1)
  Length = 27.5
  Length2 = 100
  Profile = -> Sketch098
  Type = 0
  expr: Length = <<var>>.J2BaseEncoderH
FEATURE [PartDesign::Body] Body007
  Group = -> [Sketch040,Pad025,Sketch038,Pad023,Sketch039,Pad024,Sketch041,Groove,Sketch065,Revolution,Sketch091,Pad056,Sketch098,Pad060]
  Origin = -> Origin018
  Tip = -> Pad060
FEATURE [PartDesign::CoordinateSystem] encoder
  AttacherType = Attacher::AttachEngine3D
  MapMode = 11
  Placement = pos=(-39,0,27.5) rot=(0,0,1;1.5708rad)
  Support = -> [Pad060]
FEATURE [App::Part] BASE_J2_1_0  label="J2_BASE_2V0"
  Group = -> [LCS_0009,Body007,humerus003,encoder]
  Origin = -> Origin019
FEATURE [Sketcher::SketchObject] Sketch099
  FullyConstrained = true
  MapMode = 5
  Support = -> [XY_Plane040]
  sketch-geometry (14):
    g0: LineSegment StartX=-7 StartY=-44 StartZ=0 EndX=5 EndY=-44 EndZ=0
    g1: LineSegment StartX=5 StartY=-44 StartZ=0 EndX=5 EndY=-21 EndZ=0
    g2: LineSegment StartX=-3 StartY=4 StartZ=0 EndX=3 EndY=4 EndZ=0
    g3: LineSegment StartX=3 StartY=4 StartZ=0 EndX=3 EndY=-21 EndZ=0
    g4: LineSegment StartX=3 StartY=-21 StartZ=0 EndX=-3 EndY=-21 EndZ=0
    g5: LineSegment StartX=-3 StartY=-21 StartZ=0 EndX=-3 EndY=4 EndZ=0
    g6: Circle CenterX=0 CenterY=-10 CenterZ=0 NormalX=0 NormalY=0 NormalZ=1 AngleXU=0 Radius=1.32
    g7: LineSegment StartX=-3 StartY=-13.5 StartZ=0 EndX=5 EndY=-13.5 EndZ=0
    g8: LineSegment StartX=5 StartY=-21 StartZ=0 EndX=-3 EndY=-21 EndZ=0
    g9: LineSegment StartX=-3 StartY=-21 StartZ=0 EndX=-3 EndY=-13.5 EndZ=0
    g10: Circle CenterX=0 CenterY=0 CenterZ=0 NormalX=0 NormalY=0 NormalZ=1 AngleXU=0 Radius=26
    g11: LineSegment StartX=5 StartY=-13.5 StartZ=0 EndX=5 EndY=-5 EndZ=0
    g12: LineSegment StartX=-7 StartY=-5 StartZ=0 EndX=-7 EndY=-44 EndZ=0
    g13: LineSegment StartX=-7 StartY=-5 StartZ=0 EndX=5 EndY=-5 EndZ=0
  constraints (38):
    c: Coincident(g0,g1)
    c: Horizontal(g0)
    c: Vertical(g1)
    c: DistanceY(g0,g-1) = 44
    c: Coincident(g2,g3)
    c: Coincident(g3,g4)
    c: Coincident(g4,g5)
    c: Coincident(g5,g2)
    c: Horizontal(g4)
    c: Vertical(g3)
    c: Vertical(g5)
    c: DistanceY(g3,g3) = 25
    c: Symmetric(g2,g2,g-2)
    c: DistanceX(g2,g2) = 6
    c: PointOnObject(g6,g-2)
    c: Diameter(g6) = 2.64
    c: DistanceY(g6,g2) = 14
    c: Coincident(g8,g9)
    c: Coincident(g9,g7)
    c: Horizontal(g8)
    c: Vertical(g9)
    c: DistanceY(g8,g7) = 7.5
    c: Coincident(g10,g-1)
    c: Diameter(g10) = 52
    c: Horizontal(g7)
    c: Coincident(g1,g8)
    c: Coincident(g11,g7)
    c: Tangent(g1,g11)
    c: Vertical(g12)
    c: Coincident(g0,g12)
    c: DistanceX(g12,g-1) = 7
    c: DistanceY(g-1,g2) = 4
    c: DistanceX(g-1,g0) = 5
    c: Coincident(g8,g4)
    c: Coincident(g13,g12)
    c: Coincident(g13,g11)
    c: Horizontal(g13)
    c: DistanceY(g6,g11) = 5
FEATURE [Sketcher::SketchObject] Sketch100
  FullyConstrained = true
  MapMode = 5
  Support = -> [XY_Plane040]
  sketch-geometry (6):
    g0: LineSegment StartX=6 StartY=-21 StartZ=0 EndX=-3 EndY=-21 EndZ=0
    g1: LineSegment StartX=6 StartY=4 StartZ=0 EndX=6 EndY=-21 EndZ=0
    g2: LineSegment StartX=-6 StartY=4 StartZ=0 EndX=6 EndY=4 EndZ=0
    g3: LineSegment StartX=-3 StartY=-21 StartZ=0 EndX=-3 EndY=-8 EndZ=0
    g4: ArcOfCircle CenterX=-6 CenterY=-8 CenterZ=0 NormalX=0 NormalY=0 NormalZ=1 AngleXU=0 Radius=3 StartAngle=0 EndAngle=1.5708
    g5: LineSegment StartX=-6 StartY=-5 StartZ=0 EndX=-6 EndY=4 EndZ=0
  constraints (19):
    c: Horizontal(g0)
    c: DistanceY(g0,g2) = 25
    c: Coincident(g1,g0)
    c: Vertical(g1)
    c: DistanceY(g-1,g1) = 4
    c: Coincident(g2,g1)
    c: Horizontal(g2)
    c: DistanceX(g-1,g1) = 6
    c: DistanceX(g0,g-1) = 3
    c: Coincident(g3,g0)
    c: Vertical(g3)
    c: Coincident(g4,g3)
    c: Coincident(g5,g4)
    c: Coincident(g5,g2)
    c: Vertical(g5)
    c: Diameter(g4) = 6
    c: Vertical(g4,g4)
    c: Horizontal(g4,g3)
    c: DistanceY(g5,g5) = 9
FEATURE [PartDesign::Pad] Pad061
  Direction = (1,1,1)
  Length = 8
  Length2 = 100
  Profile = -> Sketch099
  Type = 0
FEATURE [PartDesign::Pocket] Pocket030
  BaseFeature = -> Pad061
  Length = 1.6
  Length2 = 100
  Profile = -> Sketch100
  Reversed = true
  Type = 0
FEATURE [PartDesign::CoordinateSystem] LCS_0017
  AttacherType = Attacher::AttachEngine3D
  MapMode = 2
  Support = -> [X_Axis039]
FEATURE [PartDesign::CoordinateSystem] LCS_0018
  AttacherType = Attacher::AttachEngine3D
  MapMode = 2
  Support = -> [X_Axis040]
FEATURE [Sketcher::SketchObject] Sketch101
  AttachmentOffset = pos=(0,0,8) rot=(0,0,1;0rad)
  FullyConstrained = true
  MapMode = 5
  Placement = pos=(0,0,8) rot=(0,0,1;0rad)
  Support = -> [XY_Plane040]
  sketch-geometry (2):
    g0: Circle CenterX=0 CenterY=-31 CenterZ=0 NormalX=0 NormalY=0 NormalZ=1 AngleXU=0 Radius=1.5
    g1: Circle CenterX=0 CenterY=-39 CenterZ=0 NormalX=0 NormalY=0 NormalZ=1 AngleXU=0 Radius=1.5
  constraints (6):
    c: PointOnObject(g0,g-2)
    c: PointOnObject(g1,g-2)
    c: Diameter(g1) = 3
    c: Equal(g1,g0)
    c: DistanceY(g1,g0) = 8
    c: DistanceY(g0,g-1) = 31
FEATURE [PartDesign::Hole] Hole006
  BaseFeature = -> Pocket030
  Depth = 25
  DepthType = 1
  Diameter = 3.3
  DrillForDepth = false
  DrillPoint = 1
  DrillPointAngle = 118
  HoleCutCountersinkAngle = 82
  HoleCutCustomValues = false
  HoleCutDepth = 0
  HoleCutDiameter = 6
  HoleCutType = 2
  ModelActualThread = false
  Profile = -> Sketch101
  Tapered = false
  TaperedAngle = 90
  ThreadAngle = 0
  ThreadClass = 0
  ThreadCutOffInner = 0
  ThreadCutOffOuter = 0
  ThreadDirection = 0
  ThreadFit = 0
  ThreadPitch = 0
  ThreadSize = 3
  ThreadType = 3
  Threaded = false
FEATURE [PartDesign::Body] Body_004
  Group = -> [LCS_0018,Sketch099,Sketch100,Pad061,Pocket030,Sketch101,Hole006]
  Origin = -> Origin040
  Tip = -> Hole006
FEATURE [App::Link] ENCODER_BRACKET_J2  label="ENCODER-BRACKET-J2"
  AssemblyType = Asm4EE
  AttachedBy = #LCS_0017
  AttachedTo = J2_PLATE#LCS_0016
  AttachmentOffset = pos=(0,0,10.5) rot=(0,0,1;4.71239rad)
  LinkPlacement = pos=(249.8,7.5,187.319) rot=(0.57735,0.57735,-0.57735;2.0944rad)
  LinkedObject = -> ENCODER_BRACKET_1_001
  Placement = pos=(249.8,7.5,187.319) rot=(0.57735,0.57735,-0.57735;2.0944rad)
  expr: Placement = J2_PLATE.Placement * LCS_0016.Placement * AttachmentOffset * LCS_0017.Placement ^ -1
FEATURE [TechDraw::DrawProjGroupItem] ProjItem003  label="Front002"
  CoarseView = false
  Direction = (1,0,0)
  Focus = 100
  HardHidden = false
  IsoCount = 0
  IsoHidden = false
  IsoVisible = false
  LockPosition = true
  Perspective = false
  Rotation = 0
  RotationVector = (0,1,0)
  Scale = 0.5
  ScaleType = 2
  SeamHidden = false
  SeamVisible = true
  SmoothHidden = false
  SmoothVisible = true
  Source = -> [Pocket027]
  Type = 0
  X = 0
  XDirection = (0,1e-16,1)
  Y = 0
FEATURE [TechDraw::DrawProjGroup] ProjGroup003
  Anchor = -> ProjItem003
  AutoDistribute = true
  LockPosition = false
  ProjectionType = 1
  Rotation = 0
  Scale = 0.5
  ScaleType = 2
  Source = -> [Pocket027]
  Views = -> [ProjItem003]
  X = 136.645
  Y = 111.514
  spacingX = 15
  spacingY = 15
FEATURE [TechDraw::DrawViewDimension] Dimension023
  Arbitrary = false
  ArbitraryTolerances = false
  EqualTolerance = true
  FormatSpec = %.2f
  FormatSpecOverTolerance = %+.2f
  FormatSpecUnderTolerance = %+.2f
  Inverted = false
  LockPosition = false
  MeasureType = 1
  OverTolerance = 0
  References2D = -> [ProjItem003]
  Rotation = 0
  ScaleType = 0
  TheoreticalExact = false
  Type = 2
  UnderTolerance = 0
  X = -89.4354
  Y = 15.8943
FEATURE [TechDraw::DrawViewDimension] Dimension024
  Arbitrary = false
  ArbitraryTolerances = false
  EqualTolerance = true
  FormatSpec = %.2f
  FormatSpecOverTolerance = %+.2f
  FormatSpecUnderTolerance = %+.2f
  Inverted = false
  LockPosition = false
  MeasureType = 1
  OverTolerance = 0
  References2D = -> [ProjItem003]
  Rotation = 0
  ScaleType = 0
  TheoreticalExact = false
  Type = 1
  UnderTolerance = 0
  X = -70.4722
  Y = 16.1633
FEATURE [TechDraw::DrawViewDimension] Dimension025
  Arbitrary = false
  ArbitraryTolerances = false
  EqualTolerance = true
  FormatSpec = %.2f
  FormatSpecOverTolerance = %+.2f
  FormatSpecUnderTolerance = %+.2f
  Inverted = false
  LockPosition = false
  MeasureType = 1
  OverTolerance = 0
  References2D = -> [ProjItem003]
  Rotation = 0
  ScaleType = 0
  TheoreticalExact = false
  Type = 1
  UnderTolerance = 0
  X = -66.1604
  Y = 24.7707
FEATURE [TechDraw::DrawViewDimension] Dimension026
  Arbitrary = false
  ArbitraryTolerances = false
  EqualTolerance = true
  FormatSpec = %.2f
  FormatSpecOverTolerance = %+.2f
  FormatSpecUnderTolerance = %+.2f
  Inverted = false
  LockPosition = false
  MeasureType = 1
  OverTolerance = 0
  References2D = -> [ProjItem003]
  Rotation = 0
  ScaleType = 0
  TheoreticalExact = false
  Type = 1
  UnderTolerance = 0
  X = -57.1414
  Y = 33.2436
FEATURE [TechDraw::DrawViewDimension] Dimension027
  Arbitrary = false
  ArbitraryTolerances = false
  EqualTolerance = true
  FormatSpec = %.2f
  FormatSpecOverTolerance = %+.2f
  FormatSpecUnderTolerance = %+.2f
  Inverted = false
  LockPosition = false
  MeasureType = 1
  OverTolerance = 0
  References2D = -> [ProjItem003]
  Rotation = 0
  ScaleType = 0
  TheoreticalExact = false
  Type = 1
  UnderTolerance = 0
  X = -45.7808
  Y = 39.8337
FEATURE [TechDraw::DrawViewDimension] Dimension028
  Arbitrary = false
  ArbitraryTolerances = false
  EqualTolerance = true
  FormatSpec = %.2f
  FormatSpecOverTolerance = %+.2f
  FormatSpecUnderTolerance = %+.2f
  Inverted = false
  LockPosition = false
  MeasureType = 1
  OverTolerance = 0
  References2D = -> [ProjItem003]
  Rotation = 0
  ScaleType = 0
  TheoreticalExact = false
  Type = 1
  UnderTolerance = 0
  X = -35.6875
  Y = 46.8272
FEATURE [TechDraw::DrawViewDimension] Dimension029
  Arbitrary = false
  ArbitraryTolerances = false
  EqualTolerance = true
  FormatSpec = %.2f
  FormatSpecOverTolerance = %+.2f
  FormatSpecUnderTolerance = %+.2f
  Inverted = false
  LockPosition = false
  MeasureType = 1
  OverTolerance = 0
  References2D = -> [ProjItem003]
  Rotation = 0
  ScaleType = 0
  TheoreticalExact = false
  Type = 1
  UnderTolerance = 0
  X = -24.7699
  Y = 53.9552
FEATURE [TechDraw::DrawViewDimension] Dimension030
  Arbitrary = false
  ArbitraryTolerances = false
  EqualTolerance = true
  FormatSpec = %.2f
  FormatSpecOverTolerance = %+.2f
  FormatSpecUnderTolerance = %+.2f
  Inverted = false
  LockPosition = false
  MeasureType = 1
  OverTolerance = 0
  References2D = -> [ProjItem003]
  Rotation = 0
  ScaleType = 0
  TheoreticalExact = false
  Type = 1
  UnderTolerance = 0
  X = 68.3204
  Y = 16.9702
FEATURE [TechDraw::DrawViewDimension] Dimension031
  Arbitrary = false
  ArbitraryTolerances = false
  EqualTolerance = true
  FormatSpec = %.2f
  FormatSpecOverTolerance = %+.2f
  FormatSpecUnderTolerance = %+.2f
  Inverted = false
  LockPosition = false
  MeasureType = 1
  OverTolerance = 0
  References2D = -> [ProjItem003]
  Rotation = 0
  ScaleType = 0
  TheoreticalExact = false
  Type = 1
  UnderTolerance = 0
  X = 65.238
  Y = 26.9226
FEATURE [TechDraw::DrawPage] Page001
  KeepUpdated = true
  NextBalloonIndex = 1
  ProjectionType = 1
  Template = -> Template001
  Views = -> [ProjGroup003,Dimension023,Dimension024,Dimension025,Dimension026,Dimension027,Dimension028,Dimension029,Dimension030,Dimension031]
FEATURE [App::Part] HUMERUS_1_0  label="HUMERUS_2V0"
  Group = -> [LCS_0005,Body005,plateJ1,baseJ2,Page001]
  Origin = -> Origin012
FEATURE [Sketcher::SketchObject] Sketch102
  AttachmentOffset = pos=(0,0,5) rot=(0,0,1;0rad)
  FullyConstrained = true
  MapMode = 5
  Placement = pos=(0,0,5) rot=(0,0,1;0rad)
  Support = -> [XY_Plane017]
  sketch-geometry (2):
    g0: Circle CenterX=15 CenterY=0 CenterZ=0 NormalX=0 NormalY=0 NormalZ=1 AngleXU=0 Radius=2.25
    g1: Circle CenterX=30 CenterY=0 CenterZ=0 NormalX=0 NormalY=0 NormalZ=1 AngleXU=0 Radius=2.25
  constraints (6):
    c: PointOnObject(g0,g-1)
    c: Diameter(g0) = 4.5
    c: Equal(g0,g1)
    c: DistanceX(g-1,g0) = 15
    c: DistanceX(g0,g1) = 15
    c: PointOnObject(g1,g-1)
FEATURE [PartDesign::Hole] Hole007
  BaseFeature = -> Pad020
  Depth = 25
  DepthType = 1
  Diameter = 4.5
  DrillForDepth = false
  DrillPoint = 1
  DrillPointAngle = 118
  HoleCutCountersinkAngle = 90
  HoleCutCustomValues = false
  HoleCutDepth = 0
  HoleCutDiameter = 9
  HoleCutType = 7
  ModelActualThread = false
  Profile = -> Sketch102
  Refine = true
  Tapered = false
  TaperedAngle = 90
  ThreadAngle = 0
  ThreadClass = 0
  ThreadCutOffInner = 0
  ThreadCutOffOuter = 0
  ThreadDirection = 0
  ThreadFit = 0
  ThreadPitch = 0
  ThreadSize = 11
  ThreadType = 1
  Threaded = false
FEATURE [PartDesign::Body] Body_2
  Group = -> [LCS_0008,Sketch033,Pad019,Sketch035,Pad020,Sketch102,Hole007]
  Origin = -> Origin017
  Tip = -> Hole007
FEATURE [App::Part] TENSIONER_J2  label="J2_TENSIONER_2V0"
  Group = -> [LCS_0007,Body_2,humerus002]
  Origin = -> Origin016
FEATURE [PartDesign::CoordinateSystem] LCS_0019
  AttacherType = Attacher::AttachEngine3D
  MapMode = 2
  Support = -> [X_Axis041]
FEATURE [Sketcher::SketchObject] Sketch103
  AttachmentOffset = pos=(0,0,5) rot=(0,0,1;0rad)
  FullyConstrained = true
  MapMode = 5
  Placement = pos=(0,0,5) rot=(0,0,1;0rad)
  Support = -> [XY_Plane025]
  sketch-geometry (7):
    g0: LineSegment StartX=-26 StartY=5 StartZ=0 EndX=-44 EndY=5 EndZ=0
    g1: LineSegment StartX=-44 StartY=5 StartZ=0 EndX=-44 EndY=-7 EndZ=0
    g2: LineSegment StartX=-44 StartY=-7 StartZ=0 EndX=-26 EndY=-7 EndZ=0
    g3: LineSegment StartX=-26 StartY=-7 StartZ=0 EndX=-26 EndY=5 EndZ=0
    g4: Circle CenterX=-39 CenterY=0 CenterZ=0 NormalX=0 NormalY=0 NormalZ=1 AngleXU=0 Radius=1.092
    g5: Circle CenterX=-31 CenterY=0 CenterZ=0 NormalX=0 NormalY=0 NormalZ=1 AngleXU=0 Radius=1.092
    g6: Circle CenterX=0 CenterY=0 CenterZ=0 NormalX=0 NormalY=0 NormalZ=1 AngleXU=0 Radius=26
  constraints (20):
    c: Horizontal(g0)
    c: Coincident(g0,g1)
    c: Coincident(g1,g2)
    c: Horizontal(g2)
    c: Coincident(g2,g3)
    c: Coincident(g3,g0)
    c: Vertical(g3)
    c: PointOnObject(g4,g-1)
    c: PointOnObject(g5,g-1)
    c: DistanceX(g4,g5) = 8
    c: Diameter(g4) = 2.184
    c: Equal(g4,g5)
    c: DistanceX(g0,g4) = 5
    c: Coincident(g6,g-1)
    c: Diameter(g6) = 52
    c: Tangent(g3,g6)
    c: DistanceX(g5,g-1) = 31
    c: DistanceY(g1,g-1) = 7
    c: DistanceY(g-1,g0) = 5
    c: Vertical(g1)
FEATURE [PartDesign::Pad] Pad062
  BaseFeature = -> Pad032
  Direction = (1,1,1)
  Length = 23.5
  Length2 = 100
  Profile = -> Sketch103
  Refine = true
  Reversed = true
  Type = 0
  expr: Length = <<var>>.J3BaseEncoderH
FEATURE [PartDesign::Body] Body012
  Group = -> [Sketch051,Pad032,Sketch103,Pad062]
  Origin = -> Origin025
  Tip = -> Pad062
FEATURE [PartDesign::CoordinateSystem] J2_plate  label="J2-plate"
  AttacherType = Attacher::AttachEngine3D
  MapMode = 11
  Placement = pos=(5.15937,0,10) rot=(0.707107,0,0.707107;3.14159rad)
  Support = -> [Pocket016]
FEATURE [App::Link] RADIUS
  AssemblyType = Asm4EE
  AttachedBy = #J2_plate
  AttachedTo = J2_PLATE#radius
  AttachmentOffset = pos=(0,0,0) rot=(0,0,1;4.71239rad)
  LinkPlacement = pos=(227.8,4.84062,205.619) rot=(0.57735,0.57735,0.57735;2.0944rad)
  LinkedObject = -> RADIUS_1_0001
  Placement = pos=(227.8,4.84062,205.619) rot=(0.57735,0.57735,0.57735;2.0944rad)
  expr: Placement = J2_PLATE.Placement * radius.Placement * AttachmentOffset * J2_plate.Placement ^ -1
FEATURE [PartDesign::CoordinateSystem] J3_base  label="J3-base"
  AttacherType = Attacher::AttachEngine3D
  MapMode = 11
  Placement = pos=(5.15937,0,262.8) rot=(0.707107,0,0.707107;3.14159rad)
  Support = -> [Pocket016]
FEATURE [App::Part] RADIUS_1_0001  label="RADIUS_2V0"
  Group = -> [LCS_0010,Body011,Page002,J2_plate,J3_base]
  Origin = -> Origin030
FEATURE [App::Link] J3_BASE
  AssemblyType = Asm4EE
  AttachedBy = #radius001
  AttachedTo = RADIUS#J3_base
  AttachmentOffset = pos=(0,0,0) rot=(0,0,1;1.5708rad)
  LinkPlacement = pos=(514.6,10,176.3) rot=(1,0,0;4.71239rad)
  LinkedObject = -> J3_BASE_2_0
  Placement = pos=(514.6,10,176.3) rot=(1,0,0;4.71239rad)
  expr: Placement = RADIUS.Placement * J3_base.Placement * AttachmentOffset * radius001.Placement ^ -1
FEATURE [PartDesign::CoordinateSystem] radius001
  AttacherType = Attacher::AttachEngine3D
  MapMode = 11
  Placement = pos=(-24,-29.3188,0) rot=(0,0,1;1.5708rad)
  Support = -> [Pad062]
FEATURE [PartDesign::CoordinateSystem] motor004
  AttacherType = Attacher::AttachEngine3D
  AttachmentOffset = pos=(0,0,0) rot=(1,0,0;3.14159rad)
  MapMode = 45
  Placement = pos=(0,1.9e-15,5) rot=(0.92388,-0.382683,0;3.14159rad)
  Support = -> [Pad062]
FEATURE [PartDesign::CoordinateSystem] LCS_0020
  AttacherType = Attacher::AttachEngine3D
  MapMode = 2
  Support = -> [X_Axis042]
FEATURE [PartDesign::CoordinateSystem] LCS_0021
  AttacherType = Attacher::AttachEngine3D
  MapMode = 2
  Support = -> [X_Axis043]
FEATURE [Sketcher::SketchObject] Sketch104
  FullyConstrained = true
  MapMode = 5
  Support = -> [XY_Plane043]
  sketch-geometry (7):
    g0: ArcOfCircle CenterX=0 CenterY=0 CenterZ=0 NormalX=0 NormalY=0 NormalZ=1 AngleXU=0 Radius=20 StartAngle=3.14159 EndAngle=6.28319
    g1: LineSegment StartX=-20 StartY=2.4e-15 StartZ=0 EndX=-20 EndY=20 EndZ=0
    g2: LineSegment StartX=-20 StartY=20 StartZ=0 EndX=20 EndY=20 EndZ=0
    g3: LineSegment StartX=20 StartY=20 StartZ=0 EndX=20 EndY=-3.91e-14 EndZ=0
    g4: Circle CenterX=0 CenterY=0 CenterZ=0 NormalX=0 NormalY=0 NormalZ=1 AngleXU=0 Radius=3.05
    g5: Circle CenterX=-15 CenterY=15 CenterZ=0 NormalX=0 NormalY=0 NormalZ=1 AngleXU=0 Radius=1.7272
    g6: Circle CenterX=15 CenterY=15 CenterZ=0 NormalX=0 NormalY=0 NormalZ=1 AngleXU=0 Radius=1.7272
  constraints (19):
    c: Coincident(g0,g-1)
    c: PointOnObject(g0,g-1)
    c: PointOnObject(g0,g-1)
    c: Tangent(g0,g1) = 1.5708
    c: Coincident(g1,g2)
    c: Horizontal(g2)
    c: Coincident(g2,g3)
    c: Coincident(g3,g0)
    c: Vertical(g3)
    c: Coincident(g4,g0)
    c: Diameter(g4) = 6.1
    c: Diameter(g0) = 40
    c: DistanceY(g1,g1) = 20
    c: Symmetric(g6,g5,g-2)
    c: Diameter(g5) = 3.4544
    c: Equal(g5,g6)
    c: DistanceY(g6,g2) = 5
    c: DistanceX(g6,g2) = 5
    c: DistanceX(g5,g6) = 30
FEATURE [Sketcher::SketchObject] Sketch105
  AttachmentOffset = pos=(0,0,5) rot=(0,0,1;0rad)
  FullyConstrained = true
  MapMode = 5
  Placement = pos=(0,0,5) rot=(0,0,1;0rad)
  Support = -> [XY_Plane043]
  sketch-geometry (8):
    g0: LineSegment StartX=-8 StartY=8 StartZ=0 EndX=8 EndY=8 EndZ=0
    g1: LineSegment StartX=8 StartY=8 StartZ=0 EndX=8 EndY=-8 EndZ=0
    g2: LineSegment StartX=8 StartY=-8 StartZ=0 EndX=-8 EndY=-8 EndZ=0
    g3: LineSegment StartX=-8 StartY=-8 StartZ=0 EndX=-8 EndY=8 EndZ=0
    g4: Circle CenterX=-8 CenterY=8 CenterZ=0 NormalX=0 NormalY=0 NormalZ=1 AngleXU=0 Radius=1.75
    g5: Circle CenterX=8 CenterY=8 CenterZ=0 NormalX=0 NormalY=0 NormalZ=1 AngleXU=0 Radius=1.75
    g6: Circle CenterX=8 CenterY=-8 CenterZ=0 NormalX=0 NormalY=0 NormalZ=1 AngleXU=0 Radius=1.75
    g7: Circle CenterX=-8 CenterY=-8 CenterZ=0 NormalX=0 NormalY=0 NormalZ=1 AngleXU=0 Radius=1.75
  constraints (18):
    c: Coincident(g0,g1)
    c: Coincident(g1,g2)
    c: Coincident(g2,g3)
    c: Coincident(g3,g0)
    c: Horizontal(g2)
    c: Vertical(g1)
    c: Symmetric(g0,g0,g-2)
    c: Symmetric(g0,g2,g-1)
    c: Equal(g3,g0)
    c: Coincident(g4,g0)
    c: Coincident(g5,g0)
    c: Coincident(g6,g1)
    c: Coincident(g7,g2)
    c: Diameter(g4) = 3.5
    c: Equal(g4,g7)
    c: Equal(g4,g6)
    c: Equal(g4,g5)
    c: DistanceY(g1,g1) = 16
FEATURE [PartDesign::Pad] Pad063
  Direction = (1,1,1)
  Length = 5
  Length2 = 100
  Profile = -> Sketch104
  Refine = true
  Type = 0
FEATURE [PartDesign::Hole] Hole008
  BaseFeature = -> Pad063
  Depth = 25
  DepthType = 1
  Diameter = 4.3
  DrillForDepth = false
  DrillPoint = 1
  DrillPointAngle = 118
  HoleCutCountersinkAngle = 82
  HoleCutCustomValues = false
  HoleCutDepth = 0
  HoleCutDiameter = 8.298
  HoleCutType = 2
  ModelActualThread = false
  Profile = -> Sketch105
  Refine = true
  Tapered = false
  TaperedAngle = 90
  ThreadAngle = 0
  ThreadClass = 0
  ThreadCutOffInner = 0
  ThreadCutOffOuter = 0
  ThreadDirection = 0
  ThreadFit = 0
  ThreadPitch = 0
  ThreadSize = 5
  ThreadType = 3
  Threaded = false
FEATURE [Sketcher::SketchObject] Sketch106
  AttachmentOffset = pos=(0,0,1.5) rot=(0,0,1;0rad)
  FullyConstrained = true
  MapMode = 5
  Placement = pos=(0,0,1.5) rot=(0,0,1;0rad)
  Support = -> [XY_Plane043]
  sketch-geometry (1):
    g0: Circle CenterX=0 CenterY=0 CenterZ=0 NormalX=0 NormalY=0 NormalZ=1 AngleXU=0 Radius=3.5
  constraints (2):
    c: Coincident(g0,g-1)
    c: Diameter(g0) = 7
FEATURE [PartDesign::Pad] Pad064
  BaseFeature = -> Hole008
  Direction = (1,1,1)
  Length = 1
  Length2 = 100
  Profile = -> Sketch106
  Refine = true
  Type = 0
FEATURE [PartDesign::Body] Body_4
  Group = -> [LCS_0021,Sketch104,Sketch105,Pad063,Hole008,Sketch106,Pad064]
  Origin = -> Origin043
  Tip = -> Pad064
FEATURE [App::Link] J3_PLATE
  AssemblyType = Asm4EE
  AttachedBy = #LCS_0020
  AttachedTo = J3_HUB_1309_0016_0006#flat
  LinkPlacement = pos=(514.6,-1,176.3) rot=(0,0.707107,-0.707107;3.14159rad)
  LinkedObject = -> J3_PLATE_1_0
  Placement = pos=(514.6,-1,176.3) rot=(0,0.707107,-0.707107;3.14159rad)
  expr: Placement = J3_HUB_1309_0016_0006.Placement * HUB_1309_0016_0006#flat.Placement * AttachmentOffset * LCS_0020.Placement ^ -1
FEATURE [PartDesign::CoordinateSystem] encoderJ3
  AttacherType = Attacher::AttachEngine3D
  MapMode = 11
  Placement = pos=(-39,0,-18.5) rot=(0,0,1;1.5708rad)
  Support = -> [Pad062]
FEATURE [App::Part] J3_BASE_2_0  label="J3_BASE_2V0"
  Group = -> [LCS_0019,Body012,radius001,motor004,encoderJ3]
  Origin = -> Origin041
FEATURE [App::Link] ENCODER_BRACKET_J3  label="ENCODER-BRACKET-J3"
  AssemblyType = Asm4EE
  AttachedBy = #base
  AttachedTo = J3_BASE#encoderJ3
  AttachmentOffset = pos=(0,0,0) rot=(0,0,1;1.5708rad)
  LinkPlacement = pos=(514.6,-8.5,176.3) rot=(0.57735,0.57735,-0.57735;2.0944rad)
  LinkedObject = -> ENCODER_BRACKET_1_001
  Placement = pos=(514.6,-8.5,176.3) rot=(0.57735,0.57735,-0.57735;2.0944rad)
  expr: Placement = J3_BASE.Placement * encoderJ3.Placement * AttachmentOffset * base.Placement ^ -1
FEATURE [PartDesign::CoordinateSystem] base
  AttacherType = Attacher::AttachEngine3D
  MapMode = 11
  Placement = pos=(0,-39,0) rot=(0.707107,-0.707107,0;3.14159rad)
  Support = -> [Hole006]
FEATURE [App::Part] ENCODER_BRACKET_1_001  label="ENCODER_BRACKET_A_1V0"
  Group = -> [LCS_0017,Body_004,base]
  Origin = -> Origin039
FEATURE [App::Link] A4_GRIPPER
  AssemblyType = Asm4EE
  AttachedBy = #A4001
  AttachedTo = J3_PLATE#gripper
  AttachmentOffset = pos=(0,0,0) rot=(0,0,1;3.14159rad)
  LinkPlacement = pos=(528.888,-28,128.54) rot=(0,0,1;0rad)
  LinkedObject = -> <external A4-GRIPPER.FCStd>#Model
  Placement = pos=(528.888,-28,128.54) rot=(0,0,1;0rad)
  expr: Placement = J3_PLATE.Placement * gripper.Placement * AttachmentOffset * A4_GRIPPER#A4001.Placement ^ -1
FEATURE [PartDesign::CoordinateSystem] gripper
  AttacherType = Attacher::AttachEngine3D
  MapMode = 11
  Placement = pos=(-15,15,5) rot=(0,0,1;1.5708rad)
  Support = -> [Pad064]
FEATURE [App::Part] J3_PLATE_1_0  label="J3_PLATE_2V0"
  Group = -> [LCS_0020,Body_4,gripper]
  Origin = -> Origin042
FEATURE [TechDraw::DrawViewDimension] Dimension
  Arbitrary = false
  ArbitraryTolerances = false
  EqualTolerance = true
  FormatSpec = %.2f
  FormatSpecOverTolerance = %+.2f
  FormatSpecUnderTolerance = %+.2f
  Inverted = false
  LockPosition = false
  MeasureType = 1
  OverTolerance = 0
  References2D = -> [ProjItem]
  Rotation = 0
  ScaleType = 0
  TheoreticalExact = false
  Type = 1
  UnderTolerance = 0
  X = -3.48601
  Y = 53.3316
FEATURE [TechDraw::DrawViewDimension] Dimension032
  Arbitrary = false
  ArbitraryTolerances = false
  EqualTolerance = true
  FormatSpec = %.2f
  FormatSpecOverTolerance = %+.2f
  FormatSpecUnderTolerance = %+.2f
  Inverted = false
  LockPosition = false
  MeasureType = 1
  OverTolerance = 0
  References2D = -> [ProjItem]
  Rotation = 0
  ScaleType = 0
  TheoreticalExact = false
  Type = 1
  UnderTolerance = 0
  X = 0
  Y = 63.7897
FEATURE [TechDraw::DrawPage] Page
  KeepUpdated = true
  NextBalloonIndex = 1
  ProjectionType = 0
  Template = -> Template
  Views = -> [ProjGroup,Dimension002,Dimension,Dimension032]
FEATURE [App::Part] RISER_1_0  label="RISER_2V0"
  Group = -> [LCS_0,Body,baseJ0,Page]
  Origin = -> Origin001
FEATURE [PartDesign::CoordinateSystem] LCS_0022
  AttacherType = Attacher::AttachEngine3D
  MapMode = 2
  Support = -> [X_Axis044]
FEATURE [PartDesign::CoordinateSystem] LCS_0023
  AttacherType = Attacher::AttachEngine3D
  MapMode = 2
  Support = -> [X_Axis045]
FEATURE [Sketcher::SketchObject] Sketch107
  FullyConstrained = true
  MapMode = 5
  Support = -> [XY_Plane045]
  sketch-geometry (5):
    g0: LineSegment StartX=-3 StartY=-21 StartZ=0 EndX=3 EndY=-21 EndZ=0
    g1: LineSegment StartX=3 StartY=-21 StartZ=0 EndX=3 EndY=4 EndZ=0
    g2: LineSegment StartX=3 StartY=4 StartZ=0 EndX=-3 EndY=4 EndZ=0
    g3: LineSegment StartX=-3 StartY=4 StartZ=0 EndX=-3 EndY=-21 EndZ=0
    g4: Circle CenterX=0 CenterY=-10 CenterZ=0 NormalX=0 NormalY=0 NormalZ=1 AngleXU=0 Radius=1.75
  constraints (14):
    c: Coincident(g0,g1)
    c: Coincident(g1,g2)
    c: Coincident(g2,g3)
    c: Coincident(g3,g0)
    c: Horizontal(g0)
    c: Vertical(g1)
    c: Vertical(g3)
    c: Symmetric(g1,g2,g-2)
    c: DistanceY(g3,g3) = 25
    c: DistanceY(g-1,g2) = 4
    c: DistanceX(g2,g2) = 6
    c: PointOnObject(g4,g-2)
    c: Diameter(g4) = 3.5
    c: DistanceY(g4,g1) = 14
FEATURE [PartDesign::Pad] Pad065
  Direction = (1,1,1)
  Length = 1.6
  Length2 = 100
  Profile = -> Sketch107
  Type = 0
FEATURE [PartDesign::Body] Body_5
  Group = -> [LCS_0023,Sketch107,Pad065]
  Origin = -> Origin045
  Tip = -> Pad065
FEATURE [App::Part] ENCODER_PCB_1_0  label="ENCODER_PCB_1V0"
  Group = -> [LCS_0022,Body_5]
  Origin = -> Origin044
FEATURE [App::Link] ENCODER_PCB_J0  label="ENCODER-PCB-J0"
  AssemblyType = Asm4EE
  AttachedBy = #LCS_0022
  AttachedTo = ENCODER_BRACKET_0#LCS_0013
  LinkPlacement = pos=(0,0,100.5) rot=(0,0,1;1.5708rad)
  LinkedObject = -> ENCODER_PCB_1_0
  Placement = pos=(0,0,100.5) rot=(0,0,1;1.5708rad)
  expr: Placement = ENCODER_BRACKET_0.Placement * LCS_0013.Placement * AttachmentOffset * LCS_0022.Placement ^ -1
FEATURE [PartDesign::CoordinateSystem] LCS_0024
  AttacherType = Attacher::AttachEngine3D
  MapMode = 2
  Support = -> [X_Axis046]
FEATURE [PartDesign::CoordinateSystem] LCS_0025
  AttacherType = Attacher::AttachEngine3D
  MapMode = 2
  Support = -> [X_Axis047]
FEATURE [Sketcher::SketchObject] Sketch108
  FullyConstrained = true
  MapMode = 5
  Support = -> [XY_Plane047]
  sketch-geometry (20):
    g0: LineSegment StartX=-41.5 StartY=-35.5 StartZ=0 EndX=41.5 EndY=-35.5 EndZ=0
    g1: LineSegment StartX=41.5 StartY=-35.5 StartZ=0 EndX=41.5 EndY=35.5 EndZ=0
    g2: LineSegment StartX=41.5 StartY=35.5 StartZ=0 EndX=-41.5 EndY=35.5 EndZ=0
    g3: LineSegment StartX=-41.5 StartY=35.5 StartZ=0 EndX=-41.5 EndY=-35.5 EndZ=0
    g4: LineSegment StartX=-37.5 StartY=31.5 StartZ=0 EndX=37.5 EndY=31.5 EndZ=0
    g5: LineSegment StartX=37.5 StartY=31.5 StartZ=0 EndX=37.5 EndY=-31.5 EndZ=0
    g6: LineSegment StartX=37.5 StartY=-31.5 StartZ=0 EndX=-37.5 EndY=-31.5 EndZ=0
    g7: LineSegment StartX=-37.5 StartY=-31.5 StartZ=0 EndX=-37.5 EndY=31.5 EndZ=0
    g8: Circle CenterX=-37.5 CenterY=31.5 CenterZ=0 NormalX=0 NormalY=0 NormalZ=1 AngleXU=0 Radius=1.95
    g9: Circle CenterX=37.5 CenterY=31.5 CenterZ=0 NormalX=0 NormalY=0 NormalZ=1 AngleXU=0 Radius=1.95
    g10: Circle CenterX=37.5 CenterY=-31.5 CenterZ=0 NormalX=0 NormalY=0 NormalZ=1 AngleXU=0 Radius=1.95
    g11: Circle CenterX=-37.5 CenterY=-31.5 CenterZ=0 NormalX=0 NormalY=0 NormalZ=1 AngleXU=0 Radius=1.95
    g12: ArcOfCircle CenterX=-37.5 CenterY=31.5 CenterZ=0 NormalX=0 NormalY=0 NormalZ=1 AngleXU=0 Radius=4 StartAngle=4.71239 EndAngle=6.28319
    g13: ArcOfCircle CenterX=37.5 CenterY=31.5 CenterZ=0 NormalX=0 NormalY=0 NormalZ=1 AngleXU=0 Radius=4 StartAngle=3.14159 EndAngle=4.71239
    g14: ArcOfCircle CenterX=37.5 CenterY=-31.5 CenterZ=0 NormalX=0 NormalY=0 NormalZ=1 AngleXU=0 Radius=4 StartAngle=1.5708 EndAngle=3.14159
    g15: ArcOfCircle CenterX=-37.5 CenterY=-31.5 CenterZ=0 NormalX=0 NormalY=0 NormalZ=1 AngleXU=0 Radius=4 StartAngle=0 EndAngle=1.5708
    g16: LineSegment StartX=-37.5 StartY=-27.5 StartZ=0 EndX=-37.5 EndY=27.5 EndZ=0
    g17: LineSegment StartX=-33.5 StartY=31.5 StartZ=0 EndX=33.5 EndY=31.5 EndZ=0
    g18: LineSegment StartX=37.5 StartY=27.5 StartZ=0 EndX=37.5 EndY=-27.5 EndZ=0
    g19: LineSegment StartX=33.5 StartY=-31.5 StartZ=0 EndX=-33.5 EndY=-31.5 EndZ=0
  constraints (52):
    c: Coincident(g0,g1)
    c: Coincident(g1,g2)
    c: Coincident(g2,g3)
    c: Coincident(g3,g0)
    c: Horizontal(g0)
    c: Vertical(g1)
    c: Symmetric(g2,g1,g-2)
    c: Symmetric(g2,g0,g-1)
    c: Coincident(g4,g5)
    c: Coincident(g5,g6)
    c: Coincident(g6,g7)
    c: Coincident(g7,g4)
    c: Horizontal(g6)
    c: Vertical(g5)
    c: DistanceY(g7,g7) = 63
    c: Symmetric(g4,g6,g-1)
    c: DistanceX(g4,g4) = 75
    c: Symmetric(g4,g4,g-2)
    c: Coincident(g8,g4)
    c: Coincident(g9,g4)
    c: Coincident(g10,g5)
    c: Coincident(g11,g6)
    c: Diameter(g11) = 3.9
    c: Equal(g11,g10)
    c: Equal(g11,g9)
    c: Equal(g11,g8)
    c: DistanceY(g8,g2) = 4
    c: DistanceX(g2,g8) = 4
    c: Coincident(g12,g8)
    c: PointOnObject(g12,g7)
    c: PointOnObject(g12,g4)
    c: Coincident(g13,g9)
    c: PointOnObject(g13,g4)
    c: PointOnObject(g13,g5)
    c: Coincident(g14,g10)
    c: PointOnObject(g14,g5)
    c: PointOnObject(g14,g6)
    c: Coincident(g15,g11)
    c: PointOnObject(g15,g6)
    c: PointOnObject(g15,g7)
    c: Coincident(g16,g15)
    c: Coincident(g16,g12)
    c: Coincident(g17,g12)
    c: Coincident(g17,g13)
    c: Coincident(g18,g13)
    c: Coincident(g18,g14)
    c: Coincident(g19,g14)
    c: Coincident(g19,g15)
    c: Diameter(g12) = 8
    c: Equal(g12,g15)
    c: Equal(g12,g13)
    c: Equal(g12,g14)
FEATURE [PartDesign::Pad] Pad066
  Direction = (1,1,1)
  Length = 4
  Length2 = 100
  Profile = -> Sketch108
  Refine = true
  Type = 0
FEATURE [Sketcher::SketchObject] Sketch109
  FullyConstrained = true
  MapMode = 5
  Support = -> [XY_Plane047]
  sketch-geometry (14):
    g0: Circle CenterX=-25 CenterY=0 CenterZ=0 NormalX=0 NormalY=0 NormalZ=1 AngleXU=0 Radius=2.25
    g1: Circle CenterX=25 CenterY=0 CenterZ=0 NormalX=0 NormalY=0 NormalZ=1 AngleXU=0 Radius=2.25
    g2: LineSegment StartX=-5 StartY=-33 StartZ=0 EndX=-5 EndY=-5 EndZ=0
    g3: LineSegment StartX=-5 StartY=-5 StartZ=0 EndX=-40 EndY=-5 EndZ=0
    g4: LineSegment StartX=-40 StartY=-5 StartZ=0 EndX=-40 EndY=5 EndZ=0
    g5: LineSegment StartX=-40 StartY=5 StartZ=0 EndX=-5 EndY=5 EndZ=0
    g6: LineSegment StartX=-5 StartY=5 StartZ=0 EndX=-5 EndY=33 EndZ=0
    g7: LineSegment StartX=-5 StartY=33 StartZ=0 EndX=5 EndY=33 EndZ=0
    g8: LineSegment StartX=5 StartY=33 StartZ=0 EndX=5 EndY=5 EndZ=0
    g9: LineSegment StartX=5 StartY=5 StartZ=0 EndX=40 EndY=5 EndZ=0
    g10: LineSegment StartX=40 StartY=5 StartZ=0 EndX=40 EndY=-5 EndZ=0
    g11: LineSegment StartX=40 StartY=-5 StartZ=0 EndX=5 EndY=-5 EndZ=0
    g12: LineSegment StartX=5 StartY=-5 StartZ=0 EndX=5 EndY=-33 EndZ=0
    g13: LineSegment StartX=5 StartY=-33 StartZ=0 EndX=-5 EndY=-33 EndZ=0
  constraints (37):
    c: PointOnObject(g0,g-1)
    c: Diameter(g1) = 4.5
    c: Equal(g1,g0)
    c: Symmetric(g0,g1,g-2)
    c: DistanceX(g0,g1) = 50
    c: Vertical(g2)
    c: Coincident(g2,g3)
    c: Horizontal(g3)
    c: Coincident(g3,g4)
    c: Coincident(g4,g5)
    c: Horizontal(g5)
    c: Coincident(g5,g6)
    c: Coincident(g6,g7)
    c: Horizontal(g7)
    c: Coincident(g7,g8)
    c: Vertical(g8)
    c: Coincident(g8,g9)
    c: Horizontal(g9)
    c: Coincident(g9,g10)
    c: Vertical(g10)
    c: Coincident(g10,g11)
    c: Horizontal(g11)
    c: Coincident(g11,g12)
    c: Vertical(g12)
    c: Coincident(g12,g13)
    c: Coincident(g13,g2)
    c: Vertical(g6)
    c: Symmetric(g4,g3,g-1)
    c: DistanceY(g4,g4) = 10
    c: Equal(g7,g4)
    c: Equal(g4,g13)
    c: Equal(g13,g10)
    c: Symmetric(g2,g12,g-2)
    c: DistanceX(g4,g9) = 80
    c: DistanceY(g2,g6) = 66
    c: Symmetric(g2,g6,g-1)
    c: Symmetric(g4,g9,g-2)
FEATURE [PartDesign::Pad] Pad067
  BaseFeature = -> Pad066
  Direction = (1,1,1)
  Length = 4
  Length2 = 100
  Profile = -> Sketch109
  Refine = true
  Type = 0
FEATURE [PartDesign::Body] Body_6
  Group = -> [LCS_0025,Sketch108,Pad066,Sketch109,Pad067]
  Origin = -> Origin047
  Tip = -> Pad067
FEATURE [App::Part] PCB_BRACKET_1_0  label="PCB_BRACKET_1V0"
  Group = -> [LCS_0024,Body_6]
  Origin = -> Origin046
FEATURE [Sketcher::SketchObject] Sketch110
  AttachmentOffset = pos=(0,0,-5) rot=(0,0,1;0rad)
  FullyConstrained = true
  MapMode = 5
  Placement = pos=(0,5,1.1e-15) rot=(1,0,0;1.5708rad)
  Support = -> [XZ_Plane008]
  sketch-geometry (9):
    g0: Circle CenterX=0 CenterY=43 CenterZ=0 NormalX=0 NormalY=0 NormalZ=1 AngleXU=0 Radius=14
    g1: LineSegment StartX=-9.89949 StartY=52.8995 StartZ=0 EndX=9.89949 EndY=52.8995 EndZ=0
    g2: LineSegment StartX=9.89949 StartY=52.8995 StartZ=0 EndX=9.89949 EndY=33.1005 EndZ=0
    g3: LineSegment StartX=9.89949 StartY=33.1005 StartZ=0 EndX=-9.89949 EndY=33.1005 EndZ=0
    g4: LineSegment StartX=-9.89949 StartY=33.1005 StartZ=0 EndX=-9.89949 EndY=52.8995 EndZ=0
    g5: Circle CenterX=-9.89949 CenterY=52.8995 CenterZ=0 NormalX=0 NormalY=0 NormalZ=1 AngleXU=0 Radius=1.5
    g6: Circle CenterX=9.89949 CenterY=52.8995 CenterZ=0 NormalX=0 NormalY=0 NormalZ=1 AngleXU=0 Radius=1.5
    g7: Circle CenterX=9.89949 CenterY=33.1005 CenterZ=0 NormalX=0 NormalY=0 NormalZ=1 AngleXU=0 Radius=1.5
    g8: Circle CenterX=-9.89949 CenterY=33.1005 CenterZ=0 NormalX=0 NormalY=0 NormalZ=1 AngleXU=0 Radius=1.5
  constraints (23):
    c: Coincident(g1,g2)
    c: Coincident(g2,g3)
    c: Coincident(g3,g4)
    c: Coincident(g4,g1)
    c: Horizontal(g1)
    c: Horizontal(g3)
    c: Vertical(g2)
    c: Vertical(g4)
    c: PointOnObject(g1,g0)
    c: PointOnObject(g2,g0)
    c: PointOnObject(g1,g0)
    c: Equal(g1,g4)
    c: Diameter(g0) = 28
    c: Coincident(g5,g1)
    c: Coincident(g6,g1)
    c: Coincident(g7,g2)
    c: Coincident(g8,g3)
    c: Diameter(g8) = 3
    c: Equal(g8,g7)
    c: Equal(g8,g6)
    c: Equal(g8,g5)
    c: PointOnObject(g0,g-2)
    c: DistanceY(g-1,g0) = 43
FEATURE [PartDesign::Hole] Hole009
  BaseFeature = -> Pad055
  Depth = 25
  DepthType = 1
  Diameter = 3.4
  DrillForDepth = false
  DrillPoint = 1
  DrillPointAngle = 118
  HoleCutCountersinkAngle = 90
  HoleCutCustomValues = false
  HoleCutDepth = 0
  HoleCutDiameter = 6.7
  HoleCutType = 7
  ModelActualThread = false
  Profile = -> Sketch110
  Refine = true
  Reversed = true
  Tapered = false
  TaperedAngle = 90
  ThreadAngle = 0
  ThreadClass = 0
  ThreadCutOffInner = 0
  ThreadCutOffOuter = 0
  ThreadDirection = 0
  ThreadFit = 0
  ThreadPitch = 0
  ThreadSize = 9
  ThreadType = 1
  Threaded = false
FEATURE [PartDesign::Body] Body003
  Group = -> [Sketch016,Pad010,Sketch019,Pad009,Sketch017,Pocket006,Sketch076,Pad049,Sketch090,Pad055,Sketch110,Hole009]
  Origin = -> Origin008
  Tip = -> Hole009
FEATURE [PartDesign::CoordinateSystem] screw001
  AttacherType = Attacher::AttachEngine3D
  MapMode = 11
  Placement = pos=(20,15,5) rot=(0,0,1;1.5708rad)
  Support = -> [Hole009]
FEATURE [App::Part] BASE_J1_1_0  label="J1_BASE_2V0"
  Group = -> [LCS_0003,Body003,motor,screw001]
  Origin = -> Origin007
FEATURE [App::Link] SCREW_8X375_1
  AssemblyType = Asm4EE
  AttachedBy = #LCS_0
  AttachedTo = BASE_J1_1_0001#screw001
  LinkPlacement = pos=(20,25,103) rot=(0,0,-1;4.71239rad)
  LinkedObject = -> <external SCREW_8X375.FCStd>#Part
  Placement = pos=(20,25,103) rot=(0,0,-1;4.71239rad)
  expr: Placement = BASE_J1_1_0001.Placement * screw001.Placement * AttachmentOffset * SCREW_8X375#LCS_0.Placement ^ -1
FEATURE [App::Link] ENCODER_PCB_J1
  AssemblyType = Asm4EE
  AttachedBy = #LCS_0022
  AttachedTo = ENCODER_BRACKET_1#LCS_0013
  LinkPlacement = pos=(1.7e-14,36.5,141) rot=(-0.281085,-0.678598,-0.678598;2.59356rad)
  LinkedObject = -> ENCODER_PCB_1_0
  Placement = pos=(1.7e-14,36.5,141) rot=(-0.281085,-0.678598,-0.678598;2.59356rad)
  expr: Placement = ENCODER_BRACKET_1.Placement * LCS_0013.Placement * AttachmentOffset * LCS_0022.Placement ^ -1
FEATURE [App::Link] SCREW_8X250_1
  AssemblyType = Asm4EE
  AttachedBy = #LCS_1
  AttachedTo = HUMERUS#plateJ1
  AttachmentOffset = pos=(0,0,1) rot=(1,0,0;3.14159rad)
  LinkPlacement = pos=(-17,31.825,159) rot=(0,0.707107,0.707107;3.14159rad)
  LinkedObject = -> <external SCREW_8X250.FCStd>#Part
  Placement = pos=(-17,31.825,159) rot=(0,0.707107,0.707107;3.14159rad)
  expr: Placement = HUMERUS.Placement * plateJ1.Placement * AttachmentOffset * SCREW_8X250#LCS_1.Placement ^ -1
FEATURE [App::Link] J3_HUB_1309_0016_0006
  AssemblyType = Asm4EE
  AttachedBy = #flat
  AttachedTo = J3_BASE#motor004
  AttachmentOffset = pos=(0,0,16) rot=(0,0,1;2.35619rad)
  LinkPlacement = pos=(509.626,1.69749,175) rot=(0,0.707107,0.707107;3.14159rad)
  LinkedObject = -> <external HUB_1309_0016_0006.FCStd>#_309_0016_0006_assembly
  Placement = pos=(509.626,1.69749,175) rot=(0,0.707107,0.707107;3.14159rad)
  expr: Placement = J3_BASE.Placement * motor004.Placement * AttachmentOffset * HUB_1309_0016_0006#flat.Placement ^ -1
FEATURE [App::Link] ENCODER_PCB_J3
  AssemblyType = Asm4EE
  AttachedBy = #LCS_0022
  AttachedTo = J3_PLATE#LCS_0020
  AttachmentOffset = pos=(0,0,7.5) rot=(0,0,1;1.5708rad)
  LinkPlacement = pos=(514.6,-8.5,176.3) rot=(0.57735,0.57735,-0.57735;2.0944rad)
  LinkedObject = -> ENCODER_PCB_1_0
  Placement = pos=(514.6,-8.5,176.3) rot=(0.57735,0.57735,-0.57735;2.0944rad)
  expr: Placement = J3_PLATE.Placement * LCS_0020.Placement * AttachmentOffset * LCS_0022.Placement ^ -1
FEATURE [App::Link] J1_HUB_1309_0016_0006
  AssemblyType = Asm4EE
  AttachedBy = #flat
  AttachedTo = BASE_J1_1_0001#motor
  AttachmentOffset = pos=(0,0,-15) rot=(1,0,0;3.14159rad)
  LinkPlacement = pos=(1.29993,22.3025,145.974) rot=(-0.57735,0.57735,-0.57735;4.18879rad)
  LinkedObject = -> <external HUB_1309_0016_0006.FCStd>#_309_0016_0006_assembly
  Placement = pos=(1.29993,22.3025,145.974) rot=(-0.57735,0.57735,-0.57735;4.18879rad)
  expr: Placement = BASE_J1_1_0001.Placement * motor.Placement * AttachmentOffset * HUB_1309_0016_0006#flat.Placement ^ -1
FEATURE [PartDesign::CoordinateSystem] screw1
  AttacherType = Attacher::AttachEngine3D
  MapMode = 11
  Placement = pos=(-28,5.3e-15,-3) rot=(0.707107,0,0.707107;3.14159rad)
  Support = -> [Hole004]
FEATURE [PartDesign::CoordinateSystem] screw2
  AttacherType = Attacher::AttachEngine3D
  MapMode = 11
  Placement = pos=(-28,30,-3) rot=(0.707107,0,0.707107;3.14159rad)
  Support = -> [Hole004]
FEATURE [App::Part] BRACKET_MOTOR_J2_1_0  label="J2_MTR_BRACKET_2V0"
  Group = -> [LCS_0006,Body006,humerus001,motor001,screw1,screw2]
  Origin = -> Origin014
FEATURE [App::DocumentObjectGroup] Parts
  Group = -> [RISER_1_0,BASE_J0_1_0,PLATE_J0_1_0,BASE_J1_1_0,HUMERUS_1_0,BRACKET_MOTOR_J2_1_0,TENSIONER_J2,BASE_J2_1_0,Body008,RADIUS_1_0001,A4_J2_CABLE_GUIDE,ENCODER_BRACKET_1_0,PLATE_J0_1_0002,PLATE_J0_1_0003,ENCODER_BRACKET_1_001,J3_BASE_2_0,J3_PLATE_1_0,ENCODER_PCB_1_0,PCB_BRACKET_1_0]
FEATURE [App::Link] SCREW_M4X40_2
  AssemblyType = Asm4EE
  AttachedBy = #LCS_0
  AttachedTo = BRACKET_MOTOR_J2_1_0001#screw2
  LinkPlacement = pos=(81,25,189) rot=(0.57735,0.57735,-0.57735;4.18879rad)
  LinkedObject = -> <external SCREW-M4X40.FCStd>#SCREW_M4X40
  Placement = pos=(81,25,189) rot=(0.57735,0.57735,-0.57735;4.18879rad)
  expr: Placement = BRACKET_MOTOR_J2_1_0001.Placement * screw2.Placement * AttachmentOffset * SCREW_M4X40#LCS_0.Placement ^ -1
FEATURE [App::Link] A4_PAINT_ROLLER_1V0
  AssemblyType = Asm4EE
  AttachedBy = #robot001
  AttachedTo = J3_PLATE#gripper
  AttachmentOffset = pos=(0,0,0) rot=(0,1,0;3.14159rad)
  LinkPlacement = pos=(549.6,-14.65,144.95) rot=(1,0,0;4.71239rad)
  LinkedObject = -> <external Paint Roller Copy/A4_PAINT_ROLLER_1V0.FCStd>#Model
  Placement = pos=(549.6,-14.65,144.95) rot=(1,0,0;4.71239rad)
  expr: Placement = J3_PLATE.Placement * gripper.Placement * AttachmentOffset * A4_PAINT_ROLLER_1V0#robot001.Placement ^ -1
FEATURE [App::Part] Model
  Configuration = 0
  Group = -> [LCS_Origin,Constraints,Variables,RISER_1_0001,BASE_J0_1_0001,HUB_545616_1,PLATE_J0_1_0001,BASE_J1_1_0001,SCREW_M4X40_SCREW_M4X40,WASHER_M6,SHAFT_J2_1_0,HUB_545616_3,PULLEY_615433_1,BALL_6_19_6,BASE_J2_1_0001,PULLEY_615432,TENSIONER_J2001,BRACKET_MOTOR_J2_1_0001,MOTOR_11HS12_0674S_PG27_E22_300,BELT_XL_180_375_BELT_XL_130_375,MOTOR_17HS13_0404S_PG27_0,BALL_6810_0,ENCODER_BRACKET_0,+23 more]
  Origin = -> Origin
  Type = Assembly4 Model

RESOLVED EXTERNAL PARTS (link-assembly join: the EXTERNAL_REF files above that resolve inside this repo's crawl, each included once):
---- part A4-GRIPPER.FCStd = doc fcstd_e0232eaa4114 ----
FCSTD DOCUMENT  (FreeCAD 0.19R24276 (Git))
Label: A4-GRIPPER
License: All rights reserved
LicenseURL: http://en.wikipedia.org/wiki/All_rights_reserved
objects: PartDesign::CoordinateSystem×12, App::Link×9, Sketcher::SketchObject×6, App::Part×5, PartDesign::Pad×4, PartDesign::Body×4, App::DocumentObjectGroup×2, PartDesign::Pocket×2, App::FeaturePython×1
note: 34 computed .brp shape members not serialized (recipe doc carries the construction recipe); baked Part::Feature solids carry a one-line shape summary decoded from their .brp
EXTERNAL_REF file=HUB-545608.FCStd obj=face2
EXTERNAL_REF file=HUB-545608.FCStd obj=_45608_assembly
EXTERNAL_REF file=HUB-545616.FCStd obj=face2
EXTERNAL_REF file=HUB-545616.FCStd obj=_45616_assembly
EXTERNAL_REF file=HUB-545608.FCStd obj=flat
EXTERNAL_REF file=MOTOR-638380.FCStd obj=LCS_0
EXTERNAL_REF file=MOTOR-638380.FCStd obj=MOTOR_638380
EXTERNAL_REF file=HUB-545616.FCStd obj=flatFace

FEATURE [PartDesign::CoordinateSystem] LCS_Origin
  AttacherType = Attacher::AttachEngine3D
  MapMode = 2
  Support = -> [X_Axis]
FEATURE [App::DocumentObjectGroup] Constraints
FEATURE [App::FeaturePython] Variables  # WARN: FeaturePython — macro-defined, semantics opaque (R4)
FEATURE [PartDesign::CoordinateSystem] LCS_0
  AttacherType = Attacher::AttachEngine3D
  MapMode = 2
  Support = -> [X_Axis001]
FEATURE [PartDesign::CoordinateSystem] LCS_0001
  AttacherType = Attacher::AttachEngine3D
  MapMode = 2
  Support = -> [X_Axis002]
FEATURE [Sketcher::SketchObject] Sketch
  FullyConstrained = true
  MapMode = 5
  Support = -> [XY_Plane002]
  sketch-geometry (15):
    g0: Circle CenterX=0 CenterY=0 CenterZ=0 NormalX=0 NormalY=0 NormalZ=1 AngleXU=0 Radius=14.2875
    g1: Circle CenterX=0 CenterY=0 CenterZ=0 NormalX=0 NormalY=0 NormalZ=1 AngleXU=0 Radius=6.35
    g2: Circle CenterX=0 CenterY=0 CenterZ=0 NormalX=0 NormalY=0 NormalZ=1 AngleXU=0 Radius=9.779
    g3: Circle CenterX=-6.9148 CenterY=6.9148 CenterZ=0 NormalX=0 NormalY=0 NormalZ=1 AngleXU=0 Radius=1.778
    g4: Circle CenterX=0 CenterY=9.779 CenterZ=0 NormalX=0 NormalY=0 NormalZ=1 AngleXU=0 Radius=1.778
    g5: Circle CenterX=6.9148 CenterY=6.9148 CenterZ=0 NormalX=0 NormalY=0 NormalZ=1 AngleXU=0 Radius=1.778
    g6: Circle CenterX=9.779 CenterY=0 CenterZ=0 NormalX=0 NormalY=0 NormalZ=1 AngleXU=0 Radius=1.778
    g7: Circle CenterX=6.9148 CenterY=-6.9148 CenterZ=0 NormalX=0 NormalY=0 NormalZ=1 AngleXU=0 Radius=1.778
    g8: Circle CenterX=0 CenterY=-9.779 CenterZ=0 NormalX=0 NormalY=0 NormalZ=1 AngleXU=0 Radius=1.778
    g9: Circle CenterX=-6.9148 CenterY=-6.9148 CenterZ=0 NormalX=0 NormalY=0 NormalZ=1 AngleXU=0 Radius=1.778
    g10: Circle CenterX=-9.779 CenterY=0 CenterZ=0 NormalX=0 NormalY=0 NormalZ=1 AngleXU=0 Radius=1.778
    g11: LineSegment StartX=-6.9148 StartY=6.9148 StartZ=0 EndX=6.9148 EndY=6.9148 EndZ=0
    g12: LineSegment StartX=6.9148 StartY=6.9148 StartZ=0 EndX=6.9148 EndY=-6.9148 EndZ=0
    g13: LineSegment StartX=6.9148 StartY=-6.9148 StartZ=0 EndX=-6.9148 EndY=-6.9148 EndZ=0
    g14: LineSegment StartX=-6.9148 StartY=-6.9148 StartZ=0 EndX=-6.9148 EndY=6.9148 EndZ=0
  constraints (38):
    c: Coincident(g0,g-1)
    c: Diameter(g0) = 28.575
    c: Coincident(g1,g0)
    c: Diameter(g1) = 12.7
    c: Coincident(g2,g0)
    c: Diameter(g2) = 19.558
    c: PointOnObject(g3,g2)
    c: PointOnObject(g4,g2)
    c: PointOnObject(g5,g2)
    c: PointOnObject(g6,g2)
    c: PointOnObject(g7,g2)
    c: PointOnObject(g8,g2)
    c: PointOnObject(g9,g2)
    c: PointOnObject(g10,g2)
    c: PointOnObject(g10,g-1)
    c: Coincident(g11,g12)
    c: Coincident(g12,g13)
    c: Coincident(g13,g14)
    c: Coincident(g14,g11)
    c: Horizontal(g11)
    c: Horizontal(g13)
    c: Vertical(g12)
    c: Coincident(g11,g3)
    c: Coincident(g12,g7)
    c: Equal(g11,g14)
    c: Coincident(g13,g9)
    c: Coincident(g5,g11)
    c: PointOnObject(g4,g-2)
    c: PointOnObject(g6,g-1)
    c: PointOnObject(g8,g-2)
    c: Diameter(g4) = 3.556
    c: Equal(g4,g3)
    c: Equal(g4,g10)
    c: Equal(g4,g9)
    c: Equal(g4,g8)
    c: Equal(g4,g7)
    c: Equal(g4,g6)
    c: Equal(g4,g5)
FEATURE [PartDesign::Pad] Pad
  Direction = (1,1,1)
  Length = 4.7752
  Length2 = 100
  Profile = -> Sketch
  Refine = true
  Type = 0
FEATURE [PartDesign::Body] Body
  Group = -> [LCS_0001,Sketch,Pad]
  Origin = -> Origin002
  Tip = -> Pad
FEATURE [PartDesign::CoordinateSystem] LCS_0002
  AttacherType = Attacher::AttachEngine3D
  MapMode = 2
  Support = -> [X_Axis003]
FEATURE [PartDesign::CoordinateSystem] LCS_0003
  AttacherType = Attacher::AttachEngine3D
  MapMode = 2
  Support = -> [X_Axis004]
FEATURE [Sketcher::SketchObject] Sketch001
  FullyConstrained = true
  MapMode = 5
  Support = -> [XY_Plane004]
  sketch-geometry (18):
    g0: Circle CenterX=0 CenterY=0 CenterZ=0 NormalX=0 NormalY=0 NormalZ=1 AngleXU=0 Radius=9.779
    g1: LineSegment StartX=-6.9148 StartY=6.9148 StartZ=0 EndX=6.9148 EndY=6.9148 EndZ=0
    g2: LineSegment StartX=6.9148 StartY=6.9148 StartZ=0 EndX=6.9148 EndY=-6.9148 EndZ=0
    g3: LineSegment StartX=6.9148 StartY=-6.9148 StartZ=0 EndX=-6.9148 EndY=-6.9148 EndZ=0
    g4: LineSegment StartX=-6.9148 StartY=-6.9148 StartZ=0 EndX=-6.9148 EndY=6.9148 EndZ=0
    g5: Circle CenterX=-6.9148 CenterY=6.9148 CenterZ=0 NormalX=0 NormalY=0 NormalZ=1 AngleXU=0 Radius=1.778
    g6: Circle CenterX=6.9148 CenterY=6.9148 CenterZ=0 NormalX=0 NormalY=0 NormalZ=1 AngleXU=0 Radius=1.778
    g7: Circle CenterX=6.9148 CenterY=-6.9148 CenterZ=0 NormalX=0 NormalY=0 NormalZ=1 AngleXU=0 Radius=1.778
    g8: Circle CenterX=-6.9148 CenterY=-6.9148 CenterZ=0 NormalX=0 NormalY=0 NormalZ=1 AngleXU=0 Radius=1.778
    g9: ArcOfCircle CenterX=0 CenterY=0 CenterZ=0 NormalX=0 NormalY=0 NormalZ=1 AngleXU=0 Radius=12.5 StartAngle=0.048599 EndAngle=4.00747
    g10: ArcOfCircle CenterX=-30.7788 CenterY=-36.179 CenterZ=0 NormalX=0 NormalY=0 NormalZ=1 AngleXU=0 Radius=35 StartAngle=5.23572 EndAngle=7.14906
    g11: ArcOfCircle CenterX=-30.7788 CenterY=-36.179 CenterZ=0 NormalX=0 NormalY=0 NormalZ=1 AngleXU=0 Radius=45 StartAngle=5.15691 EndAngle=6.33178
    g12: LineSegment StartX=12.4852 StartY=0.607249 StartZ=0 EndX=14.1681 EndY=-33.9929 EndZ=0
    g13: Circle CenterX=0 CenterY=0 CenterZ=0 NormalX=0 NormalY=0 NormalZ=1 AngleXU=0 Radius=14.2875
    g14: ArcOfCircle CenterX=-12.2875 CenterY=-68.2269 CenterZ=0 NormalX=0 NormalY=0 NormalZ=1 AngleXU=0 Radius=2 StartAngle=2.09412 EndAngle=3.14159
    g15: ArcOfCircle CenterX=-12.2875 CenterY=-75 CenterZ=0 NormalX=0 NormalY=0 NormalZ=1 AngleXU=0 Radius=2 StartAngle=3.14159 EndAngle=5.15691
    g16: LineSegment StartX=-14.2875 StartY=-75 StartZ=0 EndX=-14.2875 EndY=-68.2269 EndZ=0
    g17: LineSegment StartX=-14.2875 StartY=0 StartZ=0 EndX=-14.2875 EndY=-68.2269 EndZ=0
  constraints (44):
    c: Coincident(g0,g-1)
    c: Diameter(g0) = 19.558
    c: Coincident(g1,g2)
    c: Coincident(g2,g3)
    c: Coincident(g3,g4)
    c: Coincident(g4,g1)
    c: Horizontal(g1)
    c: Horizontal(g3)
    c: Vertical(g2)
    c: Vertical(g4)
    c: PointOnObject(g1,g0)
    c: PointOnObject(g2,g0)
    c: Equal(g1,g4)
    c: PointOnObject(g1,g0)
    c: Coincident(g5,g1)
    c: Coincident(g6,g1)
    c: Coincident(g7,g2)
    c: Coincident(g8,g3)
    c: Diameter(g7) = 3.556
    c: Equal(g7,g8)
    c: Equal(g7,g5)
    c: Equal(g7,g6)
    c: Coincident(g9,g-1)
    c: Diameter(g9) = 25
    c: Coincident(g11,g10)
    c: Tangent(g12,g11) = 1.5708
    c: Diameter(g10) = 70
    c: Diameter(g11) = 90
    c: Coincident(g13,g9)
    c: Diameter(g13) = 28.575
    c: Tangent(g9,g12) = 1.5708
    c: Tangent(g9,g10) = 1.5708
    c: Tangent(g10,g14) = 1.5708
    c: Tangent(g11,g15) = -1.5708
    c: Vertical(g16)
    c: PointOnObject(g17,g13)
    c: Coincident(g17,g14)
    c: Vertical(g17)
    c: PointOnObject(g17,g-1)
    c: Diameter(g14) = 4
    c: Equal(g14,g15)
    c: Tangent(g16,g15) = 1.5708
    c: Tangent(g16,g14) = 1.5708
    c: DistanceY(g15,g-1) = 75
FEATURE [PartDesign::Pad] Pad001
  Direction = (1,1,1)
  Length = 10
  Length2 = 100
  Profile = -> Sketch001
  Refine = true
  Type = 0
FEATURE [PartDesign::Body] Body_2
  Group = -> [LCS_0003,Sketch001,Pad001]
  Origin = -> Origin004
  Tip = -> Pad001
FEATURE [App::Part] GRIPPER_DRIVEN_1_0  label="GRIPPER-DRIVEN-1.0"
  Group = -> [LCS_0002,Body_2]
  Origin = -> Origin003
FEATURE [App::Link] GRIPPER_DRIVEN  label="GRIPPER-DRIVEN"
  AssemblyType = Asm4EE
  AttachedBy = #LCS_0002
  AttachedTo = Parent Assembly#LCS_Origin
  LinkedObject = -> GRIPPER_DRIVEN_1_0
  expr: Placement = LCS_Origin.Placement * AttachmentOffset * LCS_0002.Placement ^ -1
FEATURE [App::Link] GEAR_RHA32_36_36001  label="GEAR-RHA32-36-037"
  AssemblyType = Asm4EE
  AttachedBy = #LCS_0
  AttachedTo = GRIPPER_DRIVEN#LCS_0002
  AttachmentOffset = pos=(0,0,10) rot=(0,0,1;0rad)
  LinkPlacement = pos=(0,0,10) rot=(0,0,1;0rad)
  LinkedObject = -> GEAR_RHA32_36_36
  Placement = pos=(0,0,10) rot=(0,0,1;0rad)
  expr: Placement = GRIPPER_DRIVEN.Placement * LCS_0002.Placement * AttachmentOffset * LCS_0.Placement ^ -1
FEATURE [App::Link] GEAR_RHA32_36_36002  label="GEAR-RHA32-36-038"
  AssemblyType = Asm4EE
  AttachedBy = #LCS_0
  AttachedTo = GEAR_RHA32_36_36001#LCS_0
  AttachmentOffset = pos=(-28.575,0,0) rot=(0,0,1;0rad)
  LinkPlacement = pos=(-28.575,0,10) rot=(0,0,1;0rad)
  LinkedObject = -> GEAR_RHA32_36_36
  Placement = pos=(-28.575,0,10) rot=(0,0,1;0rad)
  expr: Placement = GEAR_RHA32_36_36001.Placement * LCS_0.Placement * AttachmentOffset * LCS_0.Placement ^ -1
FEATURE [App::Link] GRIPPER_DRIVEN_1_0001  label="GRIPPER-DRIVEN-1.001"
  AssemblyType = Asm4EE
  AttachedBy = #LCS_0002
  AttachedTo = GEAR_RHA32_36_36002#LCS_0
  AttachmentOffset = pos=(0,0,0) rot=(0,1,0;3.14159rad)
  LinkPlacement = pos=(-28.575,0,10) rot=(0,1,0;3.14159rad)
  LinkedObject = -> GRIPPER_DRIVEN_1_0
  Placement = pos=(-28.575,0,10) rot=(0,1,0;3.14159rad)
  expr: Placement = GEAR_RHA32_36_36002.Placement * LCS_0.Placement * AttachmentOffset * LCS_0002.Placement ^ -1
FEATURE [App::Link] HUB_545608_1
  AssemblyType = Asm4EE
  AttachedBy = #face2
  AttachedTo = GEAR_RHA32_36_36001#face2
  AttachmentOffset = pos=(0,0,0) rot=(0,1,0;3.14159rad)
  LinkPlacement = pos=(14.3607,-49.1577,-4.11336) rot=(-0.57735,0.57735,0.57735;4.18879rad)
  LinkedObject = -> <external HUB-545608.FCStd>#_45608_assembly
  Placement = pos=(14.3607,-49.1577,-4.11336) rot=(-0.57735,0.57735,0.57735;4.18879rad)
  expr: Placement = GEAR_RHA32_36_36001.Placement * face2.Placement * AttachmentOffset * HUB_545608#face2.Placement ^ -1
FEATURE [PartDesign::CoordinateSystem] face2
  AttacherType = Attacher::AttachEngine3D
  MapMode = 11
  Placement = pos=(0,0,4.7752) rot=(0,0,1;1.5708rad)
  Support = -> [Pad]
FEATURE [App::Part] GEAR_RHA32_36_36  label="GEAR-RHA32-36-36"
  Group = -> [LCS_0,Body,face2]
  Origin = -> Origin001
FEATURE [App::Link] HUB_545616
  AssemblyType = Asm4EE
  AttachedBy = #face2
  AttachedTo = GEAR_RHA32_36_36002#face2
  AttachmentOffset = pos=(0,0,0) rot=(0,0,1;4.71239rad)
  LinkPlacement = pos=(-45.6648,21.6153,21.2962) rot=(-0.57735,-0.57735,-0.57735;4.18879rad)
  LinkedObject = -> <external HUB-545616.FCStd>#_45616_assembly
  Placement = pos=(-45.6648,21.6153,21.2962) rot=(-0.57735,-0.57735,-0.57735;4.18879rad)
  expr: Placement = GEAR_RHA32_36_36002.Placement * face2.Placement * AttachmentOffset * HUB_545616#face2.Placement ^ -1
FEATURE [App::Link] MOTOR_638380
  AssemblyType = Asm4EE
  AttachedBy = #LCS_0
  AttachedTo = HUB_545608_1#flat
  AttachmentOffset = pos=(0,0,9) rot=(1,0,0;3.14159rad)
  LinkPlacement = pos=(7e-16,-7e-16,30.7602) rot=(-0.707107,-0.707107,0;3.14159rad)
  LinkedObject = -> <external MOTOR-638380.FCStd>#MOTOR_638380
  Placement = pos=(7e-16,-7e-16,30.7602) rot=(-0.707107,-0.707107,0;3.14159rad)
  expr: Placement = HUB_545608_1.Placement * HUB_545608#flat.Placement * AttachmentOffset * MOTOR_638380#LCS_0.Placement ^ -1
FEATURE [PartDesign::CoordinateSystem] LCS_0004
  AttacherType = Attacher::AttachEngine3D
  MapMode = 2
  Support = -> [X_Axis005]
FEATURE [PartDesign::CoordinateSystem] LCS_0005
  AttacherType = Attacher::AttachEngine3D
  MapMode = 2
  Support = -> [X_Axis006]
FEATURE [Sketcher::SketchObject] Sketch002
  FullyConstrained = true
  MapMode = 5
  Support = -> [XY_Plane006]
  sketch-geometry (10):
    g0: Circle CenterX=0 CenterY=0 CenterZ=0 NormalX=0 NormalY=0 NormalZ=1 AngleXU=0 Radius=4
    g1: Circle CenterX=7.5 CenterY=0 CenterZ=0 NormalX=0 NormalY=0 NormalZ=1 AngleXU=0 Radius=1.45
    g2: Circle CenterX=-7.5 CenterY=0 CenterZ=0 NormalX=0 NormalY=0 NormalZ=1 AngleXU=0 Radius=1.45
    g3: Circle CenterX=-28.575 CenterY=0 CenterZ=0 NormalX=0 NormalY=0 NormalZ=1 AngleXU=0 Radius=3.05
    g4: LineSegment StartX=-34.2875 StartY=22 StartZ=0 EndX=5.7125 EndY=22 EndZ=0
    g5: LineSegment StartX=5.7125 StartY=22 StartZ=0 EndX=12.1902 EndY=4.51652 EndZ=0
    g6: LineSegment StartX=-2.4e-15 StartY=-13 StartZ=0 EndX=-28.575 EndY=-13 EndZ=0
    g7: LineSegment StartX=-40.7652 StartY=4.51652 StartZ=0 EndX=-34.2875 EndY=22 EndZ=0
    g8: ArcOfCircle CenterX=0 CenterY=0 CenterZ=0 NormalX=0 NormalY=0 NormalZ=1 AngleXU=0 Radius=13 StartAngle=4.71239 EndAngle=6.63801
    g9: ArcOfCircle CenterX=-28.575 CenterY=0 CenterZ=0 NormalX=0 NormalY=0 NormalZ=1 AngleXU=0 Radius=13 StartAngle=2.78677 EndAngle=4.71239
  constraints (24):
    c: Coincident(g0,g-1)
    c: PointOnObject(g1,g-1)
    c: Diameter(g0) = 8
    c: DistanceX(g2,g1) = 15
    c: Diameter(g2) = 2.9
    c: Equal(g2,g1)
    c: Symmetric(g2,g1,g-2)
    c: PointOnObject(g3,g-1)
    c: Diameter(g3) = 6.1
    c: DistanceX(g3,g-1) = 28.575
    c: Coincident(g4,g5)
    c: Coincident(g7,g4)
    c: Horizontal(g4)
    c: Horizontal(g6)
    c: DistanceY(g-1,g4) = 22
    c: Tangent(g6,g8) = 1.5708
    c: Tangent(g5,g8) = 1.5708
    c: Tangent(g7,g9) = 1.5708
    c: Tangent(g6,g9) = 1.5708
    c: DistanceX(g4,g4) = 40
    c: Coincident(g8,g0)
    c: Coincident(g9,g3)
    c: Diameter(g8) = 26
    c: Horizontal(g7,g5)
FEATURE [PartDesign::Pad] Pad002
  Direction = (1,1,1)
  Length = 10
  Length2 = 100
  Profile = -> Sketch002
  Refine = true
  Type = 0
FEATURE [Sketcher::SketchObject] Sketch003
  AttachmentOffset = pos=(0,0,3) rot=(0,0,1;0rad)
  FullyConstrained = true
  MapMode = 5
  Placement = pos=(0,0,3) rot=(0,0,1;0rad)
  Support = -> [XY_Plane006]
  sketch-geometry (1):
    g0: Circle CenterX=0 CenterY=0 CenterZ=0 NormalX=0 NormalY=0 NormalZ=1 AngleXU=0 Radius=10.5
  constraints (2):
    c: Coincident(g0,g-1)
    c: Diameter(g0) = 21
FEATURE [PartDesign::Pocket] Pocket
  BaseFeature = -> Pad002
  Length = 7
  Length2 = 100
  Profile = -> Sketch003
  Refine = true
  Reversed = true
  Type = 0
FEATURE [Sketcher::SketchObject] Sketch004
  AttachmentOffset = pos=(0,0,-22) rot=(0,0,1;0rad)
  FullyConstrained = true
  MapMode = 5
  Placement = pos=(0,22,-4.9e-15) rot=(1,0,0;1.5708rad)
  Support = -> [XZ_Plane006]
  sketch-geometry (2):
    g0: Circle CenterX=-29.2875 CenterY=5 CenterZ=0 NormalX=0 NormalY=0 NormalZ=1 AngleXU=0 Radius=1.7
    g1: Circle CenterX=0.7125 CenterY=5 CenterZ=0 NormalX=0 NormalY=0 NormalZ=1 AngleXU=0 Radius=1.7
  constraints (6):
    c: Diameter(g1) = 3.4
    c: Equal(g1,g0)
    c: DistanceY(g-1,g0) = 5
    c: DistanceX(g0,g1) = 30
    c: Horizontal(g0,g1)
    c: DistanceX(g0,g-1) = 29.2875
FEATURE [PartDesign::Pocket] Pocket001
  BaseFeature = -> Pocket
  Length = 5
  Length2 = 100
  Profile = -> Sketch004
  Refine = true
  Reversed = true
  Type = 0
FEATURE [PartDesign::Body] Body_3
  Group = -> [LCS_0005,Sketch002,Pad002,Sketch003,Pocket,Sketch004,Pocket001]
  Origin = -> Origin006
  Tip = -> Pocket001
FEATURE [App::Link] BASE
  AssemblyType = Asm4EE
  AttachedBy = #LCS_0004
  AttachedTo = MOTOR_638380#LCS_0
  AttachmentOffset = pos=(0,0,3) rot=(-0.707107,-0.707107,0;3.14159rad)
  LinkPlacement = pos=(8e-16,-5e-16,27.7602) rot=(0,0,1;0rad)
  LinkedObject = -> BASE_1_0
  Placement = pos=(8e-16,-5e-16,27.7602) rot=(0,0,1;0rad)
  expr: Placement = MOTOR_638380.Placement * MOTOR_638380#LCS_0.Placement * AttachmentOffset * LCS_0004.Placement ^ -1
FEATURE [PartDesign::CoordinateSystem] LCS_0006
  AttacherType = Attacher::AttachEngine3D
  MapMode = 2
  Support = -> [X_Axis007]
FEATURE [PartDesign::CoordinateSystem] LCS_0007
  AttacherType = Attacher::AttachEngine3D
  MapMode = 2
  Support = -> [X_Axis008]
FEATURE [Sketcher::SketchObject] Sketch005
  FullyConstrained = true
  MapMode = 5
  Support = -> [XY_Plane008]
  sketch-geometry (2):
    g0: Circle CenterX=0 CenterY=0 CenterZ=0 NormalX=0 NormalY=0 NormalZ=1 AngleXU=0 Radius=3.25
    g1: Circle CenterX=0 CenterY=0 CenterZ=0 NormalX=0 NormalY=0 NormalZ=1 AngleXU=0 Radius=7.5
  constraints (4):
    c: Coincident(g0,g-1)
    c: Coincident(g1,g0)
    c: Diameter(g0) = 6.5
    c: Diameter(g1) = 15
FEATURE [PartDesign::Pad] Pad003
  Direction = (1,1,1)
  Length = 6
  Length2 = 100
  Profile = -> Sketch005
  Refine = true
  Type = 0
FEATURE [PartDesign::Body] Body_4
  Group = -> [LCS_0007,Sketch005,Pad003]
  Origin = -> Origin008
  Tip = -> Pad003
FEATURE [App::Part] SPACER_1_0
  Group = -> [LCS_0006,Body_4]
  Origin = -> Origin007
FEATURE [App::Link] SPACER
  AssemblyType = Asm4EE
  AttachedBy = #LCS_0006
  AttachedTo = HUB_545616#flatFace
  LinkPlacement = pos=(-28.575,0,21.7602) rot=(0,0,1;0rad)
  LinkedObject = -> SPACER_1_0
  Placement = pos=(-28.575,0,21.7602) rot=(0,0,1;0rad)
  expr: Placement = HUB_545616.Placement * HUB_545616#flatFace.Placement * AttachmentOffset * LCS_0006.Placement ^ -1
FEATURE [PartDesign::CoordinateSystem] A4
  AttacherType = Attacher::AttachEngine3D
  MapMode = 11
  Placement = pos=(0.7125,22,5) rot=(0.57735,-0.57735,0.57735;2.0944rad)
  Support = -> [Pocket001]
FEATURE [App::Part] BASE_1_0
  Group = -> [LCS_0004,Body_3,A4]
  Origin = -> Origin005
FEATURE [App::DocumentObjectGroup] Parts
  Group = -> [GEAR_RHA32_36_36,GRIPPER_DRIVEN_1_0,BASE_1_0,SPACER_1_0]
FEATURE [PartDesign::CoordinateSystem] A4001
  AttacherType = Attacher::AttachEngine3D
  Placement = pos=(0.7125,22,32.7602) rot=(-0.57735,0.57735,-0.57735;4.18879rad)
  expr: Placement = BASE.Placement * A4.Placement * AttachmentOffset
FEATURE [App::Part] Model
  Configuration = 0
  Group = -> [LCS_Origin,Constraints,Variables,GRIPPER_DRIVEN,GEAR_RHA32_36_36001,GEAR_RHA32_36_36002,GRIPPER_DRIVEN_1_0001,HUB_545608_1,HUB_545616,MOTOR_638380,BASE,SPACER,A4001]
  Origin = -> Origin
  Type = Assembly4 Model
---- part BALL-6-19-6.FCStd = doc fcstd_6a3dce6bbafe ----
FCSTD DOCUMENT  (FreeCAD 0.19R24276 (Git))
Label: BALL-6-19-6
License: All rights reserved
LicenseURL: http://en.wikipedia.org/wiki/All_rights_reserved
objects: PartDesign::CoordinateSystem×3, Sketcher::SketchObject×1, PartDesign::Pad×1, PartDesign::Body×1, App::Part×1
note: 7 computed .brp shape members not serialized (recipe doc carries the construction recipe); baked Part::Feature solids carry a one-line shape summary decoded from their .brp

FEATURE [PartDesign::CoordinateSystem] LCS_0
  AttacherType = Attacher::AttachEngine3D
  MapMode = 2
  Support = -> [X_Axis]
FEATURE [PartDesign::CoordinateSystem] LCS_0001
  AttacherType = Attacher::AttachEngine3D
  MapMode = 2
  Support = -> [X_Axis001]
FEATURE [Sketcher::SketchObject] Sketch
  FullyConstrained = false
  MapMode = 5
  Support = -> [XY_Plane001]
  sketch-geometry (2):
    g0: Circle CenterX=0 CenterY=0 CenterZ=0 NormalX=0 NormalY=0 NormalZ=1 AngleXU=0 Radius=3
    g1: Circle CenterX=0 CenterY=0 CenterZ=0 NormalX=0 NormalY=0 NormalZ=1 AngleXU=0 Radius=9.5
  constraints (4):
    c: Coincident(g0,g-1)
    c: Coincident(g1,g0)
    c: Diameter(g0) = 6
    c: Diameter(g1) = 19
FEATURE [PartDesign::Pad] Pad
  Direction = (1,1,1)
  Length = 6
  Length2 = 100
  Profile = -> Sketch
  Refine = true
  Type = 0
FEATURE [PartDesign::Body] Body
  Group = -> [LCS_0001,Sketch,Pad]
  Origin = -> Origin001
  Tip = -> Pad
FEATURE [PartDesign::CoordinateSystem] LCS_1
  AttacherType = Attacher::AttachEngine3D
  MapMode = 11
  Placement = pos=(0,0,6) rot=(0,0,1;1.5708rad)
  Support = -> [Pad]
FEATURE [App::Part] Part
  Group = -> [LCS_0,Body,LCS_1]
  Origin = -> Origin
---- part BALL-6808.FCStd = doc fcstd_b63e6a0ef98f ----
FCSTD DOCUMENT  (FreeCAD 0.19R24276 (Git))
Label: BALL-6808
License: All rights reserved
LicenseURL: http://en.wikipedia.org/wiki/All_rights_reserved
objects: Sketcher::SketchObject×1, PartDesign::Pad×1, PartDesign::Body×1, PartDesign::CoordinateSystem×1, App::Part×1
note: 5 computed .brp shape members not serialized (recipe doc carries the construction recipe); baked Part::Feature solids carry a one-line shape summary decoded from their .brp

FEATURE [Sketcher::SketchObject] Sketch
  FullyConstrained = true
  MapMode = 5
  Support = -> [XY_Plane]
  sketch-geometry (2):
    g0: Circle CenterX=0 CenterY=0 CenterZ=0 NormalX=0 NormalY=0 NormalZ=1 AngleXU=0 Radius=20
    g1: Circle CenterX=0 CenterY=0 CenterZ=0 NormalX=0 NormalY=0 NormalZ=1 AngleXU=0 Radius=26
  constraints (4):
    c: Coincident(g0,g-1)
    c: Coincident(g1,g0)
    c: Diameter(g0) = 40
    c: Diameter(g1) = 52
FEATURE [PartDesign::Pad] Pad
  Direction = (1,1,1)
  Length = 7
  Length2 = 100
  Profile = -> Sketch
  Refine = true
  Type = 0
FEATURE [PartDesign::Body] Body
  Group = -> [Sketch,Pad]
  Origin = -> Origin
  Tip = -> Pad
FEATURE [PartDesign::CoordinateSystem] LCS_0
  AttacherType = Attacher::AttachEngine3D
  MapMode = 2
  Support = -> [X_Axis001]
FEATURE [App::Part] Part
  Group = -> [LCS_0,Body]
  Origin = -> Origin001
---- part BALL-6810.FCStd = doc fcstd_cf82c9359e65 ----
FCSTD DOCUMENT  (FreeCAD 0.19R24276 (Git))
Label: BALL-6810
License: All rights reserved
LicenseURL: http://en.wikipedia.org/wiki/All_rights_reserved
objects: Sketcher::SketchObject×1, PartDesign::Pad×1, PartDesign::Body×1, PartDesign::CoordinateSystem×1, App::Part×1
note: 5 computed .brp shape members not serialized (recipe doc carries the construction recipe); baked Part::Feature solids carry a one-line shape summary decoded from their .brp

FEATURE [Sketcher::SketchObject] Sketch
  FullyConstrained = true
  MapMode = 5
  Support = -> [XY_Plane]
  sketch-geometry (2):
    g0: Circle CenterX=0 CenterY=0 CenterZ=0 NormalX=0 NormalY=0 NormalZ=1 AngleXU=0 Radius=25
    g1: Circle CenterX=0 CenterY=0 CenterZ=0 NormalX=0 NormalY=0 NormalZ=1 AngleXU=0 Radius=32.5
  constraints (4):
    c: Coincident(g0,g-1)
    c: Coincident(g1,g0)
    c: Diameter(g0) = 50
    c: Diameter(g1) = 65
FEATURE [PartDesign::Pad] Pad
  Direction = (1,1,1)
  Length = 7
  Length2 = 100
  Profile = -> Sketch
  Refine = true
  Type = 0
FEATURE [PartDesign::Body] Body
  Group = -> [Sketch,Pad]
  Origin = -> Origin
  Tip = -> Pad
FEATURE [PartDesign::CoordinateSystem] LCS_0
  AttacherType = Attacher::AttachEngine3D
  MapMode = 2
  Support = -> [X_Axis001]
FEATURE [App::Part] Part
  Group = -> [LCS_0,Body]
  Origin = -> Origin001
---- part BELT-XL-180-375.FCStd = doc fcstd_24f635ec6518 ----
FCSTD DOCUMENT  (FreeCAD 0.19R24276 (Git))
Label: BELT-XL-180-375
License: All rights reserved
LicenseURL: http://en.wikipedia.org/wiki/All_rights_reserved
objects: Sketcher::SketchObject×1, PartDesign::Pad×1, PartDesign::CoordinateSystem×1, PartDesign::Body×1
note: 5 computed .brp shape members not serialized (recipe doc carries the construction recipe); baked Part::Feature solids carry a one-line shape summary decoded from their .brp

FEATURE [Sketcher::SketchObject] Sketch
  FullyConstrained = false
  MapMode = 5
  Support = -> [XY_Plane]
  expr: Constraints[7] = 25.4 * 0.955
  expr: Constraints[8] = (18 * 25.4 - 0.955 * 25.4 * pi) / 2
  sketch-geometry (12):
    g0: ArcOfCircle CenterX=0 CenterY=0 CenterZ=0 NormalX=0 NormalY=0 NormalZ=1 AngleXU=0 Radius=12.1285 StartAngle=1.5708 EndAngle=4.71239
    g1: ArcOfCircle CenterX=190.497 CenterY=-6e-16 CenterZ=0 NormalX=0 NormalY=0 NormalZ=1 AngleXU=0 Radius=12.1285 StartAngle=4.71239 EndAngle=7.85398
    g2: LineSegment StartX=0 StartY=-12.1285 StartZ=0 EndX=190.497 EndY=-12.1285 EndZ=0
    g3: LineSegment StartX=-3.9565e-12 StartY=12.1285 StartZ=0 EndX=190.497 EndY=12.1285 EndZ=0
    g4: ArcOfCircle CenterX=0 CenterY=0 CenterZ=0 NormalX=0 NormalY=0 NormalZ=1 AngleXU=0 Radius=10.6285 StartAngle=1.5708 EndAngle=4.71239
    g5: ArcOfCircle CenterX=190.497 CenterY=-6e-16 CenterZ=0 NormalX=0 NormalY=0 NormalZ=1 AngleXU=0 Radius=10.6285 StartAngle=4.71239 EndAngle=7.85398
    g6: LineSegment StartX=0 StartY=-10.6285 StartZ=0 EndX=190.497 EndY=-10.6285 EndZ=0
    g7: LineSegment StartX=-1.3e-15 StartY=10.6285 StartZ=0 EndX=190.497 EndY=10.6285 EndZ=0
    g8: ArcOfCircle CenterX=0 CenterY=0 CenterZ=0 NormalX=0 NormalY=0 NormalZ=1 AngleXU=0 Radius=13.6285 StartAngle=1.5708 EndAngle=4.71239
    g9: ArcOfCircle CenterX=190.497 CenterY=-6e-16 CenterZ=0 NormalX=0 NormalY=0 NormalZ=1 AngleXU=0 Radius=13.6285 StartAngle=4.71239 EndAngle=7.85398
    g10: LineSegment StartX=0 StartY=-13.6285 StartZ=0 EndX=190.497 EndY=-13.6285 EndZ=0
    g11: LineSegment StartX=-1.7e-15 StartY=13.6285 StartZ=0 EndX=190.497 EndY=13.6285 EndZ=0
  constraints (25):
    c: Tangent(g0,g3)
    c: Tangent(g0,g2)
    c: Tangent(g2,g1)
    c: Tangent(g3,g1)
    c: Horizontal(g2)
    c: Equal(g0,g1)
    c: Coincident(g0,g-1)
    c: Diameter(g0) = 24.257
    c: DistanceX(g3,g3) = 190.497
    c: Tangent(g4,g7)
    c: Tangent(g4,g6)
    c: Tangent(g6,g5)
    c: Tangent(g7,g5)
    c: Horizontal(g6)
    c: Coincident(g4,g-1)
    c: Coincident(g1,g5)
    c: Tangent(g8,g11)
    c: Tangent(g8,g10)
    c: Tangent(g10,g9)
    c: Tangent(g11,g9)
    c: Horizontal(g10)
    c: Coincident(g8,g4)
    c: Coincident(g9,g5)
    c: DistanceY(g5,g1) = 1.5
    c: DistanceY(g1,g9) = 1.5
FEATURE [PartDesign::Pad] Pad
  Direction = (1,1,1)
  Length = 9.525
  Length2 = 100
  Profile = -> Sketch
  Type = 0
FEATURE [PartDesign::CoordinateSystem] LCS_1
  AttacherType = Attacher::AttachEngine3D
  MapMode = 11
  Placement = pos=(0,0,0) rot=(0,0,1;3.14159rad)
  Support = -> [Pad]
FEATURE [PartDesign::Body] Body  label="BELT-XL-130-375"
  Group = -> [Sketch,Pad,LCS_1]
  Origin = -> Origin
  Tip = -> Pad
---- part MOTOR-11HS12-0674S-PG27-E22-300.FCStd = doc fcstd_4ec9924d8d61 ----
FCSTD DOCUMENT  (FreeCAD 0.19R24276 (Git))
Label: MOTOR-11HS12-0674S-PG27-E22-300
License: All rights reserved
LicenseURL: http://en.wikipedia.org/wiki/All_rights_reserved
objects: Sketcher::SketchObject×6, PartDesign::Pad×5, PartDesign::Pocket×1, PartDesign::CoordinateSystem×1, PartDesign::Body×1
note: 20 computed .brp shape members not serialized (recipe doc carries the construction recipe); baked Part::Feature solids carry a one-line shape summary decoded from their .brp

FEATURE [Sketcher::SketchObject] Sketch
  FullyConstrained = false
  MapMode = 5
  Support = -> [XY_Plane]
  sketch-geometry (4):
    g0: LineSegment StartX=-14.1 StartY=14.1 StartZ=0 EndX=14.1 EndY=14.1 EndZ=0
    g1: LineSegment StartX=14.1 StartY=14.1 StartZ=0 EndX=14.1 EndY=-14.1 EndZ=0
    g2: LineSegment StartX=14.1 StartY=-14.1 StartZ=0 EndX=-14.1 EndY=-14.1 EndZ=0
    g3: LineSegment StartX=-14.1 StartY=-14.1 StartZ=0 EndX=-14.1 EndY=14.1 EndZ=0
  constraints (10):
    c: Coincident(g0,g1)
    c: Coincident(g1,g2)
    c: Coincident(g2,g3)
    c: Coincident(g3,g0)
    c: Horizontal(g2)
    c: Vertical(g1)
    c: Symmetric(g0,g0,g-2)
    c: Symmetric(g0,g2,g-1)
    c: Equal(g0,g3)
    c: DistanceX(g0,g0) = 28.2
FEATURE [PartDesign::Pad] Pad
  AllowMultiFace = false
  Direction = (1,1,1)
  Length = 32
  Length2 = 100
  Profile = -> Sketch
  Type = 0
FEATURE [Sketcher::SketchObject] Sketch002
  FullyConstrained = false
  MapMode = 5
  Placement = pos=(0,0,32) rot=(0,0,1;0rad)
  sketch-geometry (1):
    g0: Circle CenterX=0 CenterY=0 CenterZ=0 NormalX=0 NormalY=0 NormalZ=1 AngleXU=0 Radius=14
  constraints (2):
    c: Coincident(g0,g-1)
    c: Diameter(g0) = 28
FEATURE [PartDesign::Pad] Pad001
  AllowMultiFace = false
  BaseFeature = -> Pad
  Direction = (1,1,1)
  Length = 35
  Length2 = 100
  Profile = -> Sketch002
  Type = 0
FEATURE [Sketcher::SketchObject] Sketch003
  AttachmentOffset = pos=(0,0,67) rot=(0,0,1;0rad)
  FullyConstrained = false
  MapMode = 5
  Placement = pos=(0,0,67) rot=(0,0,1;0rad)
  Support = -> [XY_Plane]
  sketch-geometry (1):
    g0: Circle CenterX=0 CenterY=0 CenterZ=0 NormalX=0 NormalY=0 NormalZ=1 AngleXU=0 Radius=9
  constraints (2):
    c: Coincident(g0,g-1)
    c: Diameter(g0) = 18
FEATURE [PartDesign::Pad] Pad002
  BaseFeature = -> Pad001
  Direction = (1,1,1)
  Length = 2
  Length2 = 100
  Profile = -> Sketch003
  Type = 0
FEATURE [Sketcher::SketchObject] Sketch004
  AttachmentOffset = pos=(0,0,69) rot=(0,0,1;0rad)
  FullyConstrained = false
  MapMode = 5
  Placement = pos=(0,0,69) rot=(0,0,1;0rad)
  Support = -> [XY_Plane]
  sketch-geometry (1):
    g0: Circle CenterX=0 CenterY=0 CenterZ=0 NormalX=0 NormalY=0 NormalZ=1 AngleXU=0 Radius=3
  constraints (2):
    c: Coincident(g0,g-1)
    c: Diameter(g0) = 6
FEATURE [PartDesign::Pad] Pad003
  BaseFeature = -> Pad002
  Direction = (1,1,1)
  Length = 16
  Length2 = 100
  Profile = -> Sketch004
  Type = 0
FEATURE [Sketcher::SketchObject] Sketch005
  FullyConstrained = false
  MapMode = 5
  Support = -> [XY_Plane]
  sketch-geometry (1):
    g0: Circle CenterX=0 CenterY=0 CenterZ=0 NormalX=0 NormalY=0 NormalZ=1 AngleXU=0 Radius=11
  constraints (2):
    c: Coincident(g0,g-1)
    c: Diameter(g0) = 22
FEATURE [PartDesign::Pad] Pad004
  BaseFeature = -> Pad003
  Direction = (1,1,1)
  Length = 14
  Length2 = 100
  Profile = -> Sketch005
  Reversed = true
  Type = 0
FEATURE [Sketcher::SketchObject] Sketch006
  AttachmentOffset = pos=(0,0,67) rot=(0,0,1;0.785398rad)
  FullyConstrained = true
  MapMode = 5
  Placement = pos=(0,0,67) rot=(0,0,1;0.785398rad)
  Support = -> [XY_Plane]
  sketch-geometry (9):
    g0: Circle CenterX=0 CenterY=0 CenterZ=0 NormalX=0 NormalY=0 NormalZ=1 AngleXU=0 Radius=11
    g1: LineSegment StartX=-7.77817 StartY=7.77817 StartZ=0 EndX=7.77817 EndY=7.77817 EndZ=0
    g2: LineSegment StartX=7.77817 StartY=7.77817 StartZ=0 EndX=7.77817 EndY=-7.77817 EndZ=0
    g3: LineSegment StartX=7.77817 StartY=-7.77817 StartZ=0 EndX=-7.77817 EndY=-7.77817 EndZ=0
    g4: LineSegment StartX=-7.77817 StartY=-7.77817 StartZ=0 EndX=-7.77817 EndY=7.77817 EndZ=0
    g5: Circle CenterX=-7.77817 CenterY=7.77817 CenterZ=0 NormalX=0 NormalY=0 NormalZ=1 AngleXU=0 Radius=1.5
    g6: Circle CenterX=7.77817 CenterY=7.77817 CenterZ=0 NormalX=0 NormalY=0 NormalZ=1 AngleXU=0 Radius=1.5
    g7: Circle CenterX=7.77817 CenterY=-7.77817 CenterZ=0 NormalX=0 NormalY=0 NormalZ=1 AngleXU=0 Radius=1.5
    g8: Circle CenterX=-7.77817 CenterY=-7.77817 CenterZ=0 NormalX=0 NormalY=0 NormalZ=1 AngleXU=0 Radius=1.5
  constraints (22):
    c: Coincident(g0,g-1)
    c: Diameter(g0) = 22
    c: Coincident(g1,g2)
    c: Coincident(g2,g3)
    c: Coincident(g3,g4)
    c: Coincident(g4,g1)
    c: Horizontal(g1)
    c: Horizontal(g3)
    c: Vertical(g2)
    c: Vertical(g4)
    c: PointOnObject(g1,g0)
    c: PointOnObject(g2,g0)
    c: Equal(g1,g4)
    c: PointOnObject(g1,g0)
    c: Coincident(g5,g1)
    c: Coincident(g6,g1)
    c: Coincident(g7,g2)
    c: Coincident(g8,g3)
    c: Diameter(g8) = 3
    c: Equal(g8,g5)
    c: Equal(g8,g6)
    c: Equal(g8,g7)
FEATURE [PartDesign::Pocket] Pocket
  BaseFeature = -> Pad004
  Length = 5
  Length2 = 100
  Profile = -> Sketch006
  Type = 0
FEATURE [PartDesign::CoordinateSystem] mount
  AttacherType = Attacher::AttachEngine3D
  MapMode = 11
  Placement = pos=(0,0,67) rot=(0,0,1;1.5708rad)
  Support = -> [Pocket]
FEATURE [PartDesign::Body] Body  label="MOTOR-11HS12"
  Group = -> [Sketch,Pad,Sketch002,Pad001,Sketch003,Pad002,Sketch004,Pad003,Sketch005,Pad004,Sketch006,Pocket,mount]
  Origin = -> Origin
  Tip = -> Pocket
---- part MOTOR-17HS13-0404S-PG27.FCStd = doc fcstd_2512dda9dd6d ----
FCSTD DOCUMENT  (FreeCAD 0.19R24276 (Git))
Label: MOTOR-17HS13-0404S-PG27
License: All rights reserved
LicenseURL: http://en.wikipedia.org/wiki/All_rights_reserved
objects: Sketcher::SketchObject×5, PartDesign::Pad×4, PartDesign::CoordinateSystem×2, PartDesign::Pocket×1, PartDesign::Body×1, App::Part×1
note: 18 computed .brp shape members not serialized (recipe doc carries the construction recipe); baked Part::Feature solids carry a one-line shape summary decoded from their .brp

FEATURE [PartDesign::CoordinateSystem] LCS_0
  AttacherType = Attacher::AttachEngine3D
  MapMode = 2
  Support = -> [X_Axis]
FEATURE [PartDesign::CoordinateSystem] LCS_0001
  AttacherType = Attacher::AttachEngine3D
  MapMode = 2
  Support = -> [X_Axis001]
FEATURE [Sketcher::SketchObject] Sketch
  FullyConstrained = true
  MapMode = 5
  Support = -> [XY_Plane001]
  sketch-geometry (1):
    g0: Circle CenterX=0 CenterY=0 CenterZ=0 NormalX=0 NormalY=0 NormalZ=1 AngleXU=0 Radius=18
  constraints (2):
    c: Coincident(g0,g-1)
    c: Diameter(g0) = 36
FEATURE [PartDesign::Pad] Pad
  Direction = (1,1,1)
  Length = 35
  Length2 = 100
  Profile = -> Sketch
  Refine = true
  Reversed = true
  Type = 0
FEATURE [Sketcher::SketchObject] Sketch001
  AttachmentOffset = pos=(0,0,-35) rot=(0,0,1;0rad)
  FullyConstrained = true
  MapMode = 5
  Placement = pos=(0,0,-35) rot=(0,0,1;0rad)
  Support = -> [XY_Plane001]
  sketch-geometry (4):
    g0: LineSegment StartX=-21.15 StartY=21.15 StartZ=0 EndX=21.15 EndY=21.15 EndZ=0
    g1: LineSegment StartX=21.15 StartY=21.15 StartZ=0 EndX=21.15 EndY=-21.15 EndZ=0
    g2: LineSegment StartX=21.15 StartY=-21.15 StartZ=0 EndX=-21.15 EndY=-21.15 EndZ=0
    g3: LineSegment StartX=-21.15 StartY=-21.15 StartZ=0 EndX=-21.15 EndY=21.15 EndZ=0
  constraints (10):
    c: Coincident(g0,g1)
    c: Coincident(g1,g2)
    c: Coincident(g2,g3)
    c: Coincident(g3,g0)
    c: Horizontal(g2)
    c: Vertical(g1)
    c: Symmetric(g0,g0,g-2)
    c: Symmetric(g0,g2,g-1)
    c: Equal(g0,g3)
    c: DistanceX(g0,g0) = 42.3
FEATURE [PartDesign::Pad] Pad001
  BaseFeature = -> Pad
  Direction = (1,1,1)
  Length = 34
  Length2 = 100
  Profile = -> Sketch001
  Refine = true
  Reversed = true
  Type = 0
FEATURE [Sketcher::SketchObject] Sketch002
  FullyConstrained = true
  MapMode = 5
  Support = -> [XY_Plane001]
  sketch-geometry (1):
    g0: Circle CenterX=0 CenterY=0 CenterZ=0 NormalX=0 NormalY=0 NormalZ=1 AngleXU=0 Radius=11
  constraints (2):
    c: Coincident(g0,g-1)
    c: Diameter(g0) = 22
FEATURE [PartDesign::Pad] Pad002
  BaseFeature = -> Pad001
  Direction = (1,1,1)
  Length = 2
  Length2 = 100
  Profile = -> Sketch002
  Refine = true
  Type = 0
FEATURE [Sketcher::SketchObject] Sketch003
  FullyConstrained = true
  MapMode = 5
  Support = -> [XY_Plane001]
  sketch-geometry (1):
    g0: Circle CenterX=0 CenterY=0 CenterZ=0 NormalX=0 NormalY=0 NormalZ=1 AngleXU=0 Radius=3
  constraints (2):
    c: Coincident(g0,g-1)
    c: Diameter(g0) = 6
FEATURE [PartDesign::Pad] Pad003
  BaseFeature = -> Pad002
  Direction = (1,1,1)
  Length = 18
  Length2 = 100
  Profile = -> Sketch003
  Refine = true
  Type = 0
FEATURE [Sketcher::SketchObject] Sketch004
  FullyConstrained = true
  MapMode = 5
  Support = -> [XY_Plane001]
  sketch-geometry (9):
    g0: Circle CenterX=0 CenterY=0 CenterZ=0 NormalX=0 NormalY=0 NormalZ=1 AngleXU=0 Radius=14
    g1: LineSegment StartX=-9.89949 StartY=9.89949 StartZ=0 EndX=9.89949 EndY=9.89949 EndZ=0
    g2: LineSegment StartX=9.89949 StartY=9.89949 StartZ=0 EndX=9.89949 EndY=-9.89949 EndZ=0
    g3: LineSegment StartX=9.89949 StartY=-9.89949 StartZ=0 EndX=-9.89949 EndY=-9.89949 EndZ=0
    g4: LineSegment StartX=-9.89949 StartY=-9.89949 StartZ=0 EndX=-9.89949 EndY=9.89949 EndZ=0
    g5: Circle CenterX=-9.89949 CenterY=9.89949 CenterZ=0 NormalX=0 NormalY=0 NormalZ=1 AngleXU=0 Radius=1.5
    g6: Circle CenterX=9.89949 CenterY=9.89949 CenterZ=0 NormalX=0 NormalY=0 NormalZ=1 AngleXU=0 Radius=1.5
    g7: Circle CenterX=9.89949 CenterY=-9.89949 CenterZ=0 NormalX=0 NormalY=0 NormalZ=1 AngleXU=0 Radius=1.5
    g8: Circle CenterX=-9.89949 CenterY=-9.89949 CenterZ=0 NormalX=0 NormalY=0 NormalZ=1 AngleXU=0 Radius=1.5
  constraints (22):
    c: Coincident(g0,g-1)
    c: Diameter(g0) = 28
    c: Coincident(g1,g2)
    c: Coincident(g2,g3)
    c: Coincident(g3,g4)
    c: Coincident(g4,g1)
    c: Horizontal(g1)
    c: Horizontal(g3)
    c: Vertical(g2)
    c: Vertical(g4)
    c: PointOnObject(g1,g0)
    c: PointOnObject(g2,g0)
    c: Equal(g2,g1)
    c: PointOnObject(g1,g0)
    c: Coincident(g5,g1)
    c: Coincident(g6,g1)
    c: Coincident(g7,g2)
    c: Coincident(g8,g3)
    c: Diameter(g8) = 3
    c: Equal(g8,g5)
    c: Equal(g8,g6)
    c: Equal(g8,g7)
FEATURE [PartDesign::Pocket] Pocket
  BaseFeature = -> Pad003
  Length = 5
  Length2 = 100
  Profile = -> Sketch004
  Type = 0
FEATURE [PartDesign::Body] Body
  Group = -> [LCS_0001,Sketch,Pad,Sketch001,Pad001,Sketch002,Pad002,Sketch003,Pad003,Sketch004,Pocket]
  Origin = -> Origin001
  Tip = -> Pocket
FEATURE [App::Part] Part
  Group = -> [LCS_0,Body]
  Origin = -> Origin
---- part WASHER-M6.FCStd = doc fcstd_eba2b1a27f3f ----
FCSTD DOCUMENT  (FreeCAD 0.19R24276 (Git))
Label: WASHER-M6
License: All rights reserved
LicenseURL: http://en.wikipedia.org/wiki/All_rights_reserved
objects: PartDesign::CoordinateSystem×2, Sketcher::SketchObject×1, PartDesign::Pad×1, PartDesign::Body×1
note: 6 computed .brp shape members not serialized (recipe doc carries the construction recipe); baked Part::Feature solids carry a one-line shape summary decoded from their .brp

FEATURE [PartDesign::CoordinateSystem] LCS_0
  AttacherType = Attacher::AttachEngine3D
  MapMode = 2
  Support = -> [X_Axis]
FEATURE [Sketcher::SketchObject] Sketch
  FullyConstrained = false
  MapMode = 5
  Support = -> [XY_Plane]
  sketch-geometry (2):
    g0: Circle CenterX=0 CenterY=0 CenterZ=0 NormalX=0 NormalY=0 NormalZ=1 AngleXU=0 Radius=3.2
    g1: Circle CenterX=0 CenterY=0 CenterZ=0 NormalX=0 NormalY=0 NormalZ=1 AngleXU=0 Radius=6
  constraints (4):
    c: Coincident(g0,g-1)
    c: Coincident(g1,g0)
    c: Diameter(g1) = 12
    c: Diameter(g0) = 6.4
FEATURE [PartDesign::Pad] Pad
  Direction = (1,1,1)
  Length = 1.6
  Length2 = 100
  Profile = -> Sketch
  Refine = true
  Type = 0
FEATURE [PartDesign::CoordinateSystem] LCS_1
  AttacherType = Attacher::AttachEngine3D
  MapMode = 11
  Placement = pos=(-4e-16,0,1.6) rot=(0,0,1;1.5708rad)
  Support = -> [Pad]
FEATURE [PartDesign::Body] WASHER_M6
  Group = -> [LCS_0,Sketch,Pad,LCS_1]
  Origin = -> Origin
  Tip = -> Pad
